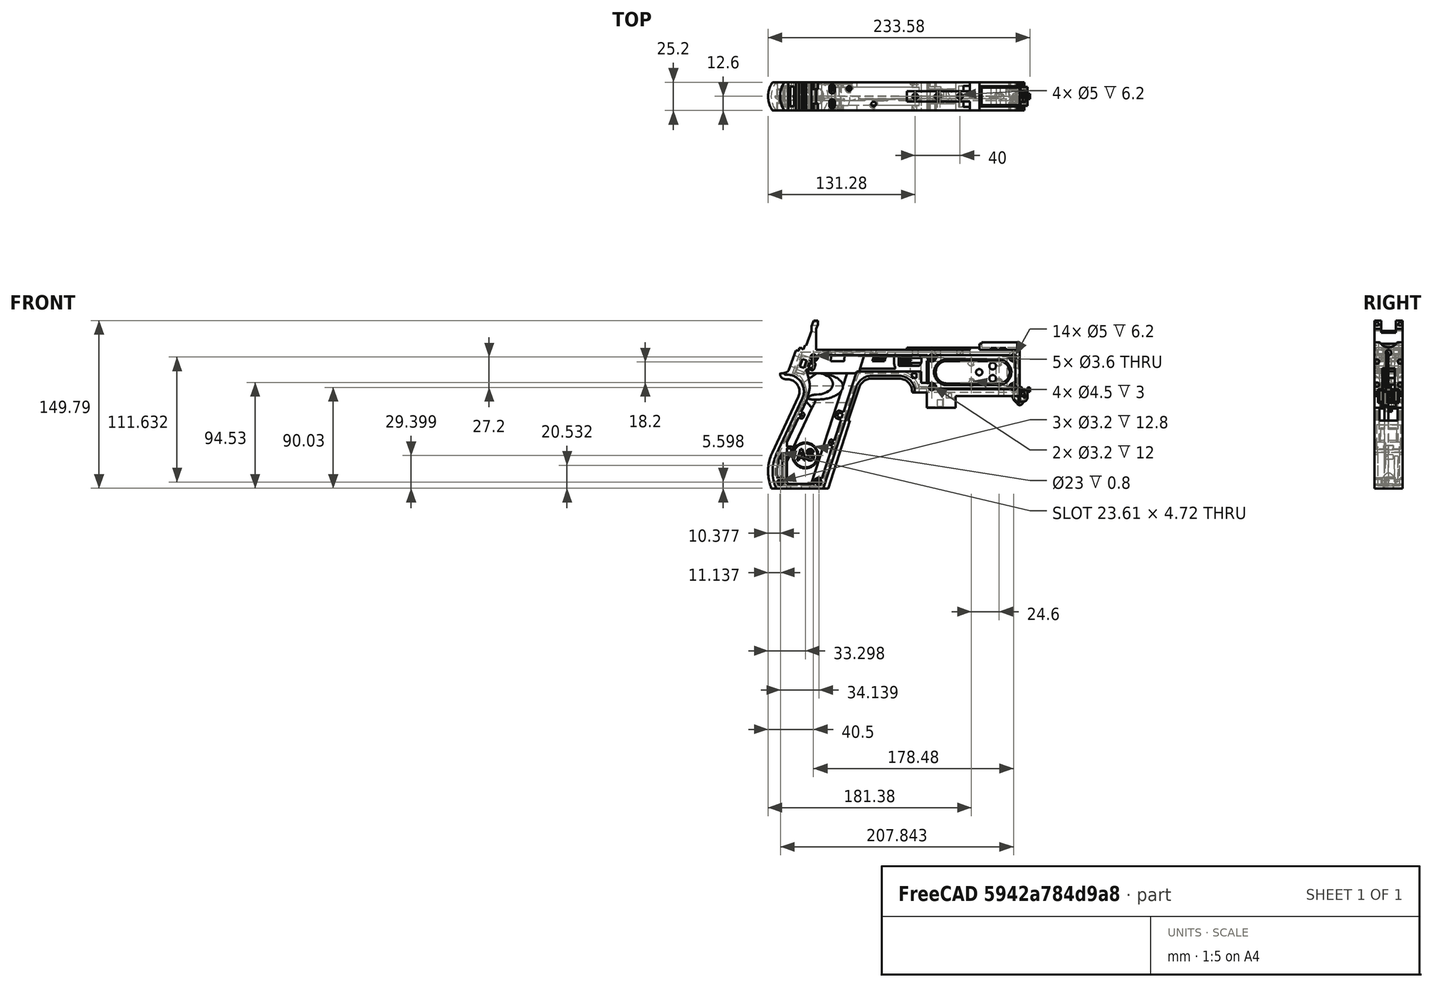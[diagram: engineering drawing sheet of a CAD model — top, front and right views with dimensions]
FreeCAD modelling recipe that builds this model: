
FCSTD DOCUMENT  (FreeCAD 1.0R39319 (Git))
Label: PICON-OF_ver_39_ultimo_della_prima_revisione
License: All rights reserved
LicenseURL: https://en.wikipedia.org/wiki/All_rights_reserved
objects: Sketcher::SketchObject×107, Part::Extrusion×50, Part::Cut×39, PartDesign::Pad×29, PartDesign::Pocket×18, PartDesign::Chamfer×15, PartDesign::Body×10, PartDesign::Fillet×6, PartDesign::SubtractivePipe×4, Part::Part2DObjectPython×4, PartDesign::SubtractiveLoft×4, PartDesign::Plane×2, PartDesign::SubShapeBinder×2, Part::Sweep×1, PartDesign::ShapeBinder×1, Part::MultiFuse×1, Mesh::Feature×1
note: 552 computed .brp shape members not serialized (recipe doc carries the construction recipe); baked Part::Feature solids carry a one-line shape summary decoded from their .brp

FEATURE [Sketcher::SketchObject] Sketch  label="corpo principale"
  ArcFitTolerance = 1e-06
  AttacherType = Attacher::AttachEngine3D
  AttachmentSupport = -> [XZ_Plane]
  FullyConstrained = true
  MakeInternals = false
  MapMode = 5
  Placement = pos=(0,0,0) rot=(1,0,0;1.5708rad)
  sketch-geometry (65):
    g0: LineSegment StartX=0 StartY=0 StartZ=0 EndX=-57.2 EndY=0 EndZ=0
    g1: LineSegment StartX=-57.2 StartY=0 StartZ=0 EndX=-57.2 EndY=-10.4 EndZ=0
    g2: LineSegment StartX=-57.2 StartY=-10.4 StartZ=0 EndX=-82.8 EndY=-10.4 EndZ=0
    g3: LineSegment StartX=-82.8 StartY=-10.4 StartZ=0 EndX=-82.8 EndY=3.2 EndZ=0
    g4: LineSegment StartX=-82.8 StartY=3.2 StartZ=0 EndX=-93.6 EndY=3.2 EndZ=0
    g5: LineSegment StartX=-93.6 StartY=3.2 StartZ=0 EndX=-93.6 EndY=4 EndZ=0
    g6: LineSegment StartX=-107.6 StartY=18 StartZ=0 EndX=-132.428 EndY=18 EndZ=0
    g7: LineSegment StartX=-145.743 StartY=8.32624 StartZ=0 EndX=-175.232 EndY=-82.4316 EndZ=0
    g8: LineSegment StartX=-175.232 StartY=-82.4316 StartZ=0 EndX=-217.232 EndY=-82.4316 EndZ=0
    g9: LineSegment StartX=-217.232 StartY=-52.1862 StartZ=0 EndX=-193.988 EndY=-2.33927 EndZ=0
    g10: LineSegment StartX=-206.196 StartY=23.0857 StartZ=0 EndX=-199.861 EndY=40.4914 EndZ=0
    g11: LineSegment StartX=-199.861 StartY=40.4914 StartZ=0 EndX=-197.061 EndY=40.4914 EndZ=0
    g12: LineSegment StartX=-197.061 StartY=40.4914 StartZ=0 EndX=-197.061 EndY=42.8914 EndZ=0
    g13: LineSegment StartX=-197.061 StartY=42.8914 StartZ=0 EndX=-194.261 EndY=42.8914 EndZ=0
    g14: LineSegment StartX=-194.261 StartY=42.8914 StartZ=0 EndX=-194.535 EndY=42.1397 EndZ=0
    g15: LineSegment StartX=-194.535 StartY=42.1397 StartZ=0 EndX=-193.031 EndY=41.5924 EndZ=0
    g16: LineSegment StartX=-193.031 StartY=41.5924 StartZ=0 EndX=-191.663 EndY=45.3512 EndZ=0
    g17: LineSegment StartX=-191.663 StartY=45.3512 StartZ=0 EndX=-190.536 EndY=44.9408 EndZ=0
    g18: LineSegment StartX=-190.536 StartY=44.9408 StartZ=0 EndX=-185.747 EndY=58.0965 EndZ=0
    g19: LineSegment StartX=-185.747 StartY=58.0965 StartZ=0 EndX=-185.747 EndY=62.0965 EndZ=0
    g20: LineSegment StartX=-185.747 StartY=62.0965 StartZ=0 EndX=-183.832 EndY=67.3588 EndZ=0
    g21: LineSegment StartX=-183.832 StartY=67.3588 StartZ=0 EndX=-180.232 EndY=67.3588 EndZ=0
    g22: LineSegment StartX=-180.232 StartY=67.3588 StartZ=0 EndX=-180.232 EndY=63.7588 EndZ=0
    g23: LineSegment StartX=-180.232 StartY=63.7588 StartZ=0 EndX=-181.6 EndY=60 EndZ=0
    g24: LineSegment StartX=-181.6 StartY=60 StartZ=0 EndX=-181.6 EndY=41.2 EndZ=0
    g25: LineSegment StartX=-181.6 StartY=41.2 StartZ=0 EndX=-100.8 EndY=41.2 EndZ=0
    g26: LineSegment StartX=-36 StartY=43.2 StartZ=0 EndX=-36 EndY=41.2 EndZ=0
    g27: LineSegment StartX=0 StartY=48 StartZ=0 EndX=0 EndY=0 EndZ=0
    g28: LineSegment StartX=-209.901 StartY=19.85 StartZ=0 EndX=-209.901 EndY=20.1 EndZ=0
    g29: LineSegment StartX=-208.001 StartY=22 StartZ=0 EndX=-207.747 EndY=22 EndZ=0
    g30: LineSegment StartX=-207.583 StartY=19 StartZ=0 EndX=-209.051 EndY=19 EndZ=0
    g31: ArcOfCircle CenterX=-208.001 CenterY=20.1 CenterZ=0 NormalX=0 NormalY=0 NormalZ=1 AngleXU=0 Radius=1.9 StartAngle=1.5708 EndAngle=3.14159
    g32: GeomPoint [constr] X=-209.901 Y=22 Z=0
    g33: ArcOfCircle CenterX=-209.051 CenterY=19.85 CenterZ=0 NormalX=0 NormalY=0 NormalZ=1 AngleXU=0 Radius=0.85 StartAngle=3.14159 EndAngle=4.71239
    g34: GeomPoint [constr] X=-209.901 Y=19 Z=0
    g35: ArcOfCircle CenterX=-207.747 CenterY=23.65 CenterZ=0 NormalX=0 NormalY=0 NormalZ=1 AngleXU=0 Radius=1.65 StartAngle=4.71239 EndAngle=5.93412
    g36: GeomPoint [constr] X=-206.591 Y=22 Z=0
    g37: LineSegment StartX=-4 StartY=6 StartZ=0 EndX=-4 EndY=36.4 EndZ=0
    g38: LineSegment StartX=-4 StartY=36.4 StartZ=0 EndX=-185.2 EndY=36.4 EndZ=0
    g39: LineSegment StartX=-185.2 StartY=36.4 StartZ=0 EndX=-190.441 EndY=22 EndZ=0
    g40: LineSegment StartX=-214.575 StartY=-78.4316 StartZ=0 EndX=-178.142 EndY=-78.4316 EndZ=0
    g41: LineSegment StartX=-178.142 StartY=-78.4316 StartZ=0 EndX=-145.51 EndY=22 EndZ=0
    g42: LineSegment StartX=-145.51 StartY=22 StartZ=0 EndX=-87.91 EndY=22 EndZ=0
    g43: LineSegment StartX=-87.91 StartY=22 StartZ=0 EndX=-87.91 EndY=11.6 EndZ=0
    g44: LineSegment StartX=-87.91 StartY=11.6 StartZ=0 EndX=-80.11 EndY=11.6 EndZ=0
    g45: LineSegment StartX=-80.11 StartY=11.6 StartZ=0 EndX=-80.11 EndY=6 EndZ=0
    g46: LineSegment StartX=-80.11 StartY=6 StartZ=0 EndX=-4 EndY=6 EndZ=0
    g47: LineSegment StartX=-190.363 StartY=-4.02975 StartZ=0 EndX=-213.607 EndY=-53.8767 EndZ=0
    g48: ArcOfCircle CenterX=-132.428 CenterY=4 CenterZ=0 NormalX=0 NormalY=0 NormalZ=1 AngleXU=0 Radius=14 StartAngle=1.5708 EndAngle=2.82743
    g49: GeomPoint [constr] X=-142.6 Y=18 Z=0
    g50: ArcOfCircle CenterX=-107.6 CenterY=4 CenterZ=0 NormalX=0 NormalY=0 NormalZ=1 AngleXU=0 Radius=14 StartAngle=0 EndAngle=1.5708
    g51: GeomPoint [constr] X=-93.6 Y=18 Z=0
    g52: ArcOfCircle CenterX=-184.801 CenterY=-67.3089 CenterZ=0 NormalX=0 NormalY=0 NormalZ=1 AngleXU=0 Radius=35.7833 StartAngle=2.70526 EndAngle=3.57792
    g53: ArcOfCircle CenterX=-207.583 CenterY=4 CenterZ=0 NormalX=0 NormalY=0 NormalZ=1 AngleXU=0 Radius=15 StartAngle=5.84685 EndAngle=7.85398
    g54: LineSegment [constr] StartX=-213.607 StartY=-53.8767 StartZ=0 EndX=-217.232 EndY=-52.1862 EndZ=0
    g55: ArcOfCircle CenterX=-184.801 CenterY=-67.3089 CenterZ=0 NormalX=0 NormalY=0 NormalZ=1 AngleXU=0 Radius=31.7833 StartAngle=2.70526 EndAngle=3.49911
    g56: ArcOfCircle CenterX=-218.095 CenterY=8.90192 CenterZ=0 NormalX=0 NormalY=0 NormalZ=1 AngleXU=0 Radius=30.5989 StartAngle=5.84685 EndAngle=6.72553
    g57: LineSegment StartX=-44.6 StartY=43.2 StartZ=0 EndX=-36 EndY=43.2 EndZ=0
    g58: LineSegment StartX=-100.8 StartY=41.2 StartZ=0 EndX=-44.6 EndY=41.2 EndZ=0
    g59: LineSegment StartX=-44.6 StartY=41.2 StartZ=0 EndX=-44.6 EndY=43.2 EndZ=0
    g60: LineSegment StartX=-2.4 StartY=48 StartZ=0 EndX=0 EndY=48 EndZ=0
    g61: LineSegment StartX=-36 StartY=41.2 StartZ=0 EndX=-2.4 EndY=41.2 EndZ=0
    g62: LineSegment StartX=-2.4 StartY=41.2 StartZ=0 EndX=-2.4 EndY=48 EndZ=0
    g63: LineSegment [constr] StartX=-181.6 StartY=36.4 StartZ=0 EndX=-152.209 EndY=36.4 EndZ=0
    g64: LineSegment [constr] StartX=-181.6 StartY=36.4 StartZ=0 EndX=-130.41 EndY=36.4 EndZ=0
  constraints (183):
    c: Coincident(g-1,g0)
    c: PointOnObject(g0,g-1)
    c: Coincident(g0,g1)
    c: Vertical(g1)
    c: Coincident(g1,g2)
    c: Horizontal(g2)
    c: Coincident(g2,g3)
    c: Vertical(g3)
    c: Coincident(g3,g4)
    c: Coincident(g4,g5)
    c: Vertical(g5)
    c: Horizontal(g6)
    c: Coincident(g7,g8)
    c: Horizontal(g8)
    c: Coincident(g10,g11)
    c: Horizontal(g11)
    c: Coincident(g11,g12)
    c: Vertical(g12)
    c: Coincident(g12,g13)
    c: Horizontal(g13)
    c: Coincident(g13,g14)
    c: Coincident(g14,g15)
    c: Coincident(g15,g16)
    c: Coincident(g16,g17)
    c: Coincident(g17,g18)
    c: Coincident(g18,g19)
    c: Vertical(g19)
    c: Coincident(g19,g20)
    c: Coincident(g20,g21)
    c: Horizontal(g21)
    c: Coincident(g21,g22)
    c: Vertical(g22)
    c: Coincident(g22,g23)
    c: Coincident(g23,g24)
    c: Vertical(g24)
    c: Coincident(g24,g25)
    c: Horizontal(g25)
    c: Coincident(g57,g26)
    c: Vertical(g26)
    c: Coincident(g26,g61)
    c: PointOnObject(g60,g-2)
    c: Coincident(g60,g27)
    c: Coincident(g27,g0)
    c: DistanceY(g27,g27) = 48
    c: DistanceY(g1,g1) = 10.4
    c: DistanceX(g0,g0) = 57.2
    c: DistanceX(g2,g2) = 25.6
    c: Horizontal(g4)
    c: DistanceY(g3,g3) = 13.6
    c: DistanceX(g4,g4) = 10.8
    c: DistanceY(g5,g51) = 14.8
    c: DistanceX(g49,g51) = 49
    c: Distance(g7,g49) = 105.6
    c: DistanceX(g61,g60) = 36
    c: DistanceX(g25,g25) = 80.8
    c: DistanceY(g24,g24) = 18.8
    c: DistanceY(g22,g22) = 3.6
    c: Distance(g23) = 4
    c: Angle(g-1,g23) = 1.22173
    c: DistanceX(g21,g21) = 3.6
    c: Distance(g20) = 5.6
    c: Angle(g-1,g20) = 1.22173
    c: DistanceY(g19,g19) = 4
    c: Distance(g18) = 14
    c: Angle(g-1,g18) = 1.22173
    c: Distance(g17) = 1.2
    c: Distance(g16) = 4
    c: Angle(g16) = 1.22173
    c: Perpendicular(g18,g17)
    c: Distance(g15) = 1.6
    c: Perpendicular(g16,g15)
    c: Distance(g14) = 0.8
    c: DistanceX(g13,g13) = 2.8
    c: Perpendicular(g15,g14)
    c: DistanceY(g12,g12) = 2.4
    c: DistanceX(g11,g11) = 2.8
    c: Distance(g9) = 55
    c: Angle(g9,g-1) = 2.00713
    c: Horizontal(g29)
    c: Vertical(g28)
    c: Horizontal(g30)
    c: PointOnObject(g32,g29)
    c: PointOnObject(g32,g28)
    c: Tangent(g29,g31) = 1.5708
    c: Tangent(g28,g31) = 1.5708
    c: PointOnObject(g34,g28)
    c: PointOnObject(g34,g30)
    c: Tangent(g28,g33) = 1.5708
    c: Tangent(g30,g33) = 1.5708
    c: PointOnObject(g36,g29)
    c: PointOnObject(g36,g10)
    c: Tangent(g29,g35) = -1.5708
    c: Tangent(g10,g35) = -1.5708
    c: Angle(g-1,g10) = 1.22173
    c: Radius(g35) = 1.65
    c: Vertical(g37)
    c: Coincident(g37,g38)
    c: Horizontal(g38)
    c: Coincident(g38,g39)
    c: Horizontal(g40)
    c: Coincident(g40,g41)
    c: Coincident(g41,g42)
    c: Horizontal(g42)
    c: Coincident(g42,g43)
    c: Vertical(g43)
    c: Coincident(g43,g44)
    c: Horizontal(g44)
    c: Coincident(g44,g45)
    c: Vertical(g45)
    c: Coincident(g45,g46)
    c: Coincident(g46,g37)
    c: Horizontal(g46)
    c: DistanceY(g0,g37) = 6
    c: DistanceX(g37,g0) = 4
    c: DistanceY(g37,g25) = 4.8
    c: DistanceX(g38,g38) = 181.2
    c: DistanceX(g42,g42) = 57.6
    c: DistanceY(g49,g41) = 4
    c: DistanceX(g41,g49) = 2.91
    c: DistanceY(g43,g43) = 10.4
    c: DistanceX(g44,g44) = 7.8
    c: DistanceY(g7,g40) = 4
    c: Distance(g47) = 55
    c: Angle(g-1,g39) = 1.22173
    c: PointOnObject(g49,g7)
    c: PointOnObject(g49,g6)
    c: Tangent(g7,g48) = -1.5708
    c: Tangent(g6,g48) = -1.5708
    c: PointOnObject(g51,g5)
    c: PointOnObject(g51,g6)
    c: Tangent(g5,g50) = -1.5708
    c: Tangent(g6,g50) = -1.5708
    c: Radius(g50) = 14
    c: Radius(g48) = 14
    c: DistanceX(g8,g8) = 42
    c: Angle(g7,g-1) = 1.88496
    c: Parallel(g41,g7)
    c: Parallel(g47,g9)
    c: Coincident(g52,g8)
    c: Tangent(g52,g9) = 1.5708
    c: DistanceX(g9,g8) = 0
    c: Tangent(g53,g9) = -1.5708
    c: Tangent(g53,g30) = -1.5708
    c: Diameter(g53) = 30
    c: DistanceY(g53,g0) = -4
    c: Coincident(g54,g47)
    c: Distance(g54) = 4
    c: Coincident(g54,g9)
    c: Coincident(g55,g40)
    c: Tangent(g55,g47) = -1.5708
    c: Coincident(g52,g55)
    c: Coincident(g56,g39)
    c: Tangent(g56,g47) = 1.5708
    c: Horizontal(g57)
    c: DistanceX(g57,g57) = 8.6
    c: Coincident(g58,g25)
    c: Horizontal(g58)
    c: Coincident(g59,g58)
    c: Vertical(g59)
    c: DistanceY(g58,g57) = 2
    c: DistanceX(g58,g58) = 56.2
    c: Coincident(g59,g57)
    c: DistanceY(g41,g36) = 0
    c: DistanceY(g36,g39) = 0
    c: DistanceY(g28,g28) = 0.25
    c: DistanceX(g30,g36) = 2.46
    c: DistanceX(g28,g29) = 1.9
    c: Coincident(g62,g60)
    c: Horizontal(g60)
    c: DistanceX(g62,g27) = 2.4
    c: Coincident(g61,g62)
    c: DistanceY(g26,g26) = 2
    c: Vertical(g62)
    c: DistanceY(g61,g60) = 6.8
    c: Horizontal(g61)
    c: Distance(g63) = 29.391
    c: PointOnObject(g63,g38)
    c: PointOnObject(g63,g38)
    c: Distance(g64) = 51.19
    c: PointOnObject(g64,g38)
    c: PointOnObject(g64,g38)
    c: DistanceX(g24,g63) = 0
    c: DistanceX(g24,g64) = 0
FEATURE [Part::Extrusion] Extrude  label="Extrude corpo principale"
  Base = -> Sketch
  Dir = (0,-1,2e-16)
  DirMode = 2
  FaceMakerClass = Part::FaceMakerBullseye
  FaceMakerMode = 3
  LengthFwd = 25.2
  LengthRev = 12.6
  Solid = true
  Symmetric = true
FEATURE [Sketcher::SketchObject] Sketch002  label="scavo grilletto"
  ArcFitTolerance = 1e-06
  AttachmentSupport = -> [XZ_Plane]
  ExternalGeometry = -> [Sketch]
  FullyConstrained = true
  MakeInternals = false
  MapMode = 5
  Placement = pos=(0,0,0) rot=(1,0,0;1.5708rad)
  sketch-geometry (4):
    g0: LineSegment StartX=-89.51 StartY=22 StartZ=0 EndX=-152.71 EndY=22 EndZ=0
    g1: LineSegment StartX=-152.71 StartY=22 StartZ=0 EndX=-167.006 EndY=-22 EndZ=0
    g2: LineSegment StartX=-167.006 StartY=-22 StartZ=0 EndX=-89.51 EndY=-22 EndZ=0
    g3: LineSegment StartX=-89.51 StartY=-22 StartZ=0 EndX=-89.51 EndY=22 EndZ=0
  constraints (12):
    c: Horizontal(g0)
    c: Coincident(g0,g1)
    c: Coincident(g1,g2)
    c: Horizontal(g2)
    c: Coincident(g2,g3)
    c: Coincident(g3,g0)
    c: Vertical(g3)
    c: Angle(g1,g0) = 1.88496
    c: DistanceY(g3,g3) = 44
    c: DistanceX(g0,g0) = 63.2
    c: DistanceX(g0,g-3) = 1.6
    c: DistanceY(g-3,g0) = 0
FEATURE [Sketcher::SketchObject] Sketch004  label="traiettoria arrotondamento impugnatura anteriore"
  ArcFitTolerance = 1e-06
  AttachmentSupport = -> [XZ_Plane]
  ExternalGeometry = -> [Sketch]
  FullyConstrained = true
  MakeInternals = false
  MapMode = 5
  Placement = pos=(0,0,0) rot=(1,0,0;1.5708rad)
  sketch-geometry (13):
    g0: LineSegment StartX=-175.232 StartY=-82.4316 StartZ=0 EndX=-145.743 EndY=8.32624 EndZ=0
    g1: LineSegment StartX=-93.6 StartY=3.2 StartZ=0 EndX=-93.6 EndY=4 EndZ=0
    g2: LineSegment StartX=-132.428 StartY=18 StartZ=0 EndX=-107.6 EndY=18 EndZ=0
    g3: ArcOfCircle CenterX=-132.428 CenterY=4 CenterZ=0 NormalX=0 NormalY=0 NormalZ=1 AngleXU=0 Radius=14 StartAngle=1.5708 EndAngle=2.82743
    g4: ArcOfCircle CenterX=-107.6 CenterY=4 CenterZ=0 NormalX=0 NormalY=0 NormalZ=1 AngleXU=0 Radius=14 StartAngle=0 EndAngle=1.5708
    g5: LineSegment StartX=-175.232 StartY=-82.4316 StartZ=0 EndX=-217.232 EndY=-82.4316 EndZ=0
    g6: LineSegment StartX=-217.232 StartY=-52.1862 StartZ=0 EndX=-193.988 EndY=-2.33927 EndZ=0
    g7: LineSegment StartX=-209.051 StartY=19 StartZ=0 EndX=-207.583 EndY=19 EndZ=0
    g8: LineSegment StartX=-209.901 StartY=20.1 StartZ=0 EndX=-209.901 EndY=19.85 EndZ=0
    g9: ArcOfCircle CenterX=-184.801 CenterY=-67.3089 CenterZ=0 NormalX=0 NormalY=0 NormalZ=1 AngleXU=0 Radius=35.7833 StartAngle=2.70526 EndAngle=3.57792
    g10: ArcOfCircle CenterX=-207.583 CenterY=4 CenterZ=0 NormalX=0 NormalY=0 NormalZ=1 AngleXU=0 Radius=15 StartAngle=5.84685 EndAngle=7.85398
    g11: ArcOfCircle CenterX=-209.051 CenterY=19.85 CenterZ=0 NormalX=0 NormalY=0 NormalZ=1 AngleXU=0 Radius=0.85 StartAngle=3.14159 EndAngle=4.71239
    g12: ArcOfCircle CenterX=-208.001 CenterY=20.1 CenterZ=0 NormalX=0 NormalY=0 NormalZ=1 AngleXU=0 Radius=1.9 StartAngle=1.5708 EndAngle=3.14159
  constraints (26):
    c: Coincident(g0,g-3)
    c: Coincident(g0,g-6)
    c: Coincident(g1,g-8)
    c: Coincident(g1,g-7)
    c: Coincident(g2,g-5)
    c: Coincident(g2,g-4)
    c: Coincident(g3,g2)
    c: Tangent(g3,g0) = 1.5708
    c: Coincident(g4,g1)
    c: Tangent(g4,g2) = 1.5708
    c: Coincident(g5,g0)
    c: Coincident(g5,g-9)
    c: Coincident(g6,g-12)
    c: Coincident(g6,g-11)
    c: Coincident(g7,g-15)
    c: Coincident(g7,g-14)
    c: Coincident(g8,g-16)
    c: Coincident(g8,g-17)
    c: Tangent(g9,g6) = 1.5708
    c: Coincident(g9,g5)
    c: Coincident(g10,g7)
    c: Tangent(g10,g6) = -1.5708
    c: Tangent(g11,g7) = -1.5708
    c: Coincident(g11,g8)
    c: Tangent(g12,g8) = -1.5708
    c: Coincident(g12,g-17)
FEATURE [PartDesign::Plane] DatumPlane  label="Piano per disegno arrotondamento impugnatura"
  AttachmentSupport = -> [Sketch]
  Length = 68.5841
  MapMode = 7
  Placement = pos=(-145.743,1.8e-15,8.32624) rot=(0.154555,0.154555,0.97582;1.59527rad)
  ResizeMode = 0
  Width = 191.269
FEATURE [Sketcher::SketchObject] Sketch005  label="forma arrotondamento impugnatura anteriore"
  ArcFitTolerance = 1e-06
  AttachmentSupport = -> [DatumPlane]
  FullyConstrained = true
  MakeInternals = false
  MapMode = 5
  Placement = pos=(-145.743,1.8e-15,8.32624) rot=(0.154555,0.154555,0.97582;1.59527rad)
  sketch-geometry (5):
    g0: GeomPoint [constr] X=0 Y=-4 Z=0
    g1: GeomPoint [constr] X=-12.6 Y=7.1e-15 Z=0
    g2: GeomPoint [constr] X=12.6 Y=4.97e-14 Z=0
    g3: LineSegment StartX=-12.6 StartY=7.1e-15 StartZ=0 EndX=12.6 EndY=4.97e-14 EndZ=0
    g4: ArcOfCircle CenterX=-3.88e-14 CenterY=17.845 CenterZ=0 NormalX=0 NormalY=0 NormalZ=1 AngleXU=0 Radius=21.845 StartAngle=4.09759 EndAngle=5.32718
  constraints (11):
    c: DistanceY(g0,g-1) = 4
    c: DistanceX(g-1,g0) = 0
    c: DistanceX(g1,g-1) = 12.6
    c: DistanceX(g-1,g2) = 12.6
    c: DistanceY(g-1,g2) = 0
    c: DistanceY(g-1,g1) = 0
    c: Coincident(g3,g1)
    c: Coincident(g3,g2)
    c: Coincident(g4,g1)
    c: Coincident(g4,g2)
    c: PointOnObject(g0,g4)
FEATURE [Part::Sweep] Sweep  label="Sweep impugnatura"
  Frenet = true
  Sections = -> [Sketch005]
  Solid = true
  Spine = -> Sketch [Edge32,Edge33,Edge34,Edge35,Edge36,Edge37,Edge38,Edge39,Edge40,Edge41,Edge42,Edge43,Edge44]
  Transition = 1
FEATURE [Sketcher::SketchObject] Sketch008  label="buchi e pulizie varie"
  ArcFitTolerance = 1e-06
  AttachmentSupport = -> [XZ_Plane]
  ExternalGeometry = -> [Sketch]
  FullyConstrained = true
  MakeInternals = false
  MapMode = 5
  Placement = pos=(0,0,0) rot=(1,0,0;1.5708rad)
  sketch-geometry (26):
    g0: LineSegment StartX=-96.278 StartY=20.155 StartZ=0 EndX=-92.278 EndY=20.155 EndZ=0
    g1: LineSegment StartX=-92.278 StartY=20.155 StartZ=0 EndX=-92.278 EndY=16.155 EndZ=0
    g2: LineSegment StartX=-92.278 StartY=16.155 StartZ=0 EndX=-96.278 EndY=16.155 EndZ=0
    g3: LineSegment StartX=-96.278 StartY=16.155 StartZ=0 EndX=-96.278 EndY=20.155 EndZ=0
    g4: LineSegment StartX=-222.232 StartY=-82.4316 StartZ=0 EndX=-170.232 EndY=-82.4316 EndZ=0
    g5: LineSegment StartX=-170.232 StartY=-82.4316 StartZ=0 EndX=-170.232 EndY=-86.4316 EndZ=0
    g6: LineSegment StartX=-170.232 StartY=-86.4316 StartZ=0 EndX=-222.232 EndY=-86.4316 EndZ=0
    g7: LineSegment StartX=-222.232 StartY=-86.4316 StartZ=0 EndX=-222.232 EndY=-82.4316 EndZ=0
    g8: LineSegment StartX=-213.901 StartY=20.1 StartZ=0 EndX=-213.901 EndY=26 EndZ=0
    g9: LineSegment StartX=-213.901 StartY=26 StartZ=0 EndX=-206.196 EndY=26 EndZ=0
    g10: LineSegment StartX=-17.4 StartY=42.8 StartZ=0 EndX=-12.4 EndY=42.8 EndZ=0
    g11: LineSegment StartX=-12.4 StartY=42.8 StartZ=0 EndX=-12.4 EndY=41.2 EndZ=0
    g12: LineSegment StartX=-12.4 StartY=41.2 StartZ=0 EndX=-17.4 EndY=41.2 EndZ=0
    g13: LineSegment StartX=-17.4 StartY=41.2 StartZ=0 EndX=-17.4 EndY=42.8 EndZ=0
    g14: LineSegment StartX=-25.9 StartY=42.8 StartZ=0 EndX=-20.9 EndY=42.8 EndZ=0
    g15: LineSegment StartX=-20.9 StartY=42.8 StartZ=0 EndX=-20.9 EndY=41.2 EndZ=0
    g16: LineSegment StartX=-20.9 StartY=41.2 StartZ=0 EndX=-25.9 EndY=41.2 EndZ=0
    g17: LineSegment StartX=-25.9 StartY=41.2 StartZ=0 EndX=-25.9 EndY=42.8 EndZ=0
    g18: GeomPoint [constr] X=-206.196 Y=23.0857 Z=0
    g19: GeomPoint [constr] X=-213.901 Y=20.1 Z=0
    g20: BSplineCurve PolesCount=4 KnotsCount=2 Degree=3 IsPeriodic=0
    g21-g24: Circle [constr] x4 (B-spline internal-alignment scaffolding for g20; pole/knot coordinates omitted)
    g25: LineSegment StartX=-206.196 StartY=26 StartZ=0 EndX=-206.196 EndY=23.0857 EndZ=0
  constraints (73):
    c: Horizontal(g0)
    c: Coincident(g1,g0)
    c: Vertical(g1)
    c: Coincident(g2,g1)
    c: Horizontal(g2)
    c: Coincident(g3,g2)
    c: Coincident(g3,g0)
    c: Vertical(g3)
    c: DistanceX(g0,g-4) = 4.368
    c: DistanceY(g0,g-4) = 1.845
    c: DistanceY(g1,g1) = 4
    c: DistanceX(g2,g2) = 4
    c: Horizontal(g4)
    c: Coincident(g5,g4)
    c: Vertical(g5)
    c: Coincident(g6,g5)
    c: Horizontal(g6)
    c: Coincident(g7,g6)
    c: Coincident(g7,g4)
    c: Vertical(g7)
    c: DistanceY(g7,g7) = 4
    c: DistanceX(g4,g-5) = 5
    c: DistanceX(g-5,g4) = 5
    c: DistanceY(g4,g-5) = 0
    c: Coincident(g9,g8)
    c: Parallel(g9,g-6)
    c: DistanceX(g8,g-8) = 4
    c: Horizontal(g10)
    c: Coincident(g11,g10)
    c: Vertical(g11)
    c: Coincident(g12,g11)
    c: Horizontal(g12)
    c: Coincident(g13,g12)
    c: Coincident(g13,g10)
    c: Vertical(g13)
    c: Horizontal(g14)
    c: Coincident(g15,g14)
    c: Vertical(g15)
    c: Coincident(g16,g15)
    c: Horizontal(g16)
    c: Coincident(g17,g16)
    c: Coincident(g17,g14)
    c: Vertical(g17)
    c: DistanceY(g11,g10) = 1.6
    c: DistanceX(g10,g10) = 5
    c: DistanceY(g15,g14) = 1.6
    c: DistanceX(g14,g14) = 5
    c: DistanceX(g15,g12) = 3.5
    c: DistanceX(g11,g-9) = 10
    c: DistanceY(g-9,g11) = 0
    c: DistanceY(g-9,g15) = 0
    c: Perpendicular(g8,g9)
    c: DistanceY(g-7,g9) = 4
    c: DistanceY(g8,g-8) = 0
    c: InternalAlignment(g18,g20)
    c: InternalAlignment(g19,g20)
    c: InternalAlignment(g21,g20)
    c: Weight(g21) = 1
    c: InternalAlignment(g22,g20)
    c: Equal(g22,g21)
    c: InternalAlignment(g23,g20)
    c: Equal(g23,g21)
    c: InternalAlignment(g24,g20)
    c: Equal(g24,g21)
    c: Coincident(g18,g-12)
    c: Coincident(g19,g8)
    c: Coincident(g25,g9)
    c: Coincident(g25,g20)
    c: Vertical(g25)
    c: DistanceY(g20,g23) = 0
    c: DistanceY(g22,g18) = 2.26
    c: DistanceX(g22,g18) = 0.93
    c: DistanceX(g20,g23) = 2.9
FEATURE [Part::Extrusion] Extrude004  label="Extrude Buchi e pulizie varie"
  Base = -> Sketch008
  Dir = (0,-1,2e-16)
  DirMode = 2
  FaceMakerClass = Part::FaceMakerBullseye
  FaceMakerMode = 3
  LengthFwd = 25.2
  LengthRev = 0
  Solid = true
  Symmetric = true
FEATURE [Sketcher::SketchObject] Sketch009  label="rinforzi"
  ArcFitTolerance = 1e-06
  AttachmentSupport = -> [XZ_Plane]
  ExternalGeometry = -> [Sketch]
  FullyConstrained = true
  MakeInternals = false
  MapMode = 5
  Placement = pos=(0,0,0) rot=(1,0,0;1.5708rad)
  sketch-geometry (9):
    g0: LineSegment StartX=-87.91 StartY=22 StartZ=0 EndX=-87.91 EndY=36.4 EndZ=0
    g1: LineSegment StartX=-87.91 StartY=36.4 StartZ=0 EndX=-97.91 EndY=36.4 EndZ=0
    g2: LineSegment StartX=-97.91 StartY=36.4 StartZ=0 EndX=-97.91 EndY=22 EndZ=0
    g3: LineSegment StartX=-97.91 StartY=22 StartZ=0 EndX=-87.91 EndY=22 EndZ=0
    g4: LineSegment StartX=-149.713 StartY=9.06563 StartZ=0 EndX=-154.586 EndY=-5.93437 EndZ=0
    g5: LineSegment StartX=-154.586 StartY=-5.93437 StartZ=0 EndX=-191.863 EndY=-5.93437 EndZ=0
    g6: LineSegment StartX=-191.863 StartY=-5.93437 StartZ=0 EndX=-191.863 EndY=9.06563 EndZ=0
    g7: LineSegment StartX=-191.863 StartY=9.06563 StartZ=0 EndX=-149.713 EndY=9.06563 EndZ=0
    g8: LineSegment [constr] StartX=-145.51 StartY=22 StartZ=0 EndX=-149.713 EndY=9.06563 EndZ=0
  constraints (25):
    c: Vertical(g0)
    c: Coincident(g1,g0)
    c: Horizontal(g1)
    c: Coincident(g2,g1)
    c: Vertical(g2)
    c: Coincident(g3,g2)
    c: Coincident(g3,g0)
    c: Horizontal(g3)
    c: Coincident(g0,g-4)
    c: DistanceX(g3,g3) = 10
    c: DistanceY(g0,g-3) = 0
    c: Coincident(g5,g4)
    c: Horizontal(g5)
    c: Coincident(g6,g5)
    c: Vertical(g6)
    c: Coincident(g7,g6)
    c: Coincident(g7,g4)
    c: Horizontal(g7)
    c: Distance(g8) = 13.6
    c: Parallel(g-6,g8)
    c: Coincident(g-6,g8)
    c: Parallel(g4,g-6)
    c: DistanceY(g4,g4) = 15
    c: Coincident(g4,g8)
    c: DistanceX(g-5,g5) = -1.5
FEATURE [Part::Extrusion] Extrude001  label="Extrude scavo grilletto"
  Base = -> Sketch002
  Dir = (0,-1,2e-16)
  DirMode = 2
  FaceMakerClass = Part::FaceMakerBullseye
  FaceMakerMode = 3
  LengthFwd = 16
  LengthRev = 0
  Solid = true
  Symmetric = true
FEATURE [Part::Extrusion] Extrude005  label="Extrude Rinforzi"
  Base = -> Sketch009
  Dir = (0,-1,2e-16)
  DirMode = 2
  FaceMakerClass = Part::FaceMakerBullseye
  FaceMakerMode = 3
  LengthFwd = 2
  LengthRev = 0
  Placement = pos=(0,12.6,0) rot=(0,0,1;0rad)
  Solid = true
  Symmetric = false
FEATURE [PartDesign::ShapeBinder] CopyCut
  TraceSupport = false
FEATURE [PartDesign::Plane] DatumPlane001
  AttachmentSupport = -> [CopyCut]
  Length = 60
  MapMode = 5
  Placement = pos=(0,12.6,0) rot=(0,0.707107,0.707107;3.14159rad)
  ResizeMode = 0
  Width = 60
FEATURE [Sketcher::SketchObject] Sketch010  label="buco neopixel"
  ArcFitTolerance = 1e-06
  AttachmentSupport = -> [XZ_Plane]
  ExternalGeometry = -> [Sketch]
  FullyConstrained = true
  MakeInternals = false
  MapMode = 5
  Placement = pos=(0,0,0) rot=(1,0,0;1.5708rad)
  sketch-geometry (5):
    g0: LineSegment [constr] StartX=-199.861 StartY=40.4914 StartZ=0 EndX=-201.368 EndY=36.3521 EndZ=0
    g1: LineSegment StartX=-201.368 StartY=36.3521 StartZ=0 EndX=-204.932 EndY=26.5605 EndZ=0
    g2: LineSegment StartX=-201.368 StartY=36.3521 StartZ=0 EndX=-180.2 EndY=28.6477 EndZ=0
    g3: LineSegment StartX=-180.2 StartY=28.6477 StartZ=0 EndX=-183.764 EndY=18.8561 EndZ=0
    g4: LineSegment StartX=-183.764 StartY=18.8561 StartZ=0 EndX=-204.932 EndY=26.5605 EndZ=0
  constraints (14):
    c: Parallel(g0,g-3)
    c: Distance(g0) = 4.405
    c: Coincident(g0,g-3)
    c: Coincident(g2,g1)
    c: Coincident(g3,g2)
    c: Coincident(g4,g3)
    c: Coincident(g4,g1)
    c: Parallel(g1,g-3)
    c: Distance(g1) = 10.42
    c: Coincident(g1,g0)
    c: Parallel(g2,g4)
    c: Perpendicular(g1,g2)
    c: DistanceX(g-4,g2) = 5
    c: Parallel(g3,g1)
FEATURE [Part::Extrusion] Extrude006  label="Extrude buco neopixel"
  Base = -> Sketch010
  Dir = (0,-1,2e-16)
  DirMode = 2
  FaceMakerClass = Part::FaceMakerBullseye
  FaceMakerMode = 3
  LengthFwd = 17.2
  LengthRev = 0
  Solid = true
  Symmetric = true
FEATURE [Sketcher::SketchObject] Sketch011  label="fermo grilletto"
  ArcFitTolerance = 1e-06
  AttachmentSupport = -> [XZ_Plane]
  ExternalGeometry = -> [Sketch]
  FullyConstrained = true
  MakeInternals = false
  MapMode = 5
  Placement = pos=(0,0,0) rot=(1,0,0;1.5708rad)
  sketch-geometry (18):
    g0: LineSegment [constr] StartX=-145.51 StartY=22 StartZ=0 EndX=-157.347 EndY=-14.4293 EndZ=0
    g1: LineSegment [constr] StartX=-157.347 StartY=-14.4293 StartZ=0 EndX=-157.841 EndY=-15.951 EndZ=0
    g2: LineSegment StartX=-161.151 StartY=-13.1932 StartZ=0 EndX=-155.825 EndY=-14.9237 EndZ=0
    g3: LineSegment StartX=-163.167 StartY=-14.2205 StartZ=0 EndX=-164.403 EndY=-18.0247 EndZ=0
    g4: LineSegment StartX=-163.376 StartY=-20.0408 StartZ=0 EndX=-158.05 EndY=-21.7713 EndZ=0
    g5: LineSegment StartX=-158.05 StartY=-21.7713 StartZ=0 EndX=-155.825 EndY=-14.9237 EndZ=0
    g6: LineSegment StartX=-161.645 StartY=-14.7149 StartZ=0 EndX=-157.841 EndY=-15.951 EndZ=0
    g7: LineSegment StartX=-157.841 StartY=-15.951 StartZ=0 EndX=-159.077 EndY=-19.7552 EndZ=0
    g8: LineSegment StartX=-159.077 StartY=-19.7552 StartZ=0 EndX=-162.881 EndY=-18.5191 EndZ=0
    g9: LineSegment StartX=-162.881 StartY=-18.5191 StartZ=0 EndX=-161.645 EndY=-14.7149 EndZ=0
    g10: LineSegment [constr] StartX=-161.645 StartY=-14.7149 StartZ=0 EndX=-161.151 EndY=-13.1932 EndZ=0
    g11: LineSegment [constr] StartX=-159.077 StartY=-19.7552 StartZ=0 EndX=-157.555 EndY=-20.2496 EndZ=0
    g12: LineSegment [constr] StartX=-159.077 StartY=-19.7552 StartZ=0 EndX=-159.572 EndY=-21.2769 EndZ=0
    g13: LineSegment [constr] StartX=-161.645 StartY=-14.7149 StartZ=0 EndX=-163.167 EndY=-14.2205 EndZ=0
    g14: ArcOfCircle CenterX=-161.645 CenterY=-14.7149 CenterZ=0 NormalX=0 NormalY=0 NormalZ=1 AngleXU=0 Radius=1.6 StartAngle=1.25664 EndAngle=2.82743
    g15: GeomPoint [constr] X=-162.673 Y=-12.6988 Z=0
    g16: ArcOfCircle CenterX=-162.881 CenterY=-18.5191 CenterZ=0 NormalX=0 NormalY=0 NormalZ=1 AngleXU=0 Radius=1.6 StartAngle=2.82743 EndAngle=4.39823
    g17: GeomPoint [constr] X=-164.897 Y=-19.5464 Z=0
  constraints (48):
    c: Parallel(g0,g-3)
    c: Distance(g0) = 38.304
    c: Coincident(g0,g-3)
    c: Parallel(g1,g-3)
    c: Distance(g1) = 1.6
    c: Coincident(g1,g0)
    c: Coincident(g5,g4)
    c: Coincident(g5,g2)
    c: Coincident(g7,g6)
    c: Coincident(g8,g7)
    c: Coincident(g9,g8)
    c: Coincident(g9,g6)
    c: Parallel(g7,g-3)
    c: Parallel(g9,g7)
    c: Perpendicular(g6,g7)
    c: Parallel(g6,g8)
    c: Distance(g6) = 4
    c: Distance(g9) = 4
    c: Parallel(g5,g7)
    c: Parallel(g9,g3)
    c: Parallel(g2,g6)
    c: Parallel(g4,g8)
    c: Parallel(g13,g6)
    c: Parallel(g10,g9)
    c: Parallel(g11,g8)
    c: Parallel(g12,g7)
    c: Distance(g10) = 1.6
    c: Distance(g13) = 1.6
    c: Distance(g12) = 1.6
    c: Distance(g11) = 1.6
    c: Coincident(g10,g6)
    c: Coincident(g13,g6)
    c: Coincident(g12,g7)
    c: Coincident(g11,g7)
    c: Distance(g10,g15) = 1.6
    c: Distance(g15,g13) = 1.6
    c: Distance(g4,g12) = 1.6
    c: Distance(g4,g11) = 1.6
    c: PointOnObject(g15,g2)
    c: Tangent(g3,g14) = -1.5708
    c: Tangent(g2,g14) = 1.5708
    c: PointOnObject(g17,g4)
    c: PointOnObject(g17,g3)
    c: Tangent(g4,g16) = -1.5708
    c: Tangent(g3,g16) = -1.5708
    c: Equal(g16,g14)
    c: Coincident(g16,g8)
    c: Coincident(g6,g1)
FEATURE [Part::Extrusion] Extrude007  label="Extrude fermo grilletto"
  Base = -> Sketch011
  Dir = (0,-1,2e-16)
  DirMode = 2
  FaceMakerClass = Part::FaceMakerBullseye
  FaceMakerMode = 3
  LengthFwd = 25.2
  LengthRev = 0
  Solid = true
  Symmetric = true
FEATURE [Sketcher::SketchObject] Sketch012  label="buco oled"
  ArcFitTolerance = 1e-06
  AttachmentSupport = -> [XZ_Plane]
  ExternalGeometry = -> [Sketch]
  FullyConstrained = true
  MakeInternals = false
  MapMode = 5
  Placement = pos=(0,0,0) rot=(1,0,0;1.5708rad)
  sketch-geometry (4):
    g0: LineSegment StartX=-185.747 StartY=58.0965 StartZ=0 EndX=-180.232 EndY=56.0891 EndZ=0
    g1: LineSegment StartX=-185.747 StartY=58.0965 StartZ=0 EndX=-185.747 EndY=67.3588 EndZ=0
    g2: LineSegment StartX=-185.747 StartY=67.3588 StartZ=0 EndX=-180.232 EndY=67.3588 EndZ=0
    g3: LineSegment StartX=-180.232 StartY=67.3588 StartZ=0 EndX=-180.232 EndY=56.0891 EndZ=0
  constraints (10):
    c: Coincident(g1,g0)
    c: Coincident(g2,g1)
    c: Coincident(g3,g2)
    c: Coincident(g3,g0)
    c: Parallel(g1,g-5)
    c: Perpendicular(g-3,g0)
    c: Parallel(g2,g-6)
    c: Parallel(g3,g-4)
    c: Coincident(g0,g-5)
    c: Coincident(g2,g-6)
FEATURE [Part::Extrusion] Extrude008  label="Extrude buco oled"
  Base = -> Sketch012
  Dir = (0,-1,2e-16)
  DirMode = 2
  FaceMakerClass = Part::FaceMakerBullseye
  FaceMakerMode = 3
  LengthFwd = 12.8
  LengthRev = 0
  Solid = true
  Symmetric = true
FEATURE [Sketcher::SketchObject] Sketch013  label="buco pompa"
  ArcFitTolerance = 1e-06
  AttachmentSupport = -> [XZ_Plane]
  ExternalGeometry = -> [Sketch]
  FullyConstrained = true
  MakeInternals = false
  MapMode = 5
  Placement = pos=(0,0,0) rot=(1,0,0;1.5708rad)
  sketch-geometry (8):
    g0: LineSegment StartX=-82.8 StartY=-10.4 StartZ=0 EndX=-82.8 EndY=-9.6 EndZ=0
    g1: LineSegment StartX=-82.8 StartY=-9.6 StartZ=0 EndX=-67.9 EndY=-9.6 EndZ=0
    g2: LineSegment StartX=-67.9 StartY=-9.6 StartZ=0 EndX=-67.9 EndY=6 EndZ=0
    g3: LineSegment StartX=-67.9 StartY=6 StartZ=0 EndX=-65.9 EndY=6 EndZ=0
    g4: LineSegment StartX=-65.9 StartY=6 StartZ=0 EndX=-65.9 EndY=-1.7 EndZ=0
    g5: LineSegment StartX=-65.9 StartY=-1.7 StartZ=0 EndX=-57.2 EndY=-1.7 EndZ=0
    g6: LineSegment StartX=-57.2 StartY=-1.7 StartZ=0 EndX=-57.2 EndY=-10.4 EndZ=0
    g7: LineSegment StartX=-57.2 StartY=-10.4 StartZ=0 EndX=-82.8 EndY=-10.4 EndZ=0
  constraints (22):
    c: Vertical(g0)
    c: Coincident(g1,g0)
    c: Horizontal(g1)
    c: Coincident(g2,g1)
    c: Vertical(g2)
    c: Coincident(g3,g2)
    c: Horizontal(g3)
    c: Coincident(g4,g3)
    c: Vertical(g4)
    c: Coincident(g5,g4)
    c: Horizontal(g5)
    c: Coincident(g6,g5)
    c: Vertical(g6)
    c: Coincident(g7,g6)
    c: Coincident(g7,g0)
    c: DistanceY(g0,g0) = 0.8
    c: DistanceY(g6,g6) = 8.7
    c: DistanceX(g1,g1) = 14.9
    c: DistanceX(g3,g3) = 2
    c: Coincident(g0,g-4)
    c: DistanceY(g2,g-6) = 0
    c: Coincident(g6,g-5)
FEATURE [Part::Extrusion] Extrude009  label="Extrude buco pompa"
  Base = -> Sketch013
  Dir = (0,-1,2e-16)
  DirMode = 2
  FaceMakerClass = Part::FaceMakerBullseye
  FaceMakerMode = 3
  LengthFwd = 13.2
  LengthRev = 0
  Solid = true
  Symmetric = true
FEATURE [Sketcher::SketchObject] Sketch014  label="buco frontale"
  ArcFitTolerance = 1e-06
  AttachmentSupport = -> [XZ_Plane]
  ExternalGeometry = -> [Sketch]
  FullyConstrained = true
  MakeInternals = false
  MapMode = 5
  Placement = pos=(0,0,0) rot=(1,0,0;1.5708rad)
  sketch-geometry (10):
    g0: LineSegment StartX=0 StartY=0 StartZ=0 EndX=0 EndY=24.671 EndZ=0
    g1: LineSegment StartX=0 StartY=24.671 StartZ=0 EndX=-4 EndY=24.671 EndZ=0
    g2: LineSegment StartX=-4 StartY=24.671 StartZ=0 EndX=-4 EndY=16 EndZ=0
    g3: LineSegment StartX=-4 StartY=16 StartZ=0 EndX=-2.4 EndY=16 EndZ=0
    g4: LineSegment StartX=-2.4 StartY=16 StartZ=0 EndX=-2.4 EndY=10 EndZ=0
    g5: LineSegment StartX=-2.4 StartY=10 StartZ=0 EndX=-12 EndY=10 EndZ=0
    g6: LineSegment StartX=-12 StartY=10 StartZ=0 EndX=-12 EndY=6 EndZ=0
    g7: LineSegment StartX=-12 StartY=6 StartZ=0 EndX=-2.4 EndY=6 EndZ=0
    g8: LineSegment StartX=-2.4 StartY=6 StartZ=0 EndX=-2.4 EndY=0 EndZ=0
    g9: LineSegment StartX=-2.4 StartY=0 StartZ=0 EndX=0 EndY=0 EndZ=0
  constraints (29):
    c: Vertical(g0)
    c: Coincident(g1,g0)
    c: Horizontal(g1)
    c: Coincident(g2,g1)
    c: Vertical(g2)
    c: Coincident(g3,g2)
    c: Horizontal(g3)
    c: Coincident(g4,g3)
    c: Vertical(g4)
    c: Coincident(g5,g4)
    c: Horizontal(g5)
    c: Coincident(g6,g5)
    c: Vertical(g6)
    c: Coincident(g7,g6)
    c: Coincident(g8,g7)
    c: Vertical(g8)
    c: Coincident(g9,g8)
    c: Coincident(g9,g0)
    c: Horizontal(g9)
    c: DistanceY(g0,g0) = 24.671
    c: Horizontal(g7)
    c: DistanceY(g6,g6) = 4
    c: DistanceY(g4,g4) = 6
    c: DistanceX(g9,g9) = 2.4
    c: Coincident(g0,g-1)
    c: DistanceY(g-3,g7) = 0
    c: DistanceX(g8,g4) = 0
    c: DistanceX(g-3,g1) = 0
    c: DistanceX(g6,g-3) = 8
FEATURE [Part::Extrusion] Extrude010  label="Extrude buco frontale"
  Base = -> Sketch014
  Dir = (0,-1,2e-16)
  DirMode = 2
  FaceMakerClass = Part::FaceMakerBullseye
  FaceMakerMode = 3
  LengthFwd = 11.2
  LengthRev = 0
  Solid = true
  Symmetric = true
FEATURE [Sketcher::SketchObject] Sketch015  label="guida rail"
  ArcFitTolerance = 1e-06
  AttachmentSupport = -> [XZ_Plane]
  ExternalGeometry = -> [Sketch]
  FullyConstrained = true
  MakeInternals = false
  MapMode = 5
  Placement = pos=(0,0,0) rot=(1,0,0;1.5708rad)
  sketch-geometry (4):
    g0: LineSegment StartX=-100.8 StartY=43.2 StartZ=0 EndX=-44.6 EndY=43.2 EndZ=0
    g1: LineSegment StartX=-44.6 StartY=43.2 StartZ=0 EndX=-44.6 EndY=41.2 EndZ=0
    g2: LineSegment StartX=-44.6 StartY=41.2 StartZ=0 EndX=-100.8 EndY=41.2 EndZ=0
    g3: LineSegment StartX=-100.8 StartY=41.2 StartZ=0 EndX=-100.8 EndY=43.2 EndZ=0
  constraints (9):
    c: Horizontal(g0)
    c: Coincident(g1,g0)
    c: Coincident(g2,g1)
    c: Coincident(g3,g2)
    c: Coincident(g3,g0)
    c: Vertical(g3)
    c: Coincident(g2,g-3)
    c: Coincident(g1,g-3)
    c: Coincident(g0,g-4)
FEATURE [Part::Extrusion] Extrude011  label="Extrude guida rail"
  Base = -> Sketch015
  Dir = (0,-1,2e-16)
  DirMode = 2
  FaceMakerClass = Part::FaceMakerBullseye
  FaceMakerMode = 3
  LengthFwd = 9
  LengthRev = 0
  Solid = true
  Symmetric = true
FEATURE [Sketcher::SketchObject] Sketch016  label="guide per coperture laterali"
  ArcFitTolerance = 1e-06
  AttachmentSupport = -> [XZ_Plane]
  ExternalGeometry = -> [Sketch]
  FullyConstrained = true
  MakeInternals = false
  MapMode = 5
  Placement = pos=(0,0,0) rot=(1,0,0;1.5708rad)
  sketch-geometry (14):
    g0: Circle CenterX=-5.6 CenterY=7.6 CenterZ=0 NormalX=0 NormalY=0 NormalZ=1 AngleXU=0 Radius=1.6
    g1: Circle CenterX=-5.6 CenterY=7.6 CenterZ=0 NormalX=0 NormalY=0 NormalZ=1 AngleXU=0 Radius=4
    g2: Circle CenterX=-5.6 CenterY=34.8 CenterZ=0 NormalX=0 NormalY=0 NormalZ=1 AngleXU=0 Radius=1.6
    g3: Circle CenterX=-5.6 CenterY=34.8 CenterZ=0 NormalX=0 NormalY=0 NormalZ=1 AngleXU=0 Radius=4
    g4: Circle CenterX=-184.08 CenterY=34.8 CenterZ=0 NormalX=0 NormalY=0 NormalZ=1 AngleXU=0 Radius=1.6
    g5: Circle CenterX=-184.08 CenterY=34.8 CenterZ=0 NormalX=0 NormalY=0 NormalZ=1 AngleXU=0 Radius=4
    g6: Circle CenterX=-179.305 CenterY=-76.8316 CenterZ=0 NormalX=0 NormalY=0 NormalZ=1 AngleXU=0 Radius=1.6
    g7: Circle CenterX=-179.305 CenterY=-76.8316 CenterZ=0 NormalX=0 NormalY=0 NormalZ=1 AngleXU=0 Radius=4
    g8: Circle CenterX=-213.443 CenterY=-76.8316 CenterZ=0 NormalX=0 NormalY=0 NormalZ=1 AngleXU=0 Radius=1.6
    g9: Circle CenterX=-213.443 CenterY=-76.8316 CenterZ=0 NormalX=0 NormalY=0 NormalZ=1 AngleXU=0 Radius=4
    g10: Circle CenterX=-78.51 CenterY=7.6 CenterZ=0 NormalX=0 NormalY=0 NormalZ=1 AngleXU=0 Radius=1.6
    g11: Circle CenterX=-78.51 CenterY=7.6 CenterZ=0 NormalX=0 NormalY=0 NormalZ=1 AngleXU=0 Radius=4
    g12: Circle CenterX=-78.51 CenterY=34.8 CenterZ=0 NormalX=0 NormalY=0 NormalZ=1 AngleXU=0 Radius=1.6
    g13: Circle CenterX=-78.51 CenterY=34.8 CenterZ=0 NormalX=0 NormalY=0 NormalZ=1 AngleXU=0 Radius=4
  constraints (35):
    c: Diameter(g0) = 3.2
    c: Diameter(g1) = 8
    c: Coincident(g0,g1)
    c: Diameter(g2) = 3.2
    c: Diameter(g3) = 8
    c: Coincident(g3,g2)
    c: Tangent(g2,g-7)
    c: Diameter(g4) = 3.2
    c: Diameter(g5) = 8
    c: Coincident(g5,g4)
    c: Tangent(g4,g-7)
    c: Tangent(g4,g-8)
    c: Diameter(g6) = 3.2
    c: Diameter(g7) = 8
    c: Coincident(g7,g6)
    c: Tangent(g6,g-9)
    c: Tangent(g6,g-10)
    c: Diameter(g8) = 3.2
    c: Diameter(g9) = 8
    c: Coincident(g9,g8)
    c: Tangent(g8,g-10)
    c: Tangent(g8,g-11)
    c: Diameter(g10) = 3.2
    c: Diameter(g11) = 8
    c: Diameter(g12) = 3.2
    c: Diameter(g13) = 8
    c: Coincident(g12,g13)
    c: Coincident(g10,g11)
    c: Tangent(g12,g-7)
    c: DistanceX(g12,g10) = 0
    c: Tangent(g2,g-6)
    c: Tangent(g0,g-6)
    c: Tangent(g0,g-3)
    c: Tangent(g10,g-3)
    c: Tangent(g10,g-4)
FEATURE [Part::Extrusion] Extrude012  label="extrude guide per coperture laterali"
  Base = -> Sketch016
  Dir = (0,-1,2e-16)
  DirMode = 2
  FaceMakerClass = Part::FaceMakerBullseye
  FaceMakerMode = 3
  LengthFwd = 25.2
  LengthRev = 0
  Solid = true
  Symmetric = true
FEATURE [Sketcher::SketchObject] Sketch017  label="supporto CAM"
  ArcFitTolerance = 1e-06
  AttachmentSupport = -> [XZ_Plane]
  ExternalGeometry = -> [Sketch]
  FullyConstrained = true
  MakeInternals = false
  MapMode = 5
  Placement = pos=(0,0,0) rot=(1,0,0;1.5708rad)
  sketch-geometry (6):
    g0: LineSegment StartX=-2.4 StartY=48 StartZ=0 EndX=-2.4 EndY=41.2 EndZ=0
    g1: LineSegment StartX=-2.4 StartY=48 StartZ=0 EndX=-34 EndY=48 EndZ=0
    g2: LineSegment StartX=-34 StartY=48 StartZ=0 EndX=-34 EndY=46.72 EndZ=0
    g3: LineSegment StartX=-34 StartY=46.72 StartZ=0 EndX=-36 EndY=46.72 EndZ=0
    g4: LineSegment StartX=-36 StartY=46.72 StartZ=0 EndX=-36 EndY=41.2 EndZ=0
    g5: LineSegment StartX=-36 StartY=41.2 StartZ=0 EndX=-2.4 EndY=41.2 EndZ=0
  constraints (15):
    c: Coincident(g1,g0)
    c: Horizontal(g1)
    c: Coincident(g2,g1)
    c: Vertical(g2)
    c: Coincident(g3,g2)
    c: Horizontal(g3)
    c: Coincident(g4,g3)
    c: Coincident(g5,g4)
    c: DistanceX(g1,g0) = 31.6
    c: Coincident(g5,g0)
    c: Vertical(g4)
    c: DistanceY(g2,g1) = 1.28
    c: Coincident(g0,g-3)
    c: Coincident(g0,g-3)
    c: Coincident(g4,g-4)
FEATURE [Part::Extrusion] Extrude013  label="Extrude supporto CAM"
  Base = -> Sketch017
  Dir = (0,-1,2e-16)
  DirMode = 2
  FaceMakerClass = Part::FaceMakerBullseye
  FaceMakerMode = 3
  LengthFwd = 17.8
  LengthRev = 0
  Solid = true
  Symmetric = true
FEATURE [Sketcher::SketchObject] Sketch018  label="Scavo CAM"
  ArcFitTolerance = 1e-06
  AttachmentSupport = -> [YZ_Plane]
  ExternalGeometry = -> [Sketch]
  FullyConstrained = true
  MakeInternals = false
  MapMode = 5
  Placement = pos=(0,0,0) rot=(0.57735,0.57735,0.57735;2.0944rad)
  sketch-geometry (4):
    g0: LineSegment StartX=-7.73 StartY=48 StartZ=0 EndX=7.73 EndY=48 EndZ=0
    g1: LineSegment [constr] StartX=1.07e-14 StartY=48 StartZ=0 EndX=0 EndY=43.5155 EndZ=0
    g2: ArcOfCircle CenterX=9e-15 CenterY=52.42 CenterZ=0 NormalX=0 NormalY=0 NormalZ=1 AngleXU=0 Radius=8.90445 StartAngle=3.66102 EndAngle=5.76376
    g3: Circle [constr] CenterX=9e-15 CenterY=52.42 CenterZ=0 NormalX=0 NormalY=0 NormalZ=1 AngleXU=0 Radius=8.9
  constraints (13):
    c: Horizontal(g0)
    c: DistanceY(g-3,g0) = 0
    c: DistanceX(g0,g0) = 15.46
    c: DistanceX(g0,g-3) = 7.73
    c: DistanceX(g-3) = 0
    c: Coincident(g1,g-3)
    c: PointOnObject(g1,g-2)
    c: Coincident(g2,g0)
    c: Coincident(g2,g0)
    c: PointOnObject(g1,g2)
    c: Diameter(g3) = 17.8
    c: DistanceY(g1,g3) = 4.42
    c: Coincident(g2,g3)
FEATURE [Part::Extrusion] Extrude014  label="Extrude Scavo CAM"
  Base = -> Sketch018
  Dir = (1,0,0)
  DirMode = 2
  FaceMakerClass = Part::FaceMakerBullseye
  FaceMakerMode = 3
  LengthFwd = -34
  LengthRev = 0
  Solid = true
  Symmetric = false
FEATURE [Sketcher::SketchObject] Sketch019  label="scavo rumble"
  ArcFitTolerance = 1e-06
  AttachmentSupport = -> [XZ_Plane]
  ExternalGeometry = -> [Sketch]
  FullyConstrained = true
  MakeInternals = false
  MapMode = 5
  Placement = pos=(0,0,0) rot=(1,0,0;1.5708rad)
  sketch-geometry (6):
    g0: LineSegment StartX=-164.575 StartY=-24.3786 StartZ=0 EndX=-159.439 EndY=-26.0473 EndZ=0
    g1: LineSegment StartX=-159.439 StartY=-26.0473 StartZ=0 EndX=-166.547 EndY=-47.9216 EndZ=0
    g2: LineSegment StartX=-166.547 StartY=-47.9216 StartZ=0 EndX=-171.682 EndY=-46.2529 EndZ=0
    g3: LineSegment StartX=-171.682 StartY=-46.2529 StartZ=0 EndX=-164.575 EndY=-24.3786 EndZ=0
    g4: LineSegment [constr] StartX=-145.51 StartY=22 StartZ=0 EndX=-160.961 EndY=-25.5528 EndZ=0
    g5: LineSegment [constr] StartX=-159.439 StartY=-26.0473 StartZ=0 EndX=-160.961 EndY=-25.5528 EndZ=0
  constraints (17):
    c: Coincident(g1,g0)
    c: Coincident(g2,g1)
    c: Coincident(g3,g2)
    c: Coincident(g3,g0)
    c: Parallel(g3,g-3)
    c: Parallel(g3,g1)
    c: Perpendicular(g3,g0)
    c: Perpendicular(g2,g3)
    c: Distance(g2,g0) = 23
    c: Parallel(g4,g-3)
    c: Distance(g4) = 50
    c: Coincident(g4,g-3)
    c: Parallel(g5,g0)
    c: Distance(g5) = 1.6
    c: Coincident(g5,g0)
    c: Distance(g5,g0) = 3.8
    c: Coincident(g5,g4)
FEATURE [Part::Extrusion] Extrude015  label="scavo rumble001"
  Base = -> Sketch019
  Dir = (0,-1,2e-16)
  DirMode = 2
  FaceMakerClass = Part::FaceMakerBullseye
  FaceMakerMode = 3
  LengthFwd = 21
  LengthRev = 0
  Solid = true
  Symmetric = true
FEATURE [Sketcher::SketchObject] Sketch020  label="fermo rumble"
  ArcFitTolerance = 1e-06
  AttachmentSupport = -> [XZ_Plane]
  ExternalGeometry = -> [Sketch019,Sketch]
  FullyConstrained = true
  MakeInternals = false
  MapMode = 5
  Placement = pos=(0,0,0) rot=(1,0,0;1.5708rad)
  sketch-geometry (16):
    g0: LineSegment [constr] StartX=-166.709 StartY=-43.2425 StartZ=0 EndX=-168.068 EndY=-47.4271 EndZ=0
    g1: LineSegment [constr] StartX=-168.068 StartY=-47.4271 StartZ=0 EndX=-166.547 EndY=-47.9216 EndZ=0
    g2: LineSegment StartX=-168.121 StartY=-40.4703 StartZ=0 EndX=-166.029 EndY=-41.1502 EndZ=0
    g3: LineSegment StartX=-166.029 StartY=-41.1502 StartZ=0 EndX=-166.709 EndY=-43.2425 EndZ=0
    g4: LineSegment StartX=-166.709 StartY=-43.2425 StartZ=0 EndX=-168.801 EndY=-42.5626 EndZ=0
    g5: LineSegment StartX=-168.801 StartY=-42.5626 StartZ=0 EndX=-168.121 EndY=-40.4703 EndZ=0
    g6: LineSegment StartX=-167.627 StartY=-38.9486 StartZ=0 EndX=-164.203 EndY=-40.0611 EndZ=0
    g7: LineSegment StartX=-164.203 StartY=-40.0611 StartZ=0 EndX=-165.81 EndY=-45.0066 EndZ=0
    g8: LineSegment StartX=-165.81 StartY=-45.0066 StartZ=0 EndX=-169.234 EndY=-43.8941 EndZ=0
    g9: LineSegment StartX=-170.261 StartY=-41.878 StartZ=0 EndX=-169.643 EndY=-39.9759 EndZ=0
    g10: LineSegment [constr] StartX=-169.643 StartY=-39.9759 StartZ=0 EndX=-169.148 EndY=-38.4542 EndZ=0
    g11: LineSegment [constr] StartX=-169.148 StartY=-38.4542 StartZ=0 EndX=-167.627 EndY=-38.9486 EndZ=0
    g12: ArcOfCircle CenterX=-168.739 CenterY=-42.3724 CenterZ=0 NormalX=0 NormalY=0 NormalZ=1 AngleXU=0 Radius=1.6 StartAngle=2.82743 EndAngle=4.39823
    g13: GeomPoint [constr] X=-170.755 Y=-43.3997 Z=0
    g14: ArcOfCircle CenterX=-168.121 CenterY=-40.4703 CenterZ=0 NormalX=0 NormalY=0 NormalZ=1 AngleXU=0 Radius=1.6 StartAngle=1.25664 EndAngle=2.82743
    g15: GeomPoint [constr] X=-169.148 Y=-38.4542 Z=0
  constraints (42):
    c: Parallel(g0,g-4)
    c: Distance(g0) = 4.4
    c: Coincident(g1,g0)
    c: Perpendicular(g0,g1)
    c: Distance(g1) = 1.6
    c: Coincident(g1,g-5)
    c: Coincident(g3,g2)
    c: Coincident(g4,g3)
    c: Coincident(g5,g4)
    c: Coincident(g5,g2)
    c: Parallel(g3,g-4)
    c: Parallel(g3,g5)
    c: Perpendicular(g2,g3)
    c: Parallel(g4,g2)
    c: Distance(g2) = 2.2
    c: Distance(g3) = 2.2
    c: Coincident(g7,g6)
    c: Coincident(g8,g7)
    c: Parallel(g7,g-4)
    c: Parallel(g7,g9)
    c: Perpendicular(g6,g7)
    c: Parallel(g6,g8)
    c: Distance(g6,g15) = 5.2
    c: Distance(g7) = 5.2
    c: Coincident(g11,g10)
    c: Parallel(g10,g9)
    c: Parallel(g11,g6)
    c: Distance(g10) = 1.6
    c: Distance(g11) = 1.6
    c: Coincident(g10,g15)
    c: Distance(g11,g2) = 1.6
    c: Distance(g2,g10) = 1.6
    c: PointOnObject(g13,g8)
    c: PointOnObject(g13,g9)
    c: Tangent(g8,g12) = 1.5708
    c: Tangent(g9,g12) = 1.5708
    c: PointOnObject(g15,g9)
    c: Tangent(g6,g14) = 1.5708
    c: Tangent(g9,g14) = 1.5708
    c: Equal(g12,g14)
    c: Coincident(g6,g11)
    c: Coincident(g3,g0)
FEATURE [Part::Extrusion] Extrude016  label="Extrude fermo rumble"
  Base = -> Sketch020
  Dir = (0,-1,2e-16)
  DirMode = 2
  FaceMakerClass = Part::FaceMakerBullseye
  FaceMakerMode = 3
  LengthFwd = 25.2
  LengthRev = 0
  Solid = true
  Symmetric = true
FEATURE [Sketcher::SketchObject] Sketch021  label="perno fermo rumble001"
  ArcFitTolerance = 1e-06
  AttachmentSupport = -> [XZ_Plane001]
  FullyConstrained = true
  MakeInternals = false
  MapMode = 5
  Placement = pos=(0,0,0) rot=(1,0,0;1.5708rad)
  sketch-geometry (16):
    g0: LineSegment StartX=0 StartY=0.45 StartZ=0 EndX=0 EndY=1.55 EndZ=0
    g1: LineSegment StartX=0.45 StartY=2 StartZ=0 EndX=1.55 EndY=2 EndZ=0
    g2: LineSegment StartX=2 StartY=1.55 StartZ=0 EndX=2 EndY=0.45 EndZ=0
    g3: LineSegment StartX=1.55 StartY=0 StartZ=0 EndX=0.45 EndY=0 EndZ=0
    g4: ArcOfCircle [constr] CenterX=0.45 CenterY=1.55 CenterZ=0 NormalX=0 NormalY=0 NormalZ=1 AngleXU=0 Radius=0.45 StartAngle=1.5708 EndAngle=3.14159
    g5: GeomPoint [constr] X=0 Y=2 Z=0
    g6: LineSegment StartX=0.45 StartY=2 StartZ=0 EndX=0 EndY=1.55 EndZ=0
    g7: ArcOfCircle [constr] CenterX=1.55 CenterY=1.55 CenterZ=0 NormalX=0 NormalY=0 NormalZ=1 AngleXU=0 Radius=0.45 StartAngle=0 EndAngle=1.5708
    g8: GeomPoint [constr] X=2 Y=2 Z=0
    g9: LineSegment StartX=2 StartY=1.55 StartZ=0 EndX=1.55 EndY=2 EndZ=0
    g10: ArcOfCircle [constr] CenterX=1.55 CenterY=0.45 CenterZ=0 NormalX=0 NormalY=0 NormalZ=1 AngleXU=0 Radius=0.45 StartAngle=4.71239 EndAngle=6.28319
    g11: GeomPoint [constr] X=2 Y=0 Z=0
    g12: LineSegment StartX=1.55 StartY=0 StartZ=0 EndX=2 EndY=0.45 EndZ=0
    g13: ArcOfCircle [constr] CenterX=0.45 CenterY=0.45 CenterZ=0 NormalX=0 NormalY=0 NormalZ=1 AngleXU=0 Radius=0.45 StartAngle=3.14159 EndAngle=4.71239
    g14: GeomPoint [constr] X=0 Y=0 Z=0
    g15: LineSegment StartX=0 StartY=0.45 StartZ=0 EndX=0.45 EndY=0 EndZ=0
  constraints (35):
    c: Coincident(g14,g-1)
    c: PointOnObject(g5,g-2)
    c: Horizontal(g1)
    c: Vertical(g2)
    c: Horizontal(g3)
    c: DistanceX(g5,g8) = 2
    c: DistanceY(g11,g8) = 2
    c: PointOnObject(g5,g0)
    c: PointOnObject(g5,g1)
    c: Tangent(g0,g4) = 1.5708
    c: Tangent(g1,g4) = 1.5708
    c: Coincident(g6,g0)
    c: Coincident(g6,g1)
    c: PointOnObject(g8,g2)
    c: PointOnObject(g8,g1)
    c: Tangent(g2,g7) = 1.5708
    c: Tangent(g1,g7) = 1.5708
    c: Coincident(g9,g2)
    c: Coincident(g9,g1)
    c: PointOnObject(g11,g2)
    c: PointOnObject(g11,g3)
    c: Tangent(g2,g10) = 1.5708
    c: Tangent(g3,g10) = 1.5708
    c: Coincident(g12,g2)
    c: Coincident(g12,g3)
    c: PointOnObject(g14,g0)
    c: PointOnObject(g14,g3)
    c: Tangent(g0,g13) = 1.5708
    c: Tangent(g3,g13) = 1.5708
    c: Coincident(g15,g0)
    c: Coincident(g15,g3)
    c: Equal(g6,g9)
    c: Equal(g9,g12)
    c: Equal(g12,g15)
    c: DistanceX(g14,g3) = 0.45
FEATURE [Sketcher::SketchObject] Sketch022  label="fori per M3x5(OD)x6(L)"
  ArcFitTolerance = 1e-06
  AttachmentSupport = -> [XZ_Plane]
  ExternalGeometry = -> [Sketch016]
  FullyConstrained = true
  MakeInternals = false
  MapMode = 5
  Placement = pos=(0,0,0) rot=(1,0,0;1.5708rad)
  sketch-geometry (7):
    g0: Circle CenterX=-5.6 CenterY=34.8 CenterZ=0 NormalX=0 NormalY=0 NormalZ=1 AngleXU=0 Radius=2.5
    g1: Circle CenterX=-5.6 CenterY=7.6 CenterZ=0 NormalX=0 NormalY=0 NormalZ=1 AngleXU=0 Radius=2.5
    g2: Circle CenterX=-78.51 CenterY=34.8 CenterZ=0 NormalX=0 NormalY=0 NormalZ=1 AngleXU=0 Radius=2.5
    g3: Circle CenterX=-78.51 CenterY=7.6 CenterZ=0 NormalX=0 NormalY=0 NormalZ=1 AngleXU=0 Radius=2.5
    g4: Circle CenterX=-184.08 CenterY=34.8 CenterZ=0 NormalX=0 NormalY=0 NormalZ=1 AngleXU=0 Radius=2.5
    g5: Circle CenterX=-179.305 CenterY=-76.8316 CenterZ=0 NormalX=0 NormalY=0 NormalZ=1 AngleXU=0 Radius=2.5
    g6: Circle CenterX=-213.443 CenterY=-76.8316 CenterZ=0 NormalX=0 NormalY=0 NormalZ=1 AngleXU=0 Radius=2.5
  constraints (14):
    c: Diameter(g0) = 5
    c: Diameter(g1) = 5
    c: Diameter(g2) = 5
    c: Diameter(g3) = 5
    c: Diameter(g4) = 5
    c: Diameter(g5) = 5
    c: Diameter(g6) = 5
    c: Coincident(g0,g-8)
    c: Coincident(g1,g-9)
    c: Coincident(g2,g-6)
    c: Coincident(g3,g-7)
    c: Coincident(g4,g-5)
    c: Coincident(g5,g-4)
    c: Coincident(g6,g-3)
FEATURE [Part::Extrusion] Extrude018  label="Extrude fori M3x5x6 - dx"
  Base = -> Sketch022
  Dir = (0,-1,2e-16)
  DirMode = 2
  FaceMakerClass = Part::FaceMakerBullseye
  FaceMakerMode = 3
  LengthFwd = 6.2
  LengthRev = 0
  Placement = pos=(0,-9.5,0) rot=(0,0,1;0rad)
  Solid = true
  Symmetric = true
FEATURE [Part::Extrusion] Extrude019  label="Extrude fori M3x5x6 - sx"
  Base = -> Sketch022
  Dir = (0,-1,2e-16)
  DirMode = 2
  FaceMakerClass = Part::FaceMakerBullseye
  FaceMakerMode = 3
  LengthFwd = 6.2
  LengthRev = 0
  Placement = pos=(0,9.5,0) rot=(0,0,1;0rad)
  Solid = true
  Symmetric = true
FEATURE [Sketcher::SketchObject] Sketch023  label="foro anteriore M3x5x6"
  ArcFitTolerance = 1e-06
  AttachmentSupport = -> [YZ_Plane]
  FullyConstrained = true
  MakeInternals = false
  MapMode = 5
  Placement = pos=(0,0,0) rot=(0.57735,0.57735,0.57735;2.0944rad)
  sketch-geometry (2):
    g0: LineSegment [constr] StartX=0 StartY=0 StartZ=0 EndX=0 EndY=38.6 EndZ=0
    g1: Circle CenterX=0 CenterY=38.6 CenterZ=0 NormalX=0 NormalY=0 NormalZ=1 AngleXU=0 Radius=2.5
  constraints (5):
    c: Coincident(g0,g-1)
    c: PointOnObject(g0,g-2)
    c: DistanceY(g0,g0) = 38.6
    c: Diameter(g1) = 5
    c: Coincident(g1,g0)
FEATURE [Part::Extrusion] Extrude020  label="Extrude foro anteriore M3x5x6"
  Base = -> Sketch023
  Dir = (1,0,0)
  DirMode = 2
  FaceMakerClass = Part::FaceMakerBullseye
  FaceMakerMode = 3
  LengthFwd = -6.2
  LengthRev = 0
  Solid = true
  Symmetric = false
FEATURE [Sketcher::SketchObject] Sketch024  label="fori per viti frontale"
  ArcFitTolerance = 1e-06
  AttachmentSupport = -> [YZ_Plane]
  FullyConstrained = true
  MakeInternals = false
  MapMode = 5
  Placement = pos=(0,0,0) rot=(0.57735,0.57735,0.57735;2.0944rad)
  sketch-geometry (9):
    g0: LineSegment [constr] StartX=-10.3 StartY=30.721 StartZ=0 EndX=10.3 EndY=30.721 EndZ=0
    g1: LineSegment [constr] StartX=10.3 StartY=30.721 StartZ=0 EndX=10.3 EndY=10.121 EndZ=0
    g2: LineSegment [constr] StartX=10.3 StartY=10.121 StartZ=0 EndX=-10.3 EndY=10.121 EndZ=0
    g3: LineSegment [constr] StartX=-10.3 StartY=10.121 StartZ=0 EndX=-10.3 EndY=30.721 EndZ=0
    g4: LineSegment [constr] StartX=0 StartY=0 StartZ=0 EndX=0 EndY=10.121 EndZ=0
    g5: Circle CenterX=-10.3 CenterY=30.721 CenterZ=0 NormalX=0 NormalY=0 NormalZ=1 AngleXU=0 Radius=2
    g6: Circle CenterX=10.3 CenterY=30.721 CenterZ=0 NormalX=0 NormalY=0 NormalZ=1 AngleXU=0 Radius=2
    g7: Circle CenterX=-10.3 CenterY=10.121 CenterZ=0 NormalX=0 NormalY=0 NormalZ=1 AngleXU=0 Radius=2
    g8: Circle CenterX=10.3 CenterY=10.121 CenterZ=0 NormalX=0 NormalY=0 NormalZ=1 AngleXU=0 Radius=2
  constraints (22):
    c: Horizontal(g0)
    c: Coincident(g1,g0)
    c: Vertical(g1)
    c: Coincident(g2,g1)
    c: Horizontal(g2)
    c: Coincident(g3,g2)
    c: Coincident(g3,g0)
    c: Vertical(g3)
    c: DistanceX(g0,g0) = 20.6
    c: DistanceY(g3,g3) = 20.6
    c: Coincident(g4,g-1)
    c: PointOnObject(g4,g-2)
    c: DistanceY(g4,g4) = 10.121
    c: Symmetric(g2,g2,g4)
    c: Diameter(g5) = 4
    c: Diameter(g6) = 4
    c: Diameter(g7) = 4
    c: Diameter(g8) = 4
    c: Coincident(g5,g0)
    c: Coincident(g6,g0)
    c: Coincident(g7,g2)
    c: Coincident(g8,g1)
FEATURE [Part::Extrusion] Extrude021  label="Extrude fori per viti frontale"
  Base = -> Sketch024
  Dir = (1,0,0)
  DirMode = 2
  FaceMakerClass = Part::FaceMakerBullseye
  FaceMakerMode = 3
  LengthFwd = -2.4
  LengthRev = 0
  Solid = true
  Symmetric = false
FEATURE [Sketcher::SketchObject] Sketch025  label="foro per filo CAM"
  ArcFitTolerance = 1e-06
  AttachmentSupport = -> [XZ_Plane]
  ExternalGeometry = -> [Sketch]
  FullyConstrained = true
  MakeInternals = false
  MapMode = 5
  Placement = pos=(0,0,0) rot=(1,0,0;1.5708rad)
  sketch-geometry (4):
    g0: LineSegment StartX=-44.6 StartY=41.2 StartZ=0 EndX=-44.6 EndY=36.4 EndZ=0
    g1: LineSegment StartX=-44.6 StartY=36.4 StartZ=0 EndX=-54.6 EndY=36.4 EndZ=0
    g2: LineSegment StartX=-54.6 StartY=36.4 StartZ=0 EndX=-50.4 EndY=41.2 EndZ=0
    g3: LineSegment StartX=-50.4 StartY=41.2 StartZ=0 EndX=-44.6 EndY=41.2 EndZ=0
  constraints (11):
    c: Vertical(g0)
    c: Coincident(g1,g0)
    c: Horizontal(g1)
    c: Coincident(g2,g1)
    c: Coincident(g3,g2)
    c: Coincident(g3,g0)
    c: Horizontal(g3)
    c: Coincident(g0,g-3)
    c: DistanceY(g0,g-4) = 0
    c: DistanceX(g3,g3) = 5.8
    c: DistanceX(g1,g1) = 10
FEATURE [Part::Extrusion] Extrude022  label="Extrude foro per filo CAM dx"
  Base = -> Sketch025
  Dir = (0,-1,2e-16)
  DirMode = 2
  FaceMakerClass = Part::FaceMakerBullseye
  FaceMakerMode = 3
  LengthFwd = 4.9
  LengthRev = 0
  Placement = pos=(0,6.95,0) rot=(0,0,1;0rad)
  Solid = true
  Symmetric = true
FEATURE [Part::Extrusion] Extrude023  label="Extrude foro per filo CAM sx"
  Base = -> Sketch025
  Dir = (0,-1,2e-16)
  DirMode = 2
  FaceMakerClass = Part::FaceMakerBullseye
  FaceMakerMode = 3
  LengthFwd = 4.9
  LengthRev = 0
  Placement = pos=(0,-6.95,0) rot=(0,0,1;0rad)
  Solid = true
  Symmetric = true
FEATURE [Sketcher::SketchObject] Sketch026  label="foro sotto anteriore M3x5x6"
  ArcFitTolerance = 1e-06
  AttachmentSupport = -> [XY_Plane]
  FullyConstrained = true
  MakeInternals = false
  MapMode = 5
  sketch-geometry (2):
    g0: LineSegment [constr] StartX=0 StartY=0 StartZ=0 EndX=-16.5 EndY=0 EndZ=0
    g1: Circle CenterX=-16.5 CenterY=0 CenterZ=0 NormalX=0 NormalY=0 NormalZ=1 AngleXU=0 Radius=2.5
  constraints (5):
    c: Distance(g0) = 16.5
    c: Coincident(g0,g-1)
    c: PointOnObject(g0,g-1)
    c: Diameter(g1) = 5
    c: Coincident(g0,g1)
FEATURE [Sketcher::SketchObject] Sketch027  label="foro sotto posteriore M3x5x6"
  ArcFitTolerance = 1e-06
  AttachmentSupport = -> [XY_Plane]
  ExternalGeometry = -> [Sketch]
  FullyConstrained = true
  MakeInternals = false
  MapMode = 5
  sketch-geometry (2):
    g0: LineSegment [constr] StartX=-82.8 StartY=2e-16 StartZ=0 EndX=-71.3 EndY=2e-16 EndZ=0
    g1: Circle CenterX=-71.3 CenterY=2e-16 CenterZ=0 NormalX=0 NormalY=0 NormalZ=1 AngleXU=0 Radius=2.5
  constraints (5):
    c: Distance(g0) = 11.5
    c: Coincident(g0,g-3)
    c: PointOnObject(g0,g-3)
    c: Diameter(g1) = 5
    c: Coincident(g1,g0)
FEATURE [Sketcher::SketchObject] Sketch029  label="fori sotto impugnatura"
  ArcFitTolerance = 1e-06
  AttachmentSupport = -> [XY_Plane]
  ExternalGeometry = -> [Sketch]
  FullyConstrained = true
  MakeInternals = false
  MapMode = 5
  sketch-geometry (15):
    g0: LineSegment [constr] StartX=-175.232 StartY=-1.83e-14 StartZ=0 EndX=-191.232 EndY=0 EndZ=0
    g1: Circle CenterX=-191.232 CenterY=0 CenterZ=0 NormalX=0 NormalY=0 NormalZ=1 AngleXU=0 Radius=3.95
    g2: LineSegment [constr] StartX=-175.232 StartY=-1.83e-14 StartZ=0 EndX=-204.275 EndY=0 EndZ=0
    g3: LineSegment StartX=-204.275 StartY=3.525 StartZ=0 EndX=-204.275 EndY=-3.525 EndZ=0
    g4: LineSegment StartX=-205.4 StartY=-4.65 StartZ=0 EndX=-206.65 EndY=-4.65 EndZ=0
    g5: LineSegment StartX=-207.775 StartY=-3.525 StartZ=0 EndX=-207.775 EndY=3.525 EndZ=0
    g6: LineSegment StartX=-206.65 StartY=4.65 StartZ=0 EndX=-205.4 EndY=4.65 EndZ=0
    g7: ArcOfCircle CenterX=-206.65 CenterY=3.525 CenterZ=0 NormalX=0 NormalY=0 NormalZ=1 AngleXU=0 Radius=1.125 StartAngle=1.5708 EndAngle=3.14159
    g8: GeomPoint [constr] X=-207.775 Y=4.65 Z=0
    g9: ArcOfCircle CenterX=-205.4 CenterY=3.525 CenterZ=0 NormalX=0 NormalY=0 NormalZ=1 AngleXU=0 Radius=1.125 StartAngle=0 EndAngle=1.5708
    g10: GeomPoint [constr] X=-204.275 Y=4.65 Z=0
    g11: ArcOfCircle CenterX=-205.4 CenterY=-3.525 CenterZ=0 NormalX=0 NormalY=0 NormalZ=1 AngleXU=0 Radius=1.125 StartAngle=4.71239 EndAngle=6.28319
    g12: GeomPoint [constr] X=-204.275 Y=-4.65 Z=0
    g13: ArcOfCircle CenterX=-206.65 CenterY=-3.525 CenterZ=0 NormalX=0 NormalY=0 NormalZ=1 AngleXU=0 Radius=1.125 StartAngle=3.14159 EndAngle=4.71239
    g14: GeomPoint [constr] X=-207.775 Y=-4.65 Z=0
  constraints (35):
    c: Distance(g0) = 16
    c: Coincident(g0,g-3)
    c: PointOnObject(g0,g-1)
    c: Diameter(g1) = 7.9
    c: Coincident(g1,g0)
    c: Coincident(g2,g0)
    c: PointOnObject(g2,g-1)
    c: Vertical(g3)
    c: Horizontal(g4)
    c: Vertical(g5)
    c: Horizontal(g6)
    c: DistanceY(g12,g10) = 9.3
    c: DistanceX(g8,g10) = 3.5
    c: Symmetric(g10,g12,g2)
    c: PointOnObject(g8,g5)
    c: PointOnObject(g8,g6)
    c: Tangent(g5,g7) = 1.5708
    c: Tangent(g6,g7) = 1.5708
    c: PointOnObject(g10,g3)
    c: PointOnObject(g10,g6)
    c: Tangent(g3,g9) = 1.5708
    c: Tangent(g6,g9) = 1.5708
    c: PointOnObject(g12,g3)
    c: PointOnObject(g12,g4)
    c: Tangent(g3,g11) = 1.5708
    c: Tangent(g4,g11) = 1.5708
    c: PointOnObject(g14,g4)
    c: PointOnObject(g14,g5)
    c: Tangent(g4,g13) = 1.5708
    c: Tangent(g5,g13) = 1.5708
    c: Equal(g7,g9)
    c: Equal(g9,g11)
    c: Equal(g11,g13)
    c: DistanceX(g6,g6) = 1.25
    c: DistanceX(g-5,g5) = 6.8
FEATURE [Sketcher::SketchObject] Sketch030  label="fori superiori per solenoide e oled"
  ArcFitTolerance = 1e-06
  AttachmentSupport = -> [XY_Plane]
  ExternalGeometry = -> [Sketch]
  FullyConstrained = true
  MakeInternals = false
  MapMode = 5
  sketch-geometry (33):
    g0: LineSegment [constr] StartX=-181.6 StartY=1.12e-14 StartZ=0 EndX=-169.91 EndY=0 EndZ=0
    g1: LineSegment [constr] StartX=-169.91 StartY=0 StartZ=0 EndX=-169.91 EndY=-2.6 EndZ=0
    g2: LineSegment [constr] StartX=-169.91 StartY=0 StartZ=0 EndX=-169.91 EndY=2.6 EndZ=0
    g3: LineSegment StartX=-169.91 StartY=4.975 StartZ=0 EndX=-169.91 EndY=8.225 EndZ=0
    g4: LineSegment StartX=-167.535 StartY=10.6 StartZ=0 EndX=-167.285 EndY=10.6 EndZ=0
    g5: LineSegment StartX=-164.91 StartY=8.225 StartZ=0 EndX=-164.91 EndY=4.975 EndZ=0
    g6: LineSegment StartX=-167.285 StartY=2.6 StartZ=0 EndX=-167.535 EndY=2.6 EndZ=0
    g7: LineSegment StartX=-169.91 StartY=-4.975 StartZ=0 EndX=-169.91 EndY=-8.225 EndZ=0
    g8: LineSegment StartX=-167.535 StartY=-10.6 StartZ=0 EndX=-167.285 EndY=-10.6 EndZ=0
    g9: LineSegment StartX=-164.91 StartY=-8.225 StartZ=0 EndX=-164.91 EndY=-4.975 EndZ=0
    g10: LineSegment StartX=-167.285 StartY=-2.6 StartZ=0 EndX=-167.535 EndY=-2.6 EndZ=0
    g11: ArcOfCircle CenterX=-167.535 CenterY=8.225 CenterZ=0 NormalX=0 NormalY=0 NormalZ=1 AngleXU=0 Radius=2.375 StartAngle=1.5708 EndAngle=3.14159
    g12: GeomPoint [constr] X=-169.91 Y=10.6 Z=0
    g13: ArcOfCircle CenterX=-167.285 CenterY=8.225 CenterZ=0 NormalX=0 NormalY=0 NormalZ=1 AngleXU=0 Radius=2.375 StartAngle=0 EndAngle=1.5708
    g14: GeomPoint [constr] X=-164.91 Y=10.6 Z=0
    g15: ArcOfCircle CenterX=-167.285 CenterY=4.975 CenterZ=0 NormalX=0 NormalY=0 NormalZ=1 AngleXU=0 Radius=2.375 StartAngle=4.71239 EndAngle=6.28319
    g16: GeomPoint [constr] X=-164.91 Y=2.6 Z=0
    g17: ArcOfCircle CenterX=-167.535 CenterY=4.975 CenterZ=0 NormalX=0 NormalY=0 NormalZ=1 AngleXU=0 Radius=2.375 StartAngle=3.14159 EndAngle=4.71239
    g18: GeomPoint [constr] X=-169.91 Y=2.6 Z=0
    g19: ArcOfCircle CenterX=-167.535 CenterY=-4.975 CenterZ=0 NormalX=0 NormalY=0 NormalZ=1 AngleXU=0 Radius=2.375 StartAngle=1.5708 EndAngle=3.14159
    g20: GeomPoint [constr] X=-169.91 Y=-2.6 Z=0
    g21: ArcOfCircle CenterX=-167.285 CenterY=-4.975 CenterZ=0 NormalX=0 NormalY=0 NormalZ=1 AngleXU=0 Radius=2.375 StartAngle=0 EndAngle=1.5708
    g22: GeomPoint [constr] X=-164.91 Y=-2.6 Z=0
    g23: ArcOfCircle CenterX=-167.285 CenterY=-8.225 CenterZ=0 NormalX=0 NormalY=0 NormalZ=1 AngleXU=0 Radius=2.375 StartAngle=4.71239 EndAngle=6.28319
    g24: GeomPoint [constr] X=-164.91 Y=-10.6 Z=0
    g25: ArcOfCircle CenterX=-167.535 CenterY=-8.225 CenterZ=0 NormalX=0 NormalY=0 NormalZ=1 AngleXU=0 Radius=2.375 StartAngle=3.14159 EndAngle=4.71239
    g26: GeomPoint [constr] X=-169.91 Y=-10.6 Z=0
    g27: LineSegment [constr] StartX=-181.6 StartY=1.12e-14 StartZ=0 EndX=-152.209 EndY=0 EndZ=0
    g28: LineSegment [constr] StartX=-181.6 StartY=1.12e-14 StartZ=0 EndX=-130.41 EndY=0 EndZ=0
    g29: LineSegment [constr] StartX=-152.209 StartY=0 StartZ=0 EndX=-152.209 EndY=6.95 EndZ=0
    g30: LineSegment [constr] StartX=-130.41 StartY=0 StartZ=0 EndX=-130.41 EndY=-6.95 EndZ=0
    g31: Circle CenterX=-152.209 CenterY=6.95 CenterZ=0 NormalX=0 NormalY=0 NormalZ=1 AngleXU=0 Radius=2.1
    g32: Circle CenterX=-130.41 CenterY=-6.95 CenterZ=0 NormalX=0 NormalY=0 NormalZ=1 AngleXU=0 Radius=2.1
  constraints (79):
    c: Distance(g0) = 11.69
    c: PointOnObject(g0,g-1)
    c: Coincident(g-4,g0)
    c: Distance(g1) = 2.6
    c: Coincident(g1,g0)
    c: Vertical(g1)
    c: Distance(g2) = 2.6
    c: Coincident(g2,g0)
    c: Vertical(g2)
    c: Distance(g18,g12) = 8
    c: Coincident(g18,g2)
    c: Vertical(g3)
    c: Distance(g14,g12) = 5
    c: Horizontal(g4)
    c: Distance(g16,g14) = 8
    c: Vertical(g5)
    c: Distance(g26,g20) = 8
    c: Coincident(g20,g1)
    c: Vertical(g7)
    c: Distance(g26,g24) = 5
    c: Horizontal(g8)
    c: Distance(g24,g22) = 8
    c: Vertical(g9)
    c: PointOnObject(g12,g3)
    c: PointOnObject(g12,g4)
    c: Tangent(g3,g11) = 1.5708
    c: Tangent(g4,g11) = 1.5708
    c: PointOnObject(g14,g5)
    c: PointOnObject(g14,g4)
    c: Tangent(g5,g13) = 1.5708
    c: Tangent(g4,g13) = 1.5708
    c: PointOnObject(g16,g5)
    c: PointOnObject(g16,g6)
    c: Tangent(g5,g15) = 1.5708
    c: Tangent(g6,g15) = 1.5708
    c: PointOnObject(g18,g3)
    c: PointOnObject(g18,g6)
    c: Tangent(g3,g17) = 1.5708
    c: Tangent(g6,g17) = 1.5708
    c: Equal(g11,g13)
    c: Equal(g13,g15)
    c: Equal(g15,g17)
    c: DistanceX(g4,g4) = 0.25
    c: PointOnObject(g20,g7)
    c: PointOnObject(g20,g10)
    c: Tangent(g7,g19) = -1.5708
    c: Tangent(g10,g19) = -1.5708
    c: PointOnObject(g22,g9)
    c: PointOnObject(g22,g10)
    c: Tangent(g9,g21) = -1.5708
    c: Tangent(g10,g21) = -1.5708
    c: PointOnObject(g24,g9)
    c: PointOnObject(g24,g8)
    c: Tangent(g9,g23) = -1.5708
    c: Tangent(g8,g23) = -1.5708
    c: PointOnObject(g26,g8)
    c: PointOnObject(g26,g7)
    c: Tangent(g8,g25) = -1.5708
    c: Tangent(g7,g25) = -1.5708
    c: Equal(g19,g21)
    c: Equal(g21,g23)
    c: Equal(g23,g25)
    c: DistanceX(g10,g10) = 0.25
    c: Distance(g27) = 29.391
    c: Coincident(g27,g0)
    c: PointOnObject(g27,g-1)
    c: Distance(g28) = 51.19
    c: Coincident(g28,g0)
    c: PointOnObject(g28,g-1)
    c: Distance(g29) = 6.95
    c: Coincident(g29,g27)
    c: Vertical(g29)
    c: Distance(g30) = 6.95
    c: Coincident(g30,g28)
    c: Vertical(g30)
    c: Diameter(g31) = 4.2
    c: Diameter(g32) = 4.2
    c: Coincident(g32,g30)
    c: Coincident(g31,g29)
FEATURE [Sketcher::SketchObject] Sketch031  label="fori inferiori switch pompa"
  ArcFitTolerance = 1e-06
  AttachmentSupport = -> [XY_Plane]
  ExternalGeometry = -> [Sketch]
  FullyConstrained = true
  MakeInternals = false
  MapMode = 5
  sketch-geometry (4):
    g0: LineSegment [constr] StartX=-57.2 StartY=1.9e-15 StartZ=0 EndX=-62.45 EndY=1.9e-15 EndZ=0
    g1: LineSegment [constr] StartX=-62.45 StartY=3.25 StartZ=0 EndX=-62.45 EndY=-3.25 EndZ=0
    g2: Circle CenterX=-62.45 CenterY=3.25 CenterZ=0 NormalX=0 NormalY=0 NormalZ=1 AngleXU=0 Radius=1.6
    g3: Circle CenterX=-62.45 CenterY=-3.25 CenterZ=0 NormalX=0 NormalY=0 NormalZ=1 AngleXU=0 Radius=1.6
  constraints (10):
    c: Distance(g0) = 5.25
    c: Coincident(g0,g-3)
    c: PointOnObject(g0,g-3)
    c: Vertical(g1)
    c: DistanceY(g1,g1) = 6.5
    c: Symmetric(g1,g1,g0)
    c: Diameter(g2) = 3.2
    c: Diameter(g3) = 3.2
    c: Coincident(g2,g1)
    c: Coincident(g3,g1)
FEATURE [Sketcher::SketchObject] Sketch032  label="spazio per PILA 18650"
  ArcFitTolerance = 1e-06
  AttachmentSupport = -> [XY_Plane]
  ExternalGeometry = -> [Sketch]
  FullyConstrained = true
  MakeInternals = false
  MapMode = 5
  sketch-geometry (2):
    g0: LineSegment [constr] StartX=-178.142 StartY=-1.74e-14 StartZ=0 EndX=-190.142 EndY=-1.83e-14 EndZ=0
    g1: Circle CenterX=-190.142 CenterY=-1.83e-14 CenterZ=0 NormalX=0 NormalY=0 NormalZ=1 AngleXU=0 Radius=9.25
  constraints (5):
    c: Distance(g0) = 12
    c: Coincident(g0,g-3)
    c: PointOnObject(g0,g-4)
    c: Diameter(g1) = 18.5
    c: Coincident(g1,g0)
FEATURE [Part::Extrusion] Extrude030  label="Extrude spazio per PILA 18650"
  Base = -> Sketch032
  Dir = (0,0,1)
  DirLink = -> Sketch [Edge45]
  DirMode = 2
  FaceMakerClass = Part::FaceMakerBullseye
  FaceMakerMode = 3
  LengthFwd = 68
  LengthRev = 0
  Placement = pos=(6,0,-72.7) rot=(0,0,1;0rad)
  Solid = true
  Symmetric = false
FEATURE [Sketcher::SketchObject] Sketch033  label="fermo per scheda micro"
  ArcFitTolerance = 1e-06
  AttachmentSupport = -> [XZ_Plane]
  ExternalGeometry = -> [Sketch]
  FullyConstrained = true
  MakeInternals = false
  MapMode = 5
  Placement = pos=(0,0,0) rot=(1,0,0;1.5708rad)
  sketch-geometry (12):
    g0: LineSegment StartX=-11.6 StartY=6 StartZ=0 EndX=-4 EndY=6 EndZ=0
    g1: LineSegment StartX=-4 StartY=6 StartZ=0 EndX=-4 EndY=36.4 EndZ=0
    g2: LineSegment StartX=-4 StartY=36.4 StartZ=0 EndX=-11.6 EndY=36.4 EndZ=0
    g3: LineSegment StartX=-11.6 StartY=36.4 StartZ=0 EndX=-11.6 EndY=6 EndZ=0
    g4: LineSegment StartX=-80.11 StartY=11.6 StartZ=0 EndX=-70.51 EndY=11.6 EndZ=0
    g5: LineSegment StartX=-70.51 StartY=11.6 StartZ=0 EndX=-70.51 EndY=6 EndZ=0
    g6: LineSegment StartX=-70.51 StartY=6 StartZ=0 EndX=-80.11 EndY=6 EndZ=0
    g7: LineSegment StartX=-80.11 StartY=6 StartZ=0 EndX=-80.11 EndY=11.6 EndZ=0
    g8: LineSegment StartX=-78.51 StartY=36.4 StartZ=0 EndX=-70.51 EndY=36.4 EndZ=0
    g9: LineSegment StartX=-70.51 StartY=36.4 StartZ=0 EndX=-70.51 EndY=30.8 EndZ=0
    g10: LineSegment StartX=-70.51 StartY=30.8 StartZ=0 EndX=-78.51 EndY=30.8 EndZ=0
    g11: LineSegment StartX=-78.51 StartY=30.8 StartZ=0 EndX=-78.51 EndY=36.4 EndZ=0
  constraints (33):
    c: Horizontal(g0)
    c: Coincident(g1,g0)
    c: Coincident(g2,g1)
    c: Horizontal(g2)
    c: Coincident(g3,g2)
    c: Coincident(g3,g0)
    c: Vertical(g3)
    c: DistanceX(g2,g2) = 7.6
    c: Coincident(g1,g-3)
    c: Coincident(g0,g-3)
    c: Horizontal(g4)
    c: Coincident(g5,g4)
    c: Vertical(g5)
    c: Coincident(g6,g5)
    c: Horizontal(g6)
    c: Coincident(g7,g6)
    c: Coincident(g7,g4)
    c: Vertical(g7)
    c: DistanceY(g5,g5) = 5.6
    c: DistanceX(g4,g4) = 9.6
    c: Coincident(g9,g8)
    c: Vertical(g9)
    c: Coincident(g10,g9)
    c: Horizontal(g10)
    c: Coincident(g11,g10)
    c: Coincident(g11,g8)
    c: Vertical(g11)
    c: DistanceY(g9,g9) = 5.6
    c: DistanceX(g10,g10) = 8
    c: Coincident(g4,g-4)
    c: DistanceX(g4,g10) = 1.6
    c: Horizontal(g8)
    c: DistanceY(g8,g1) = 0
FEATURE [Sketcher::SketchObject] Sketch034  label="buchi guida rail"
  ArcFitTolerance = 1e-06
  AttachmentSupport = -> [XY_Plane]
  ExternalGeometry = -> [Sketch]
  FullyConstrained = true
  MakeInternals = false
  MapMode = 5
  sketch-geometry (6):
    g0: LineSegment [constr] StartX=-100.8 StartY=9.1e-15 StartZ=0 EndX=-93.3 EndY=0 EndZ=0
    g1: LineSegment [constr] StartX=-93.3 StartY=0 StartZ=0 EndX=-73.3 EndY=0 EndZ=0
    g2: LineSegment [constr] StartX=-73.3 StartY=0 StartZ=0 EndX=-53.3 EndY=0 EndZ=0
    g3: Circle CenterX=-93.3 CenterY=0 CenterZ=0 NormalX=0 NormalY=0 NormalZ=1 AngleXU=0 Radius=2.5
    g4: Circle CenterX=-73.3 CenterY=0 CenterZ=0 NormalX=0 NormalY=0 NormalZ=1 AngleXU=0 Radius=2.5
    g5: Circle CenterX=-53.3 CenterY=0 CenterZ=0 NormalX=0 NormalY=0 NormalZ=1 AngleXU=0 Radius=2.5
  constraints (15):
    c: Distance(g0) = 7.5
    c: Coincident(g0,g-3)
    c: PointOnObject(g0,g-1)
    c: Distance(g1) = 20
    c: Coincident(g1,g0)
    c: PointOnObject(g1,g-1)
    c: Distance(g2) = 20
    c: Coincident(g2,g1)
    c: PointOnObject(g2,g-1)
    c: Diameter(g3) = 5
    c: Diameter(g4) = 5
    c: Diameter(g5) = 5
    c: Coincident(g3,g0)
    c: Coincident(g4,g1)
    c: Coincident(g5,g2)
FEATURE [Part::Extrusion] Extrude032  label="Extrude buchi guida rail"
  Base = -> Sketch034
  Dir = (0,0,1)
  DirMode = 2
  FaceMakerClass = Part::FaceMakerBullseye
  FaceMakerMode = 3
  LengthFwd = -6.2
  LengthRev = 0
  Placement = pos=(0,0,43.2) rot=(0,0,1;0rad)
  Solid = true
  Symmetric = false
FEATURE [Part::Extrusion] Extrude033  label="Extrude fori superiori per solenoide e oled001"
  Base = -> Sketch030
  Dir = (0,0,1)
  DirMode = 2
  FaceMakerClass = Part::FaceMakerBullseye
  FaceMakerMode = 3
  LengthFwd = -4.8
  LengthRev = 0
  Placement = pos=(0,0,41.2) rot=(0,0,1;0rad)
  Solid = true
  Symmetric = false
FEATURE [Part::Extrusion] Extrude034  label="Extrude fori sotto impugnatura001"
  Base = -> Sketch029
  Dir = (0,0,1)
  DirMode = 2
  FaceMakerClass = Part::FaceMakerBullseye
  FaceMakerMode = 3
  LengthFwd = 5
  LengthRev = 0
  Placement = pos=(0,0,-83) rot=(0,0,1;0rad)
  Solid = true
  Symmetric = false
FEATURE [Part::Extrusion] Extrude035  label="Extrude fori inferiori switch pompa001"
  Base = -> Sketch031
  Dir = (0,0,1)
  DirMode = 2
  FaceMakerClass = Part::FaceMakerBullseye
  FaceMakerMode = 3
  LengthFwd = 4
  LengthRev = 0
  Placement = pos=(0,0,-1.7) rot=(0,0,1;0rad)
  Solid = true
  Symmetric = false
FEATURE [Part::Extrusion] Extrude036  label="Extrude foro sotto posteriore M3x5x007"
  Base = -> Sketch027
  Dir = (0,0,1)
  DirMode = 2
  FaceMakerClass = Part::FaceMakerBullseye
  FaceMakerMode = 3
  LengthFwd = 6.2
  LengthRev = 0
  Placement = pos=(0,0,-9.6) rot=(0,0,1;0rad)
  Solid = true
  Symmetric = false
FEATURE [Part::Extrusion] Extrude037  label="Extrude foro sotto anteriore M3x5x007"
  Base = -> Sketch026
  Dir = (0,0,1)
  DirMode = 2
  FaceMakerClass = Part::FaceMakerBullseye
  FaceMakerMode = 3
  LengthFwd = 6.2
  LengthRev = 0
  Solid = true
  Symmetric = false
FEATURE [Sketcher::SketchObject] Sketch035  label="foro per fissaggio micro"
  ArcFitTolerance = 1e-06
  AttachmentSupport = -> [XZ_Plane]
  ExternalGeometry = -> [Sketch,Sketch033]
  FullyConstrained = true
  MakeInternals = false
  MapMode = 5
  Placement = pos=(0,0,0) rot=(1,0,0;1.5708rad)
  sketch-geometry (3):
    g0: Circle CenterX=-7.8 CenterY=21.2 CenterZ=0 NormalX=0 NormalY=0 NormalZ=1 AngleXU=0 Radius=1.6
    g1: GeomPoint [constr] X=-4 Y=21.2 Z=0
    g2: LineSegment [constr] StartX=-4 StartY=21.2 StartZ=0 EndX=-11.6 EndY=21.2 EndZ=0
  constraints (6):
    c: Diameter(g0) = 3.2
    c: Symmetric(g-3,g-3,g1)
    c: Coincident(g2,g1)
    c: Horizontal(g2)
    c: DistanceX(g-4,g2) = 0
    c: Symmetric(g2,g1,g0)
FEATURE [Part::Extrusion] Extrude038  label="Extrude foro per fissaggio micro"
  Base = -> Sketch035
  Dir = (0,-1,2e-16)
  DirMode = 2
  FaceMakerClass = Part::FaceMakerBullseye
  FaceMakerMode = 3
  LengthFwd = 3
  LengthRev = 0
  Placement = pos=(0,8.6,0) rot=(0,0,1;0rad)
  Solid = true
  Symmetric = false
FEATURE [Sketcher::SketchObject] Sketch036  label="supporto per alimentatore"
  ArcFitTolerance = 1e-06
  AttachmentSupport = -> [XZ_Plane]
  ExternalGeometry = -> [Sketch,Sketch016,Sketch022]
  FullyConstrained = true
  MakeInternals = false
  MapMode = 5
  Placement = pos=(0,0,0) rot=(1,0,0;1.5708rad)
  sketch-geometry (5):
    g0: LineSegment StartX=-211.843 StartY=-50.0944 StartZ=0 EndX=-211.843 EndY=-80.4316 EndZ=0
    g1: LineSegment StartX=-211.843 StartY=-50.0944 StartZ=0 EndX=-207.775 EndY=-41.3701 EndZ=0
    g2: LineSegment [constr] StartX=-209.443 StartY=-50.0944 StartZ=0 EndX=-209.443 EndY=-80.4316 EndZ=0
    g3: LineSegment StartX=-207.775 StartY=-41.3701 StartZ=0 EndX=-207.775 EndY=-80.4316 EndZ=0
    g4: LineSegment StartX=-211.843 StartY=-80.4316 StartZ=0 EndX=-207.775 EndY=-80.4316 EndZ=0
  constraints (15):
    c: Vertical(g0)
    c: Coincident(g1,g0)
    c: Vertical(g2)
    c: Tangent(g2,g-5)
    c: Coincident(g3,g1)
    c: Vertical(g3)
    c: DistanceY(g-3,g3) = -2
    c: Tangent(g1,g-8)
    c: DistanceY(g-3,g0) = -2
    c: Coincident(g4,g0)
    c: Coincident(g4,g3)
    c: Tangent(g0,g-6)
    c: DistanceY(g-3,g2) = -2
    c: DistanceY(g2,g0) = 0
    c: DistanceX(g-3,g3) = 6.8
FEATURE [Part::Extrusion] Extrude039  label="Extrude039 supporto alimentatore"
  Base = -> Sketch036
  Dir = (0,-1,2e-16)
  DirMode = 2
  FaceMakerClass = Part::FaceMakerBullseye
  FaceMakerMode = 3
  LengthFwd = 25.2
  LengthRev = 0
  Solid = true
  Symmetric = true
FEATURE [Sketcher::SketchObject] Sketch037  label="scavo per alimentatore"
  ArcFitTolerance = 1e-06
  AttachmentSupport = -> [XZ_Plane]
  ExternalGeometry = -> [Sketch036]
  FullyConstrained = true
  MakeInternals = false
  MapMode = 5
  Placement = pos=(0,0,0) rot=(1,0,0;1.5708rad)
  sketch-geometry (4):
    g0: LineSegment StartX=-209.575 StartY=-50.4316 StartZ=0 EndX=-209.575 EndY=-80.4316 EndZ=0
    g1: LineSegment StartX=-209.575 StartY=-50.4316 StartZ=0 EndX=-207.775 EndY=-50.4316 EndZ=0
    g2: LineSegment StartX=-207.775 StartY=-50.4316 StartZ=0 EndX=-207.775 EndY=-80.4316 EndZ=0
    g3: LineSegment StartX=-207.775 StartY=-80.4316 StartZ=0 EndX=-209.575 EndY=-80.4316 EndZ=0
  constraints (11):
    c: Vertical(g0)
    c: Coincident(g1,g0)
    c: Horizontal(g1)
    c: Coincident(g2,g1)
    c: Vertical(g2)
    c: Coincident(g3,g2)
    c: Coincident(g3,g0)
    c: Horizontal(g3)
    c: DistanceX(g1,g1) = 1.8
    c: Coincident(g2,g-3)
    c: DistanceY(g2,g2) = 30
FEATURE [Part::Extrusion] Extrude040  label="Extrude040 scavo alimentatore"
  Base = -> Sketch037
  Dir = (0,-1,2e-16)
  DirMode = 2
  FaceMakerClass = Part::FaceMakerBullseye
  FaceMakerMode = 3
  LengthFwd = 19.5
  LengthRev = 0
  Solid = true
  Symmetric = true
FEATURE [Part::Extrusion] Extrude031  label="Extrude fermo per scheda micro"
  Base = -> Sketch033
  Dir = (0,-1,2e-16)
  DirMode = 2
  FaceMakerClass = Part::FaceMakerBullseye
  FaceMakerMode = 3
  LengthFwd = 3
  LengthRev = 0
  Placement = pos=(0,8.6,0) rot=(0,0,1;0rad)
  Solid = true
  Symmetric = false
FEATURE [Sketcher::SketchObject] Sketch038  label="scavo driver solenoide"
  ArcFitTolerance = 1e-06
  AttachmentSupport = -> [XZ_Plane]
  ExternalGeometry = -> [Sketch,Sketch036]
  FullyConstrained = true
  MakeInternals = false
  MapMode = 5
  Placement = pos=(0,0,0) rot=(1,0,0;1.5708rad)
  sketch-geometry (7):
    g0: LineSegment StartX=-193.66 StartY=-11.0994 StartZ=0 EndX=-195.11 EndY=-10.4232 EndZ=0
    g1: LineSegment StartX=-195.11 StartY=-10.4232 StartZ=0 EndX=-209.225 EndY=-40.6939 EndZ=0
    g2: LineSegment StartX=-193.66 StartY=-11.0994 StartZ=0 EndX=-190.216 EndY=-12.7054 EndZ=0
    g3: LineSegment StartX=-190.216 StartY=-12.7054 StartZ=0 EndX=-204.331 EndY=-42.9761 EndZ=0
    g4: LineSegment StartX=-204.331 StartY=-42.9761 StartZ=0 EndX=-207.775 EndY=-41.3701 EndZ=0
    g5: LineSegment [constr] StartX=-209.225 StartY=-40.6939 StartZ=0 EndX=-207.775 EndY=-41.3701 EndZ=0
    g6: LineSegment StartX=-209.225 StartY=-40.6939 StartZ=0 EndX=-207.775 EndY=-41.3701 EndZ=0
  constraints (19):
    c: Coincident(g1,g0)
    c: Coincident(g3,g2)
    c: Coincident(g4,g3)
    c: Distance(g2) = 3.8
    c: Distance(g1) = 33.4
    c: Coincident(g5,g1)
    c: Distance(g5) = 1.6
    c: Coincident(g-4,g5)
    c: Perpendicular(g5,g-3)
    c: Parallel(g1,g-3)
    c: Perpendicular(g1,g0)
    c: Distance(g0) = 1.6
    c: Coincident(g6,g1)
    c: Coincident(g6,g5)
    c: Parallel(g3,g-3)
    c: Perpendicular(g3,g4)
    c: Perpendicular(g2,g3)
    c: Coincident(g2,g0)
    c: Coincident(g4,g5)
FEATURE [Part::Extrusion] Extrude041  label="Extrude scavo driver solenoide"
  Base = -> Sketch038
  Dir = (0,-1,2e-16)
  DirMode = 2
  FaceMakerClass = Part::FaceMakerBullseye
  FaceMakerMode = 3
  LengthFwd = 17
  LengthRev = 0
  Solid = true
  Symmetric = true
FEATURE [Sketcher::SketchObject] Sketch039  label="scavo per cavo usb per micro"
  ArcFitTolerance = 1e-06
  AttachmentSupport = -> [XZ_Plane]
  ExternalGeometry = -> [Sketch,Sketch016]
  FullyConstrained = true
  MakeInternals = false
  MapMode = 5
  Placement = pos=(0,0,0) rot=(1,0,0;1.5708rad)
  sketch-geometry (4):
    g0: LineSegment StartX=-82.51 StartY=36.4 StartZ=0 EndX=-74.51 EndY=36.4 EndZ=0
    g1: LineSegment StartX=-74.51 StartY=36.4 StartZ=0 EndX=-74.51 EndY=30.8 EndZ=0
    g2: LineSegment StartX=-74.51 StartY=30.8 StartZ=0 EndX=-82.51 EndY=30.8 EndZ=0
    g3: LineSegment StartX=-82.51 StartY=30.8 StartZ=0 EndX=-82.51 EndY=36.4 EndZ=0
  constraints (11):
    c: Coincident(g1,g0)
    c: Vertical(g1)
    c: Coincident(g2,g1)
    c: Horizontal(g2)
    c: Coincident(g3,g2)
    c: Coincident(g3,g0)
    c: Vertical(g3)
    c: Tangent(g0,g-3)
    c: Tangent(g2,g-4)
    c: Tangent(g3,g-4)
    c: Tangent(g1,g-4)
FEATURE [Part::Extrusion] Extrude042  label="Extrude scavo per cavo usb per micro"
  Base = -> Sketch039
  Dir = (0,-1,2e-16)
  DirMode = 2
  FaceMakerClass = Part::FaceMakerBullseye
  FaceMakerMode = 3
  LengthFwd = 11.2
  LengthRev = 0
  Solid = true
  Symmetric = true
FEATURE [Sketcher::SketchObject] Sketch040  label="scavo saldature alimentatore connettore 5v"
  ArcFitTolerance = 1e-06
  AttachmentSupport = -> [XZ_Plane]
  ExternalGeometry = -> [Sketch037]
  FullyConstrained = true
  MakeInternals = false
  MapMode = 5
  Placement = pos=(0,0,0) rot=(1,0,0;1.5708rad)
  sketch-geometry (4):
    g0: LineSegment StartX=-211.175 StartY=-52.4316 StartZ=0 EndX=-211.175 EndY=-56.4316 EndZ=0
    g1: LineSegment StartX=-211.175 StartY=-52.4316 StartZ=0 EndX=-209.575 EndY=-52.4316 EndZ=0
    g2: LineSegment StartX=-209.575 StartY=-52.4316 StartZ=0 EndX=-209.575 EndY=-56.4316 EndZ=0
    g3: LineSegment StartX=-209.575 StartY=-56.4316 StartZ=0 EndX=-211.175 EndY=-56.4316 EndZ=0
  constraints (11):
    c: Vertical(g0)
    c: Coincident(g1,g0)
    c: Horizontal(g1)
    c: Coincident(g2,g1)
    c: Coincident(g3,g2)
    c: Coincident(g3,g0)
    c: Horizontal(g3)
    c: DistanceX(g1,g1) = 1.6
    c: DistanceY(g2,g2) = 4
    c: Tangent(g2,g-3)
    c: DistanceY(g1,g-3) = 2
FEATURE [Part::Extrusion] Extrude043  label="Extrude scavo saldature alimentatore connettore 5v"
  Base = -> Sketch040
  Dir = (0,-1,2e-16)
  DirMode = 2
  FaceMakerClass = Part::FaceMakerBullseye
  FaceMakerMode = 3
  LengthFwd = 8
  LengthRev = 0
  Solid = true
  Symmetric = true
FEATURE [Sketcher::SketchObject] Sketch041  label="scavo saldature alimentatore connettore 5v verticali"
  ArcFitTolerance = 1e-06
  AttachmentSupport = -> [XZ_Plane]
  ExternalGeometry = -> [Sketch037]
  FullyConstrained = true
  MakeInternals = false
  MapMode = 5
  Placement = pos=(0,0,0) rot=(1,0,0;1.5708rad)
  sketch-geometry (4):
    g0: LineSegment StartX=-211.175 StartY=-53.6316 StartZ=0 EndX=-209.575 EndY=-53.6316 EndZ=0
    g1: LineSegment StartX=-209.575 StartY=-53.6316 StartZ=0 EndX=-209.575 EndY=-76.6316 EndZ=0
    g2: LineSegment StartX=-209.575 StartY=-76.6316 StartZ=0 EndX=-211.175 EndY=-76.6316 EndZ=0
    g3: LineSegment StartX=-211.175 StartY=-76.6316 StartZ=0 EndX=-211.175 EndY=-53.6316 EndZ=0
  constraints (11):
    c: Horizontal(g0)
    c: Coincident(g1,g0)
    c: Coincident(g2,g1)
    c: Horizontal(g2)
    c: Coincident(g3,g2)
    c: Coincident(g3,g0)
    c: Vertical(g3)
    c: DistanceY(g3,g3) = 23
    c: DistanceX(g0,g0) = 1.6
    c: Tangent(g1,g-3)
    c: DistanceY(g0,g-3) = 3.2
FEATURE [Part::Extrusion] Extrude044  label="Extrude scavo saldature alimentatore connettore 5v verticali"
  Base = -> Sketch041
  Dir = (0,-1,2e-16)
  DirMode = 2
  FaceMakerClass = Part::FaceMakerBullseye
  FaceMakerMode = 3
  LengthFwd = 3.2
  LengthRev = 0
  Placement = pos=(0,8.3,0) rot=(0,0,1;0rad)
  Solid = true
  Symmetric = false
FEATURE [Sketcher::SketchObject] Sketch042  label="fermi per driver solenoide e alimentatore"
  ArcFitTolerance = 1e-06
  AttachmentSupport = -> [XZ_Plane]
  ExternalGeometry = -> [Sketch036,Sketch037,Sketch,Sketch038]
  FullyConstrained = true
  MakeInternals = false
  MapMode = 5
  Placement = pos=(0,0,0) rot=(1,0,0;1.5708rad)
  sketch-geometry (27):
    g0: LineSegment StartX=-195.773 StartY=-15.631 StartZ=0 EndX=-196.702 EndY=-17.6249 EndZ=0
    g1: LineSegment StartX=-196.702 StartY=-17.6249 StartZ=0 EndX=-194.709 EndY=-18.5546 EndZ=0
    g2: LineSegment StartX=-194.709 StartY=-18.5546 StartZ=0 EndX=-193.779 EndY=-16.5607 EndZ=0
    g3: LineSegment StartX=-193.779 StartY=-16.5607 StartZ=0 EndX=-195.773 EndY=-15.631 EndZ=0
    g4: LineSegment StartX=-196.547 StartY=-13.5047 StartZ=0 EndX=-198.829 EndY=-18.3988 EndZ=0
    g5: LineSegment StartX=-198.829 StartY=-18.3988 StartZ=0 EndX=-195.385 EndY=-20.0047 EndZ=0
    g6: LineSegment StartX=-193.258 StartY=-19.2308 StartZ=0 EndX=-192.329 EndY=-17.2369 EndZ=0
    g7: LineSegment StartX=-193.103 StartY=-15.1106 StartZ=0 EndX=-196.547 EndY=-13.5047 EndZ=0
    g8: LineSegment [constr] StartX=-193.935 StartY=-20.6809 StartZ=0 EndX=-193.258 EndY=-19.2308 EndZ=0
    g9: LineSegment [constr] StartX=-193.935 StartY=-20.6809 StartZ=0 EndX=-195.385 EndY=-20.0047 EndZ=0
    g10: ArcOfCircle CenterX=-193.779 CenterY=-16.5607 CenterZ=0 NormalX=0 NormalY=0 NormalZ=1 AngleXU=0 Radius=1.6 StartAngle=5.84685 EndAngle=7.41765
    g11: GeomPoint [constr] X=-191.653 Y=-15.7868 Z=0
    g12: ArcOfCircle CenterX=-194.709 CenterY=-18.5546 CenterZ=0 NormalX=0 NormalY=0 NormalZ=1 AngleXU=0 Radius=1.6 StartAngle=4.27606 EndAngle=5.84685
    g13: GeomPoint [constr] X=-193.935 Y=-20.6809 Z=0
    g14: LineSegment StartX=-207.775 StartY=-46.8316 StartZ=0 EndX=-207.775 EndY=-50.8316 EndZ=0
    g15: LineSegment StartX=-207.775 StartY=-46.8316 StartZ=0 EndX=-203.775 EndY=-46.8316 EndZ=0
    g16: LineSegment StartX=-203.775 StartY=-46.8316 StartZ=0 EndX=-203.775 EndY=-50.8316 EndZ=0
    g17: LineSegment StartX=-207.775 StartY=-50.8316 StartZ=0 EndX=-203.775 EndY=-50.8316 EndZ=0
    g18: LineSegment StartX=-209.375 StartY=-52.4316 StartZ=0 EndX=-203.775 EndY=-52.4316 EndZ=0
    g19: LineSegment StartX=-202.175 StartY=-50.8316 StartZ=0 EndX=-202.175 EndY=-46.8316 EndZ=0
    g20: LineSegment StartX=-203.775 StartY=-45.2316 StartZ=0 EndX=-209.375 EndY=-45.2316 EndZ=0
    g21: LineSegment StartX=-209.375 StartY=-45.2316 StartZ=0 EndX=-209.375 EndY=-52.4316 EndZ=0
    g22: ArcOfCircle CenterX=-203.775 CenterY=-46.8316 CenterZ=0 NormalX=0 NormalY=0 NormalZ=1 AngleXU=0 Radius=1.6 StartAngle=1.8e-15 EndAngle=1.5708
    g23: GeomPoint [constr] X=-202.175 Y=-45.2316 Z=0
    g24: ArcOfCircle CenterX=-203.775 CenterY=-50.8316 CenterZ=0 NormalX=0 NormalY=0 NormalZ=1 AngleXU=0 Radius=1.6 StartAngle=4.71239 EndAngle=6.28319
    g25: GeomPoint [constr] X=-202.175 Y=-52.4316 Z=0
    g26: LineSegment [constr] StartX=-207.775 StartY=-50.4316 StartZ=0 EndX=-207.775 EndY=-50.8316 EndZ=0
  constraints (69):
    c: Coincident(g1,g0)
    c: Coincident(g2,g1)
    c: Coincident(g3,g2)
    c: Coincident(g3,g0)
    c: Parallel(g0,g2)
    c: Perpendicular(g3,g0)
    c: Perpendicular(g1,g0)
    c: Coincident(g5,g4)
    c: Coincident(g7,g4)
    c: Distance(g3) = 2.2
    c: Distance(g2) = 2.2
    c: Parallel(g6,g2)
    c: Parallel(g6,g4)
    c: Perpendicular(g5,g6)
    c: Perpendicular(g7,g6)
    c: Distance(g13,g11) = 5.4
    c: Distance(g5,g13) = 5.4
    c: Coincident(g9,g8)
    c: Distance(g8) = 1.6
    c: Distance(g9) = 1.6
    c: Perpendicular(g9,g8)
    c: Parallel(g8,g6)
    c: Coincident(g8,g13)
    c: Distance(g8,g1) = 1.6
    c: Distance(g9,g1) = 1.6
    c: Tangent(g0,g-5)
    c: Distance(g0,g-6) = 26.2
    c: PointOnObject(g11,g7)
    c: PointOnObject(g11,g6)
    c: Tangent(g7,g10) = -1.5708
    c: Tangent(g6,g10) = -1.5708
    c: PointOnObject(g13,g5)
    c: Tangent(g5,g12) = -1.5708
    c: Tangent(g6,g12) = -1.5708
    c: Equal(g10,g12)
    c: Coincident(g10,g2)
    c: Vertical(g14)
    c: Coincident(g15,g14)
    c: Horizontal(g15)
    c: Coincident(g16,g15)
    c: Vertical(g16)
    c: Coincident(g17,g14)
    c: Coincident(g17,g16)
    c: Horizontal(g17)
    c: Distance(g16) = 4
    c: Distance(g15) = 4
    c: Horizontal(g18)
    c: Vertical(g19)
    c: Horizontal(g20)
    c: Coincident(g21,g20)
    c: Coincident(g21,g18)
    c: Vertical(g21)
    c: Distance(g20,g23) = 7.2
    c: Distance(g25,g23) = 7.2
    c: DistanceY(g18,g14) = 1.6
    c: DistanceX(g18,g14) = 1.6
    c: PointOnObject(g23,g20)
    c: PointOnObject(g23,g19)
    c: Tangent(g20,g22) = -1.5708
    c: Tangent(g19,g22) = -1.5708
    c: PointOnObject(g25,g19)
    c: Tangent(g18,g24) = -1.5708
    c: Tangent(g19,g24) = -1.5708
    c: Equal(g22,g24)
    c: Coincident(g22,g15)
    c: Vertical(g26)
    c: Distance(g26) = 0.4
    c: Coincident(g26,g-4)
    c: Coincident(g14,g26)
FEATURE [Part::Extrusion] Extrude045  label="Extrude fermi per driver solenoide e alimentatore"
  Base = -> Sketch042
  Dir = (0,-1,2e-16)
  DirMode = 2
  FaceMakerClass = Part::FaceMakerBullseye
  FaceMakerMode = 3
  LengthFwd = 25.2
  LengthRev = 0
  Solid = true
  Symmetric = true
FEATURE [Sketcher::SketchObject] Sketch043  label="scavo pulizia fermo alimentatore"
  ArcFitTolerance = 1e-06
  AttachmentSupport = -> [XZ_Plane]
  ExternalGeometry = -> [Sketch042,Sketch036,Sketch037]
  FullyConstrained = true
  MakeInternals = false
  MapMode = 5
  Placement = pos=(0,0,0) rot=(1,0,0;1.5708rad)
  sketch-geometry (6):
    g0: LineSegment StartX=-209.375 StartY=-52.4316 StartZ=0 EndX=-209.375 EndY=-50.4316 EndZ=0
    g1: LineSegment StartX=-209.375 StartY=-50.4316 StartZ=0 EndX=-207.775 EndY=-50.4316 EndZ=0
    g2: LineSegment StartX=-207.775 StartY=-50.4316 StartZ=0 EndX=-207.775 EndY=-45.2316 EndZ=0
    g3: LineSegment StartX=-207.775 StartY=-45.2316 StartZ=0 EndX=-202.175 EndY=-45.2316 EndZ=0
    g4: LineSegment StartX=-202.175 StartY=-45.2316 StartZ=0 EndX=-202.175 EndY=-52.4316 EndZ=0
    g5: LineSegment StartX=-202.175 StartY=-52.4316 StartZ=0 EndX=-209.375 EndY=-52.4316 EndZ=0
  constraints (13):
    c: Vertical(g0)
    c: Coincident(g1,g0)
    c: Coincident(g2,g1)
    c: Coincident(g3,g2)
    c: Coincident(g4,g3)
    c: Coincident(g5,g4)
    c: Coincident(g5,g0)
    c: Horizontal(g5)
    c: Coincident(g0,g-6)
    c: Tangent(g1,g-8)
    c: Tangent(g2,g-4)
    c: Tangent(g3,g-7)
    c: Tangent(g4,g-3)
FEATURE [Part::Extrusion] Extrude046  label="Extrude scavo pulizia fermo alimentatore"
  Base = -> Sketch043
  Dir = (0,-1,2e-16)
  DirMode = 2
  FaceMakerClass = Part::FaceMakerBullseye
  FaceMakerMode = 3
  LengthFwd = 19.5
  LengthRev = 0
  Solid = true
  Symmetric = true
FEATURE [Sketcher::SketchObject] Sketch044  label="buchini per fissaggio oled"
  ArcFitTolerance = 1e-06
  AttachmentSupport = -> [YZ_Plane]
  ExternalGeometry = -> [Sketch]
  FullyConstrained = true
  MakeInternals = false
  MapMode = 5
  Placement = pos=(0,0,0) rot=(0.57735,0.57735,0.57735;2.0944rad)
  sketch-geometry (5):
    g0: LineSegment [constr] StartX=1.5e-14 StartY=67.3588 StartZ=0 EndX=0 EndY=64.3588 EndZ=0
    g1: LineSegment [constr] StartX=0 StartY=64.3588 StartZ=0 EndX=10.4 EndY=64.3588 EndZ=0
    g2: LineSegment [constr] StartX=0 StartY=64.3588 StartZ=0 EndX=-10.4 EndY=64.3588 EndZ=0
    g3: Circle CenterX=10.4 CenterY=64.3588 CenterZ=0 NormalX=0 NormalY=0 NormalZ=1 AngleXU=0 Radius=1.5
    g4: Circle CenterX=-10.4 CenterY=64.3588 CenterZ=0 NormalX=0 NormalY=0 NormalZ=1 AngleXU=0 Radius=1.5
  constraints (13):
    c: Distance(g0) = 3
    c: PointOnObject(g0,g-2)
    c: Coincident(g1,g0)
    c: Horizontal(g1)
    c: Coincident(g2,g0)
    c: Horizontal(g2)
    c: DistanceX(g1,g1) = 10.4
    c: Coincident(g3,g1)
    c: Diameter(g4) = 3
    c: Coincident(g4,g2)
    c: Coincident(g0,g-7)
    c: Equal(g1,g2)
    c: Equal(g4,g3)
FEATURE [Part::Extrusion] Extrude047  label="Extrude buchini per fissaggio oled"
  Base = -> Sketch044
  Dir = (1,0,0)
  DirMode = 2
  FaceMakerClass = Part::FaceMakerBullseye
  FaceMakerMode = 3
  LengthFwd = 10
  LengthRev = 0
  Placement = pos=(-186,0,0) rot=(0,0,1;0rad)
  Solid = true
  Symmetric = false
FEATURE [Sketcher::SketchObject] Sketch046  label="scavo 5x5 neopixel"
  ArcFitTolerance = 1e-06
  AttachmentSupport = -> [YZ_Plane002]
  FullyConstrained = true
  MakeInternals = false
  MapMode = 5
  Placement = pos=(0,0,0) rot=(0.57735,0.57735,0.57735;2.0944rad)
  sketch-geometry (4):
    g0: LineSegment StartX=-2.7 StartY=2.7 StartZ=0 EndX=2.7 EndY=2.7 EndZ=0
    g1: LineSegment StartX=2.7 StartY=2.7 StartZ=0 EndX=2.7 EndY=-2.7 EndZ=0
    g2: LineSegment StartX=2.7 StartY=-2.7 StartZ=0 EndX=-2.7 EndY=-2.7 EndZ=0
    g3: LineSegment StartX=-2.7 StartY=-2.7 StartZ=0 EndX=-2.7 EndY=2.7 EndZ=0
  constraints (11):
    c: Horizontal(g0)
    c: Coincident(g1,g0)
    c: Vertical(g1)
    c: Coincident(g2,g1)
    c: Horizontal(g2)
    c: Coincident(g3,g2)
    c: Coincident(g3,g0)
    c: Vertical(g3)
    c: DistanceX(g0,g0) = 5.4
    c: DistanceY(g1,g1) = 5.4
    c: Symmetric(g0,g1,g-1)
FEATURE [Sketcher::SketchObject] Sketch047  label="scavo 10x10 neopixel corpo"
  ArcFitTolerance = 1e-06
  AttachmentOffset = pos=(0,0,1) rot=(0,0,1;0rad)
  AttachmentSupport = -> [YZ_Plane002]
  FullyConstrained = true
  MakeInternals = false
  MapMode = 5
  Placement = pos=(1,0,0) rot=(0.57735,0.57735,0.57735;2.0944rad)
  sketch-geometry (4):
    g0: LineSegment StartX=-5 StartY=5.1 StartZ=0 EndX=5 EndY=5.1 EndZ=0
    g1: LineSegment StartX=5 StartY=5.1 StartZ=0 EndX=5 EndY=-5.1 EndZ=0
    g2: LineSegment StartX=5 StartY=-5.1 StartZ=0 EndX=-5 EndY=-5.1 EndZ=0
    g3: LineSegment StartX=-5 StartY=-5.1 StartZ=0 EndX=-5 EndY=5.1 EndZ=0
  constraints (11):
    c: Horizontal(g0)
    c: Coincident(g1,g0)
    c: Vertical(g1)
    c: Coincident(g2,g1)
    c: Horizontal(g2)
    c: Coincident(g3,g2)
    c: Coincident(g3,g0)
    c: Vertical(g3)
    c: DistanceX(g0,g0) = 10
    c: DistanceY(g1,g1) = 10.2
    c: Symmetric(g0,g2,g-1)
FEATURE [Sketcher::SketchObject] Sketch048  label="buco per perno blocco neopixel"
  ArcFitTolerance = 1e-06
  AttachmentSupport = -> [XZ_Plane002]
  FullyConstrained = true
  MakeInternals = false
  MapMode = 5
  Placement = pos=(0,0,0) rot=(1,0,0;1.5708rad)
  sketch-geometry (4):
    g0: LineSegment StartX=3 StartY=1.2 StartZ=0 EndX=3 EndY=-1.2 EndZ=0
    g1: LineSegment StartX=3 StartY=-1.2 StartZ=0 EndX=5.4 EndY=-1.2 EndZ=0
    g2: LineSegment StartX=5.4 StartY=-1.2 StartZ=0 EndX=5.4 EndY=1.2 EndZ=0
    g3: LineSegment StartX=5.4 StartY=1.2 StartZ=0 EndX=3 EndY=1.2 EndZ=0
  constraints (11):
    c: Coincident(g1,g0)
    c: Horizontal(g1)
    c: Coincident(g2,g1)
    c: Vertical(g2)
    c: Coincident(g3,g2)
    c: Coincident(g3,g0)
    c: Horizontal(g3)
    c: DistanceX(g1,g1) = 2.4
    c: DistanceY(g2,g2) = 2.4
    c: Symmetric(g0,g0,g-1)
    c: DistanceX(g-1,g0) = 3
FEATURE [Sketcher::SketchObject] Sketch045  label="blocco principale per neopixel"
  ArcFitTolerance = 1e-06
  AttachmentSupport = -> [XZ_Plane002]
  ExternalGeometry = -> [Sketch048]
  FullyConstrained = true
  MakeInternals = false
  MapMode = 5
  Placement = pos=(0,0,0) rot=(1,0,0;1.5708rad)
  sketch-geometry (6):
    g0: LineSegment StartX=0 StartY=5.1 StartZ=0 EndX=0 EndY=-5.1 EndZ=0
    g1: LineSegment StartX=0 StartY=-5.1 StartZ=0 EndX=3 EndY=-5.1 EndZ=0
    g2: LineSegment StartX=7 StartY=-1.1 StartZ=0 EndX=7 EndY=5.1 EndZ=0
    g3: LineSegment StartX=7 StartY=5.1 StartZ=0 EndX=0 EndY=5.1 EndZ=0
    g4: ArcOfCircle CenterX=3 CenterY=-1.1 CenterZ=0 NormalX=0 NormalY=0 NormalZ=1 AngleXU=0 Radius=4 StartAngle=4.71239 EndAngle=6.28319
    g5: GeomPoint [constr] X=7 Y=-5.1 Z=0
  constraints (15):
    c: Vertical(g0)
    c: Coincident(g1,g0)
    c: Horizontal(g1)
    c: Vertical(g2)
    c: Coincident(g3,g2)
    c: Coincident(g3,g0)
    c: Horizontal(g3)
    c: DistanceY(g0,g0) = 10.2
    c: Symmetric(g0,g0,g-1)
    c: DistanceX(g3,g3) = 7
    c: PointOnObject(g5,g2)
    c: PointOnObject(g5,g1)
    c: Tangent(g2,g4) = -1.5708
    c: Tangent(g1,g4) = -1.5708
    c: DistanceX(g-3,g1) = 0
FEATURE [Sketcher::SketchObject] Sketch049  label="rinforzi esterni per corpo neopoixel"
  ArcFitTolerance = 1e-06
  AttachmentSupport = -> [XZ_Plane002]
  ExternalGeometry = -> [Sketch045]
  FullyConstrained = true
  MakeInternals = false
  MapMode = 5
  Placement = pos=(0,0,0) rot=(1,0,0;1.5708rad)
  sketch-geometry (8):
    g0: LineSegment StartX=1 StartY=-4.1 StartZ=0 EndX=2 EndY=-4.1 EndZ=0
    g1: LineSegment StartX=2 StartY=-4.1 StartZ=0 EndX=2 EndY=-5.1 EndZ=0
    g2: LineSegment StartX=2 StartY=-5.1 StartZ=0 EndX=1 EndY=-5.1 EndZ=0
    g3: LineSegment StartX=1 StartY=-5.1 StartZ=0 EndX=1 EndY=-4.1 EndZ=0
    g4: LineSegment StartX=1 StartY=5.1 StartZ=0 EndX=2 EndY=5.1 EndZ=0
    g5: LineSegment StartX=2 StartY=5.1 StartZ=0 EndX=2 EndY=4.1 EndZ=0
    g6: LineSegment StartX=2 StartY=4.1 StartZ=0 EndX=1 EndY=4.1 EndZ=0
    g7: LineSegment StartX=1 StartY=4.1 StartZ=0 EndX=1 EndY=5.1 EndZ=0
  constraints (24):
    c: Horizontal(g0)
    c: Coincident(g1,g0)
    c: Vertical(g1)
    c: Coincident(g2,g1)
    c: Horizontal(g2)
    c: Coincident(g3,g2)
    c: Coincident(g3,g0)
    c: Vertical(g3)
    c: Horizontal(g4)
    c: Coincident(g5,g4)
    c: Vertical(g5)
    c: Coincident(g6,g5)
    c: Horizontal(g6)
    c: Coincident(g7,g6)
    c: Coincident(g7,g4)
    c: Vertical(g7)
    c: DistanceX(g4,g4) = 1
    c: DistanceY(g5,g5) = 1
    c: DistanceX(g0,g0) = 1
    c: DistanceY(g1,g1) = 1
    c: DistanceX(g-3,g4) = 1
    c: DistanceY(g-3,g4) = 0
    c: DistanceX(g-4,g2) = 1
    c: DistanceY(g2,g-4) = 0
FEATURE [Sketcher::SketchObject] Sketch052  label="scavo saldature driver solenoide"
  ArcFitTolerance = 1e-06
  AttachmentSupport = -> [XZ_Plane]
  ExternalGeometry = -> [Sketch038]
  FullyConstrained = true
  MakeInternals = false
  MapMode = 5
  Placement = pos=(0,0,0) rot=(1,0,0;1.5708rad)
  sketch-geometry (4):
    g0: LineSegment StartX=-196.56 StartY=-9.74706 StartZ=0 EndX=-198.25 EndY=-13.3723 EndZ=0
    g1: LineSegment StartX=-198.25 StartY=-13.3723 StartZ=0 EndX=-196.8 EndY=-14.0485 EndZ=0
    g2: LineSegment StartX=-196.8 StartY=-14.0485 StartZ=0 EndX=-195.11 EndY=-10.4232 EndZ=0
    g3: LineSegment StartX=-195.11 StartY=-10.4232 StartZ=0 EndX=-196.56 EndY=-9.74706 EndZ=0
  constraints (11):
    c: Coincident(g1,g0)
    c: Coincident(g2,g1)
    c: Coincident(g3,g2)
    c: Coincident(g3,g0)
    c: Parallel(g2,g0)
    c: Perpendicular(g2,g3)
    c: Perpendicular(g1,g2,g1) = 1.5708
    c: Parallel(g2,g-3)
    c: Distance(g2) = 4
    c: Distance(g3) = 1.6
    c: Coincident(g2,g-3)
FEATURE [Part::Extrusion] Extrude055  label="Extrude scavo saldature driver solenoide"
  Base = -> Sketch052
  Dir = (0,-1,2e-16)
  DirMode = 2
  FaceMakerClass = Part::FaceMakerBullseye
  FaceMakerMode = 3
  LengthFwd = 6
  LengthRev = 0
  Solid = true
  Symmetric = true
FEATURE [Sketcher::SketchObject] Sketch053  label="scavo saldature rumble"
  ArcFitTolerance = 1e-06
  AttachmentSupport = -> [XZ_Plane]
  ExternalGeometry = -> [Sketch019]
  FullyConstrained = true
  MakeInternals = false
  MapMode = 5
  Placement = pos=(0,0,0) rot=(1,0,0;1.5708rad)
  sketch-geometry (4):
    g0: LineSegment StartX=-165.31 StartY=-44.1173 StartZ=0 EndX=-166.547 EndY=-47.9216 EndZ=0
    g1: LineSegment StartX=-166.547 StartY=-47.9216 StartZ=0 EndX=-165.405 EndY=-48.2924 EndZ=0
    g2: LineSegment StartX=-165.405 StartY=-48.2924 StartZ=0 EndX=-164.169 EndY=-44.4881 EndZ=0
    g3: LineSegment StartX=-164.169 StartY=-44.4881 StartZ=0 EndX=-165.31 EndY=-44.1173 EndZ=0
  constraints (11):
    c: Coincident(g1,g0)
    c: Coincident(g2,g1)
    c: Coincident(g3,g2)
    c: Coincident(g3,g0)
    c: Parallel(g0,g2)
    c: Perpendicular(g3,g0)
    c: Perpendicular(g1,g0)
    c: Parallel(g0,g-3)
    c: Distance(g0) = 4
    c: Distance(g1) = 1.2
    c: Coincident(g0,g-3)
FEATURE [Part::Extrusion] Extrude056  label="Extrude scavo saldature rumble"
  Base = -> Sketch053
  Dir = (0,-1,2e-16)
  DirMode = 2
  FaceMakerClass = Part::FaceMakerBullseye
  FaceMakerMode = 3
  LengthFwd = 8.4
  LengthRev = 0
  Solid = true
  Symmetric = true
FEATURE [Sketcher::SketchObject] Sketch054  label="scavo saldature alimentatore connettore USB"
  ArcFitTolerance = 1e-06
  AttachmentSupport = -> [XZ_Plane]
  ExternalGeometry = -> [Sketch037]
  FullyConstrained = true
  MakeInternals = false
  MapMode = 5
  Placement = pos=(0,0,0) rot=(1,0,0;1.5708rad)
  sketch-geometry (4):
    g0: LineSegment StartX=-209.575 StartY=-80.4316 StartZ=0 EndX=-210.375 EndY=-80.4316 EndZ=0
    g1: LineSegment StartX=-210.375 StartY=-80.4316 StartZ=0 EndX=-210.375 EndY=-72.4316 EndZ=0
    g2: LineSegment StartX=-210.375 StartY=-72.4316 StartZ=0 EndX=-209.575 EndY=-72.4316 EndZ=0
    g3: LineSegment StartX=-209.575 StartY=-72.4316 StartZ=0 EndX=-209.575 EndY=-80.4316 EndZ=0
  constraints (11):
    c: Horizontal(g0)
    c: Coincident(g1,g0)
    c: Vertical(g1)
    c: Coincident(g2,g1)
    c: Horizontal(g2)
    c: Coincident(g3,g2)
    c: Coincident(g3,g0)
    c: Vertical(g3)
    c: DistanceX(g0,g0) = 0.8
    c: DistanceY(g3,g3) = 8
    c: Coincident(g0,g-4)
FEATURE [Part::Extrusion] Extrude057  label="Extrude scavo saldature alimentatore connettore USB"
  Base = -> Sketch054
  Dir = (0,-1,2e-16)
  DirMode = 2
  FaceMakerClass = Part::FaceMakerBullseye
  FaceMakerMode = 3
  LengthFwd = 11
  LengthRev = 0
  Solid = true
  Symmetric = true
FEATURE [Sketcher::SketchObject] Sketch055  label="buco interno per micro switch"
  ArcFitTolerance = 1e-06
  AttachmentSupport = -> [XZ_Plane]
  ExternalGeometry = -> [Sketch]
  FullyConstrained = true
  MakeInternals = false
  MapMode = 5
  Placement = pos=(0,0,0) rot=(1,0,0;1.5708rad)
  sketch-geometry (11):
    g0: LineSegment [constr] StartX=-194.483 StartY=34.2854 StartZ=0 EndX=-196.022 EndY=30.0568 EndZ=0
    g1: LineSegment [constr] StartX=-196.022 StartY=30.0568 StartZ=0 EndX=-197.561 EndY=25.8282 EndZ=0
    g2: LineSegment [constr] StartX=-196.022 StartY=30.0568 StartZ=0 EndX=-194.143 EndY=29.3727 EndZ=0
    g3: LineSegment [constr] StartX=-196.022 StartY=30.0568 StartZ=0 EndX=-197.902 EndY=30.7408 EndZ=0
    g4: LineSegment StartX=-196.362 StartY=34.9694 StartZ=0 EndX=-192.604 EndY=33.6014 EndZ=0
    g5: LineSegment StartX=-199.441 StartY=26.5122 StartZ=0 EndX=-195.682 EndY=25.1441 EndZ=0
    g6: LineSegment StartX=-192.604 StartY=33.6014 StartZ=0 EndX=-195.682 EndY=25.1441 EndZ=0
    g7: LineSegment StartX=-196.362 StartY=34.9694 StartZ=0 EndX=-199.441 EndY=26.5122 EndZ=0
    g8: GeomPoint [constr] X=-187.821 Y=29.2 Z=0
    g9: LineSegment [constr] StartX=-188.505 StartY=27.3206 StartZ=0 EndX=-196.022 EndY=30.0568 EndZ=0
    g10: LineSegment [constr] StartX=-187.821 StartY=29.2 StartZ=0 EndX=-188.505 EndY=27.3206 EndZ=0
  constraints (27):
    c: Coincident(g2,g0)
    c: Parallel(g0,g-3)
    c: Tangent(g1,g0) = -1.5708
    c: Perpendicular(g0,g2)
    c: Tangent(g2,g3)
    c: Distance(g0,g1) = 9
    c: Equal(g0,g1)
    c: Distance(g3,g2) = 4
    c: Equal(g2,g3)
    c: Parallel(g3,g4)
    c: Symmetric(g4,g4,g0)
    c: Parallel(g6,g1)
    c: Parallel(g7,g1)
    c: Symmetric(g6,g6,g2)
    c: Symmetric(g5,g5,g1)
    c: Symmetric(g7,g7,g3)
    c: Coincident(g7,g4)
    c: Coincident(g6,g4)
    c: Coincident(g5,g6)
    c: Symmetric(g-3,g-3,g8)
    c: Perpendicular(g-3,g9)
    c: Distance(g9) = 8
    c: Coincident(g3,g9)
    c: Coincident(g10,g8)
    c: Parallel(g10,g-3)
    c: Distance(g10) = 2
    c: Coincident(g10,g9)
FEATURE [Sketcher::SketchObject] Sketch056  label="buco esterno per micro switch"
  ArcFitTolerance = 1e-06
  AttachmentSupport = -> [XZ_Plane]
  ExternalGeometry = -> [Sketch055]
  FullyConstrained = true
  MakeInternals = false
  MapMode = 5
  Placement = pos=(0,0,0) rot=(1,0,0;1.5708rad)
  sketch-geometry (17):
    g0: GeomPoint [constr] X=-194.143 Y=29.3727 Z=0
    g1: GeomPoint [constr] X=-194.483 Y=34.2854 Z=0
    g2: GeomPoint [constr] X=-197.902 Y=30.7408 Z=0
    g3: GeomPoint [constr] X=-197.561 Y=25.8282 Z=0
    g4: GeomPoint [constr] X=-196.022 Y=30.0568 Z=0
    g5: LineSegment [constr] StartX=-194.483 StartY=34.2854 StartZ=0 EndX=-196.022 EndY=30.0568 EndZ=0
    g6: LineSegment [constr] StartX=-196.022 StartY=30.0568 StartZ=0 EndX=-197.561 EndY=25.8282 EndZ=0
    g7: LineSegment [constr] StartX=-197.902 StartY=30.7408 StartZ=0 EndX=-196.022 EndY=30.0568 EndZ=0
    g8: LineSegment [constr] StartX=-196.022 StartY=30.0568 StartZ=0 EndX=-194.143 EndY=29.3727 EndZ=0
    g9: LineSegment [constr] StartX=-195.338 StartY=31.9362 StartZ=0 EndX=-196.022 EndY=30.0568 EndZ=0
    g10: LineSegment [constr] StartX=-196.022 StartY=30.0568 StartZ=0 EndX=-196.706 EndY=28.1774 EndZ=0
    g11: LineSegment [constr] StartX=-196.022 StartY=30.0568 StartZ=0 EndX=-196.821 EndY=30.3475 EndZ=0
    g12: LineSegment [constr] StartX=-196.022 StartY=30.0568 StartZ=0 EndX=-195.223 EndY=29.7661 EndZ=0
    g13: LineSegment StartX=-194.539 StartY=31.6454 StartZ=0 EndX=-195.907 EndY=27.8867 EndZ=0
    g14: LineSegment StartX=-196.137 StartY=32.2269 StartZ=0 EndX=-197.505 EndY=28.4681 EndZ=0
    g15: LineSegment StartX=-196.137 StartY=32.2269 StartZ=0 EndX=-194.539 EndY=31.6454 EndZ=0
    g16: LineSegment StartX=-197.505 StartY=28.4681 StartZ=0 EndX=-195.907 EndY=27.8867 EndZ=0
  constraints (34):
    c: Symmetric(g-5,g-5,g1)
    c: Symmetric(g-5,g-6,g0)
    c: Symmetric(g-6,g-6,g3)
    c: Symmetric(g-5,g-6,g2)
    c: Coincident(g5,g1)
    c: Coincident(g5,g4)
    c: Coincident(g6,g4)
    c: Coincident(g6,g3)
    c: Equal(g5,g6)
    c: Coincident(g7,g2)
    c: Coincident(g7,g4)
    c: Coincident(g8,g4)
    c: Coincident(g8,g0)
    c: Equal(g7,g8)
    c: Coincident(g11,g9)
    c: Coincident(g12,g9)
    c: Tangent(g10,g9) = -1.5708
    c: Perpendicular(g11,g9)
    c: Parallel(g9,g-4)
    c: Equal(g9,g10)
    c: Parallel(g12,g11)
    c: Equal(g11,g12)
    c: Distance(g11,g12) = 1.7
    c: Distance(g9,g10) = 4
    c: Symmetric(g13,g13,g12)
    c: Parallel(g13,g9)
    c: Symmetric(g14,g14,g11)
    c: Symmetric(g15,g15,g9)
    c: Parallel(g15,g11)
    c: Symmetric(g16,g16,g10)
    c: Coincident(g16,g14)
    c: Coincident(g15,g14)
    c: Coincident(g13,g15)
    c: Coincident(g9,g4)
FEATURE [Sketcher::SketchObject] Sketch057  label="buco interno per SWITCH"
  ArcFitTolerance = 1e-06
  AttachmentSupport = -> [XZ_Plane]
  ExternalGeometry = -> [Sketch]
  FullyConstrained = true
  MakeInternals = false
  MapMode = 5
  Placement = pos=(0,0,0) rot=(1,0,0;1.5708rad)
  sketch-geometry (10):
    g0: GeomPoint [constr] X=-187.821 Y=29.2 Z=0
    g1: LineSegment [constr] StartX=-188.505 StartY=27.3206 StartZ=0 EndX=-193.203 EndY=29.0307 EndZ=0
    g2: LineSegment [constr] StartX=-190.809 StartY=35.6086 StartZ=0 EndX=-195.597 EndY=22.4529 EndZ=0
    g3: GeomPoint [constr] X=-193.203 Y=29.0307 Z=0
    g4: LineSegment [constr] StartX=-196.492 StartY=30.2278 StartZ=0 EndX=-189.914 EndY=27.8336 EndZ=0
    g5: LineSegment StartX=-194.098 StartY=36.8056 StartZ=0 EndX=-187.52 EndY=34.4115 EndZ=0
    g6: LineSegment StartX=-194.098 StartY=36.8056 StartZ=0 EndX=-198.886 EndY=23.6499 EndZ=0
    g7: LineSegment StartX=-187.52 StartY=34.4115 StartZ=0 EndX=-192.308 EndY=21.2558 EndZ=0
    g8: LineSegment StartX=-198.886 StartY=23.6499 StartZ=0 EndX=-192.308 EndY=21.2558 EndZ=0
    g9: LineSegment [constr] StartX=-187.821 StartY=29.2 StartZ=0 EndX=-188.505 EndY=27.3206 EndZ=0
  constraints (23):
    c: Symmetric(g-3,g-3,g0)
    c: Perpendicular(g1,g-3)
    c: Parallel(g2,g-3)
    c: Symmetric(g2,g2,g3)
    c: Perpendicular(g2,g4)
    c: Symmetric(g4,g4,g3)
    c: Distance(g2) = 14
    c: Distance(g4) = 7
    c: Distance(g1) = 5
    c: Parallel(g5,g4)
    c: Parallel(g7,g2)
    c: Symmetric(g5,g5,g2)
    c: Symmetric(g6,g6,g4)
    c: Symmetric(g7,g7,g4)
    c: Symmetric(g8,g8,g2)
    c: Coincident(g6,g5)
    c: Coincident(g7,g5)
    c: Coincident(g8,g7)
    c: Coincident(g3,g1)
    c: Coincident(g9,g0)
    c: Parallel(g9,g-3)
    c: Distance(g9) = 2
    c: Coincident(g1,g9)
FEATURE [Sketcher::SketchObject] Sketch058  label="buco esterno per SWITCH"
  ArcFitTolerance = 1e-06
  AttachmentSupport = -> [XZ_Plane]
  ExternalGeometry = -> [Sketch057]
  FullyConstrained = true
  MakeInternals = false
  MapMode = 5
  Placement = pos=(0,0,0) rot=(1,0,0;1.5708rad)
  sketch-geometry (12):
    g0: GeomPoint [constr] X=-190.809 Y=35.6086 Z=0
    g1: GeomPoint [constr] X=-196.492 Y=30.2278 Z=0
    g2: GeomPoint [constr] X=-189.914 Y=27.8336 Z=0
    g3: GeomPoint [constr] X=-195.597 Y=22.4529 Z=0
    g4: GeomPoint [constr] X=-193.203 Y=29.0307 Z=0
    g5: LineSegment [constr] StartX=-192.006 StartY=32.3196 StartZ=0 EndX=-194.4 EndY=25.7418 EndZ=0
    g6: GeomPoint [constr] X=-193.203 Y=29.0307 Z=0
    g7: LineSegment [constr] StartX=-195.082 StartY=29.7148 StartZ=0 EndX=-191.324 EndY=28.3467 EndZ=0
    g8: LineSegment StartX=-193.885 StartY=33.0037 StartZ=0 EndX=-190.127 EndY=31.6356 EndZ=0
    g9: LineSegment StartX=-190.127 StartY=31.6356 StartZ=0 EndX=-192.521 EndY=25.0578 EndZ=0
    g10: LineSegment StartX=-196.28 StartY=26.4258 StartZ=0 EndX=-192.521 EndY=25.0578 EndZ=0
    g11: LineSegment StartX=-193.885 StartY=33.0037 StartZ=0 EndX=-196.28 EndY=26.4258 EndZ=0
  constraints (21):
    c: Symmetric(g-6,g-6,g3)
    c: Symmetric(g-4,g-6,g2)
    c: Symmetric(g-5,g-4,g0)
    c: Symmetric(g-5,g-6,g1)
    c: Symmetric(g1,g2,g4)
    c: Parallel(g5,g-4)
    c: Symmetric(g5,g5,g6)
    c: Perpendicular(g7,g5)
    c: Symmetric(g7,g7,g6)
    c: Distance(g5) = 7
    c: Distance(g7) = 4
    c: Parallel(g8,g7)
    c: Parallel(g11,g5)
    c: Symmetric(g8,g8,g5)
    c: Symmetric(g9,g9,g7)
    c: Symmetric(g10,g10,g5)
    c: Symmetric(g11,g11,g7)
    c: Coincident(g11,g8)
    c: Coincident(g9,g8)
    c: Coincident(g9,g10)
    c: Coincident(g6,g4)
FEATURE [Part::Extrusion] Extrude060  label="Extrude buco interno per SWITCH destro"
  Base = -> Sketch057
  Dir = (0,-1,2e-16)
  DirMode = 2
  FaceMakerClass = Part::FaceMakerBullseye
  FaceMakerMode = 3
  LengthFwd = 13.2
  LengthRev = 0
  Placement = pos=(0,2.6,0) rot=(0,0,1;0rad)
  Solid = true
  Symmetric = false
FEATURE [Part::Extrusion] Extrude061  label="Extrude buco esterno per SWITCH destro"
  Base = -> Sketch058
  Dir = (0,-1,2e-16)
  DirMode = 2
  FaceMakerClass = Part::FaceMakerBullseye
  FaceMakerMode = 3
  LengthFwd = 2
  LengthRev = 0
  Placement = pos=(0,-10.6,0) rot=(0,0,1;0rad)
  Solid = true
  Symmetric = false
FEATURE [Sketcher::SketchObject] Sketch059  label="buco per spazio introduzione SWITCH"
  ArcFitTolerance = 1e-06
  AttachmentSupport = -> [XZ_Plane]
  ExternalGeometry = -> [Sketch057,Sketch010]
  FullyConstrained = true
  MakeInternals = false
  MapMode = 5
  Placement = pos=(0,0,0) rot=(1,0,0;1.5708rad)
  sketch-geometry (8):
    g0: LineSegment [constr] StartX=-201.368 StartY=36.3521 StartZ=0 EndX=-195.094 EndY=34.0687 EndZ=0
    g1: LineSegment [constr] StartX=-194.098 StartY=36.8056 StartZ=0 EndX=-195.094 EndY=34.0687 EndZ=0
    g2: LineSegment StartX=-198.658 StartY=24.2771 StartZ=0 EndX=-199.654 EndY=21.5401 EndZ=0
    g3: LineSegment StartX=-199.654 StartY=21.5401 StartZ=0 EndX=-181.196 EndY=14.822 EndZ=0
    g4: LineSegment StartX=-181.196 StartY=14.822 StartZ=0 EndX=-180.2 EndY=17.559 EndZ=0
    g5: LineSegment StartX=-180.2 StartY=17.559 StartZ=0 EndX=-198.658 EndY=24.2771 EndZ=0
    g6: LineSegment [constr] StartX=-204.932 StartY=26.5605 StartZ=0 EndX=-198.658 EndY=24.2771 EndZ=0
    g7: LineSegment [constr] StartX=-198.658 StartY=24.2771 StartZ=0 EndX=-199.654 EndY=21.5401 EndZ=0
  constraints (20):
    c: Parallel(g1,g-3)
    c: Parallel(g0,g-4)
    c: Coincident(g0,g-4)
    c: Coincident(g1,g-3)
    c: Coincident(g0,g1)
    c: Coincident(g3,g2)
    c: Coincident(g4,g3)
    c: Coincident(g5,g4)
    c: Coincident(g5,g2)
    c: Parallel(g5,g-5)
    c: Parallel(g3,g-5)
    c: Parallel(g4,g-6)
    c: DistanceX(g-6,g4) = 0
    c: Coincident(g6,g-5)
    c: Equal(g6,g0)
    c: Coincident(g7,g6)
    c: Equal(g7,g1)
    c: Tangent(g7,g-3)
    c: Coincident(g2,g6)
    c: Coincident(g2,g7)
FEATURE [Part::Extrusion] Extrude062  label="Extrude buco per spazio introduzione SWITCH"
  Base = -> Sketch059
  Dir = (0,-1,2e-16)
  DirMode = 2
  FaceMakerClass = Part::FaceMakerBullseye
  FaceMakerMode = 3
  LengthFwd = 13.2
  LengthRev = 0
  Solid = true
  Symmetric = true
FEATURE [Part::Extrusion] Extrude063  label="Extrude buco interno per SWITCH sinistro"
  Base = -> Sketch057
  Dir = (0,-1,2e-16)
  DirMode = 2
  FaceMakerClass = Part::FaceMakerBullseye
  FaceMakerMode = 3
  LengthFwd = 13.2
  LengthRev = 0
  Placement = pos=(0,10.6,0) rot=(0,0,1;0rad)
  Solid = true
  Symmetric = false
FEATURE [Part::Extrusion] Extrude064  label="Extrude buco esterno per SWITCH sinistro"
  Base = -> Sketch058
  Dir = (0,-1,2e-16)
  DirMode = 2
  FaceMakerClass = Part::FaceMakerBullseye
  FaceMakerMode = 3
  LengthFwd = 2
  LengthRev = 0
  Placement = pos=(0,12.6,0) rot=(0,0,1;0rad)
  Solid = true
  Symmetric = false
FEATURE [Sketcher::SketchObject] Sketch061  label="struttura esterna blocco switch"
  ArcFitTolerance = 1e-06
  AttachmentSupport = -> [XZ_Plane003]
  FullyConstrained = true
  MakeInternals = false
  MapMode = 5
  Placement = pos=(0,0,0) rot=(1,0,0;1.5708rad)
  sketch-geometry (5):
    g0: LineSegment StartX=-1 StartY=-5.1 StartZ=0 EndX=1 EndY=-5.1 EndZ=0
    g1: LineSegment StartX=1 StartY=-5.1 StartZ=0 EndX=1 EndY=5.1 EndZ=0
    g2: LineSegment StartX=1 StartY=5.1 StartZ=0 EndX=-1 EndY=5.1 EndZ=0
    g3: LineSegment StartX=-1 StartY=5.1 StartZ=0 EndX=-1 EndY=-5.1 EndZ=0
    g4: GeomPoint [constr] X=0 Y=0 Z=0
  constraints (12):
    c: Coincident(g0,g1)
    c: Coincident(g1,g2)
    c: Coincident(g2,g3)
    c: Coincident(g3,g0)
    c: Horizontal(g0)
    c: Horizontal(g2)
    c: Vertical(g1)
    c: Vertical(g3)
    c: Symmetric(g2,g0,g4)
    c: Distance(g1,g3) = 2
    c: Distance(g0,g2) = 10.2
    c: Coincident(g4,g-1)
FEATURE [Sketcher::SketchObject] Sketch062  label="struttura interna blocco switch"
  ArcFitTolerance = 1e-06
  AttachmentSupport = -> [XZ_Plane003]
  ExternalGeometry = -> [Sketch061]
  FullyConstrained = true
  MakeInternals = false
  MapMode = 5
  Placement = pos=(0,0,0) rot=(1,0,0;1.5708rad)
  sketch-geometry (5):
    g0: LineSegment StartX=-1 StartY=3.1 StartZ=0 EndX=-1 EndY=-3.1 EndZ=0
    g1: LineSegment StartX=-1 StartY=-3.1 StartZ=0 EndX=1 EndY=-3.1 EndZ=0
    g2: LineSegment StartX=1 StartY=-3.1 StartZ=0 EndX=1 EndY=3.1 EndZ=0
    g3: LineSegment StartX=1 StartY=3.1 StartZ=0 EndX=-1 EndY=3.1 EndZ=0
    g4: GeomPoint [constr] X=0 Y=0 Z=0
  constraints (12):
    c: Coincident(g0,g1)
    c: Coincident(g1,g2)
    c: Coincident(g2,g3)
    c: Coincident(g3,g0)
    c: Vertical(g0)
    c: Vertical(g2)
    c: Horizontal(g1)
    c: Horizontal(g3)
    c: Symmetric(g2,g0,g4)
    c: Coincident(g4,g-1)
    c: Distance(g0) = 6.2
    c: Equal(g3,g-3)
FEATURE [Sketcher::SketchObject] Sketch063  label="blocchi tra switch"
  ArcFitTolerance = 1e-06
  AttachmentSupport = -> [XZ_Plane003]
  ExternalGeometry = -> [Sketch061,Sketch062]
  FullyConstrained = true
  MakeInternals = false
  MapMode = 5
  Placement = pos=(0,0,0) rot=(1,0,0;1.5708rad)
  sketch-geometry (8):
    g0: LineSegment StartX=-3 StartY=5.1 StartZ=0 EndX=-1 EndY=5.1 EndZ=0
    g1: LineSegment StartX=-1 StartY=5.1 StartZ=0 EndX=-1 EndY=3.1 EndZ=0
    g2: LineSegment StartX=-1 StartY=3.1 StartZ=0 EndX=-3 EndY=3.1 EndZ=0
    g3: LineSegment StartX=-3 StartY=3.1 StartZ=0 EndX=-3 EndY=5.1 EndZ=0
    g4: LineSegment StartX=-3 StartY=-3.1 StartZ=0 EndX=-1 EndY=-3.1 EndZ=0
    g5: LineSegment StartX=-1 StartY=-3.1 StartZ=0 EndX=-1 EndY=-5.1 EndZ=0
    g6: LineSegment StartX=-1 StartY=-5.1 StartZ=0 EndX=-3 EndY=-5.1 EndZ=0
    g7: LineSegment StartX=-3 StartY=-5.1 StartZ=0 EndX=-3 EndY=-3.1 EndZ=0
  constraints (20):
    c: Horizontal(g0)
    c: Coincident(g1,g0)
    c: Coincident(g2,g1)
    c: Horizontal(g2)
    c: Coincident(g3,g2)
    c: Coincident(g3,g0)
    c: Vertical(g3)
    c: Horizontal(g4)
    c: Coincident(g5,g4)
    c: Coincident(g6,g5)
    c: Horizontal(g6)
    c: Coincident(g7,g6)
    c: Coincident(g7,g4)
    c: Vertical(g7)
    c: Coincident(g0,g-4)
    c: Coincident(g1,g-5)
    c: Coincident(g4,g-6)
    c: Coincident(g5,g-7)
    c: Distance(g0) = 2
    c: Distance(g4) = 2
FEATURE [Sketcher::SketchObject] Sketch066  label="piano per rampino"
  ArcFitTolerance = 1e-06
  AttachmentSupport = -> [XZ_Plane002]
  ExternalGeometry = -> [Sketch045]
  FullyConstrained = true
  MakeInternals = false
  MapMode = 5
  Placement = pos=(0,0,0) rot=(1,0,0;1.5708rad)
  sketch-geometry (4):
    g0: LineSegment StartX=5.4 StartY=5.1 StartZ=0 EndX=5.4 EndY=3.9 EndZ=0
    g1: LineSegment StartX=5.4 StartY=3.9 StartZ=0 EndX=7 EndY=3.9 EndZ=0
    g2: LineSegment StartX=7 StartY=3.9 StartZ=0 EndX=7 EndY=5.1 EndZ=0
    g3: LineSegment StartX=7 StartY=5.1 StartZ=0 EndX=5.4 EndY=5.1 EndZ=0
  constraints (11):
    c: Coincident(g0,g1)
    c: Coincident(g1,g2)
    c: Coincident(g2,g3)
    c: Coincident(g3,g0)
    c: Vertical(g0)
    c: Vertical(g2)
    c: Horizontal(g1)
    c: Horizontal(g3)
    c: Distance(g0,g2) = 1.6
    c: Distance(g1,g3) = 1.2
    c: Coincident(g2,g-3)
FEATURE [Sketcher::SketchObject] Sketch064  label="rampini_per_serraggio_struttura"
  ArcFitTolerance = 1e-06
  AttachmentSupport = -> [XZ_Plane002]
  ExternalGeometry = -> [Sketch066,Sketch045]
  FullyConstrained = true
  MakeInternals = false
  MapMode = 5
  Placement = pos=(0,0,0) rot=(1,0,0;1.5708rad)
  sketch-geometry (7):
    g0: LineSegment StartX=7 StartY=5.1 StartZ=0 EndX=7 EndY=3.9 EndZ=0
    g1: LineSegment StartX=7 StartY=3.9 StartZ=0 EndX=9 EndY=3.9 EndZ=0
    g2: LineSegment StartX=7 StartY=5.1 StartZ=0 EndX=7 EndY=5.1 EndZ=0
    g3: LineSegment StartX=7 StartY=5.1 StartZ=0 EndX=7 EndY=7.5 EndZ=0
    g4: LineSegment StartX=9 StartY=5.1 StartZ=0 EndX=9 EndY=3.9 EndZ=0
    g5: LineSegment StartX=7 StartY=7.5 StartZ=0 EndX=9 EndY=7.5 EndZ=0
    g6: LineSegment StartX=9 StartY=7.5 StartZ=0 EndX=9 EndY=5.1 EndZ=0
  constraints (20):
    c: Vertical(g0)
    c: Coincident(g1,g0)
    c: Horizontal(g1)
    c: Coincident(g2,g0)
    c: Horizontal(g2)
    c: Coincident(g3,g2)
    c: Vertical(g3)
    c: Coincident(g5,g3)
    c: Coincident(g4,g6)
    c: Coincident(g4,g1)
    c: Vertical(g4)
    c: Coincident(g0,g-3)
    c: DistanceY(g-4,g3) = 2.4
    c: DistanceX(g1,g1) = 2
    c: DistanceY(g2,g6) = 0
    c: DistanceX(g2,g2) = 0
    c: DistanceY(g0,g0) = 1.2
    c: Coincident(g5,g6)
    c: Horizontal(g5)
    c: Vertical(g6)
FEATURE [Sketcher::SketchObject] Sketch067  label="perno per blocco switch"
  ArcFitTolerance = 1e-06
  AttachmentSupport = -> [XZ_Plane]
  ExternalGeometry = -> [Sketch,Sketch010]
  FullyConstrained = true
  MakeInternals = false
  MapMode = 5
  Placement = pos=(0,0,0) rot=(1,0,0;1.5708rad)
  sketch-geometry (14):
    g0: LineSegment StartX=-191.073 StartY=24.9429 StartZ=0 EndX=-185.81 EndY=23.0276 EndZ=0
    g1: LineSegment StartX=-183.76 StartY=23.9839 StartZ=0 EndX=-182.392 EndY=27.7427 EndZ=0
    g2: LineSegment StartX=-183.348 StartY=29.7934 StartZ=0 EndX=-188.61 EndY=31.7087 EndZ=0
    g3: LineSegment StartX=-188.61 StartY=31.7087 StartZ=0 EndX=-191.073 EndY=24.9429 EndZ=0
    g4: GeomPoint [constr] X=-186.459 Y=27.0946 Z=0
    g5: LineSegment StartX=-189.022 StartY=25.8992 StartZ=0 EndX=-185.263 EndY=24.5311 EndZ=0
    g6: LineSegment StartX=-185.263 StartY=24.5311 StartZ=0 EndX=-183.895 EndY=28.2899 EndZ=0
    g7: LineSegment StartX=-183.895 StartY=28.2899 StartZ=0 EndX=-187.654 EndY=29.658 EndZ=0
    g8: LineSegment StartX=-187.654 StartY=29.658 StartZ=0 EndX=-189.022 EndY=25.8992 EndZ=0
    g9: GeomPoint [constr] X=-186.459 Y=27.0946 Z=0
    g10: ArcOfCircle CenterX=-185.263 CenterY=24.5311 CenterZ=0 NormalX=0 NormalY=0 NormalZ=1 AngleXU=0 Radius=1.6 StartAngle=4.36332 EndAngle=5.93412
    g11: GeomPoint [constr] X=-184.307 Y=22.4804 Z=0
    g12: ArcOfCircle CenterX=-183.895 CenterY=28.2899 CenterZ=0 NormalX=0 NormalY=0 NormalZ=1 AngleXU=0 Radius=1.6 StartAngle=5.93412 EndAngle=7.50492
    g13: GeomPoint [constr] X=-181.844 Y=29.2462 Z=0
  constraints (30):
    c: Coincident(g2,g3)
    c: Coincident(g3,g0)
    c: Symmetric(g13,g0,g4)
    c: Distance(g11,g3) = 7.2
    c: Distance(g0,g2) = 7.2
    c: Parallel(g3,g1)
    c: Parallel(g2,g0)
    c: Perpendicular(g2,g3)
    c: Coincident(g5,g6)
    c: Coincident(g6,g7)
    c: Coincident(g7,g8)
    c: Coincident(g8,g5)
    c: Symmetric(g7,g5,g9)
    c: Distance(g6,g8) = 4
    c: Distance(g5,g7) = 4
    c: Coincident(g9,g4)
    c: Parallel(g8,g6)
    c: Parallel(g7,g5)
    c: Perpendicular(g7,g8)
    c: Tangent(g8,g-3)
    c: Tangent(g2,g-4)
    c: PointOnObject(g11,g1)
    c: PointOnObject(g11,g0)
    c: Tangent(g1,g10) = -1.5708
    c: Tangent(g0,g10) = -1.5708
    c: PointOnObject(g13,g1)
    c: Tangent(g1,g12) = -1.5708
    c: Tangent(g2,g12) = -1.5708
    c: Equal(g10,g12)
    c: Coincident(g10,g5)
FEATURE [Part::Extrusion] Extrude072  label="Extrude perno per blocco switch"
  Base = -> Sketch067
  Dir = (0,-1,2e-16)
  DirMode = 2
  FaceMakerClass = Part::FaceMakerBullseye
  FaceMakerMode = 3
  LengthFwd = 25.2
  LengthRev = 0
  Solid = true
  Symmetric = true
FEATURE [Part::MultiFuse] Fusion
  Refine = true
  Shapes = -> [Extrude,Sweep,Extrude007,Extrude011,Extrude005,Extrude012,Extrude013,Extrude016,Extrude031,Extrude039,Extrude045,Extrude072]
FEATURE [Part::Cut] Cut
  Base = -> Fusion
  Refine = true
  Tool = -> Extrude001
FEATURE [Part::Cut] Cut001
  Base = -> Cut
  Refine = true
  Tool = -> Extrude004
FEATURE [Part::Cut] Cut002
  Base = -> Cut001
  Refine = true
  Tool = -> Extrude006
FEATURE [Part::Cut] Cut003
  Base = -> Cut002
  Refine = true
  Tool = -> Extrude008
FEATURE [Part::Cut] Cut004
  Base = -> Cut003
  Refine = true
  Tool = -> Extrude009
FEATURE [Part::Cut] Cut005
  Base = -> Cut004
  Refine = true
  Tool = -> Extrude010
FEATURE [Part::Cut] Cut006
  Base = -> Cut005
  Refine = true
  Tool = -> Extrude014
FEATURE [Part::Cut] Cut007
  Base = -> Cut006
  Refine = true
  Tool = -> Extrude015
FEATURE [Part::Cut] Cut008
  Base = -> Cut007
  Refine = true
  Tool = -> Extrude018
FEATURE [Part::Cut] Cut009
  Base = -> Cut008
  Refine = true
  Tool = -> Extrude019
FEATURE [Part::Cut] Cut010
  Base = -> Cut009
  Refine = true
  Tool = -> Extrude020
FEATURE [Part::Cut] Cut011
  Base = -> Cut010
  Refine = true
  Tool = -> Extrude021
FEATURE [Part::Cut] Cut012
  Base = -> Cut011
  Refine = true
  Tool = -> Extrude022
FEATURE [Part::Cut] Cut013
  Base = -> Cut012
  Refine = true
  Tool = -> Extrude023
FEATURE [Part::Cut] Cut014
  Base = -> Cut013
  Refine = true
  Tool = -> Extrude032
FEATURE [Part::Cut] Cut015
  Base = -> Cut014
  Refine = true
  Tool = -> Extrude033
FEATURE [Part::Cut] Cut016
  Base = -> Cut015
  Refine = true
  Tool = -> Extrude034
FEATURE [Part::Cut] Cut017
  Base = -> Cut016
  Refine = true
  Tool = -> Extrude035
FEATURE [Part::Cut] Cut018
  Base = -> Cut017
  Refine = true
  Tool = -> Extrude036
FEATURE [Part::Cut] Cut019
  Base = -> Cut018
  Refine = true
  Tool = -> Extrude037
FEATURE [Part::Cut] Cut020
  Base = -> Cut019
  Refine = true
  Tool = -> Extrude030
FEATURE [Part::Cut] Cut022
  Base = -> Cut020
  Refine = true
  Tool = -> Extrude038
FEATURE [Part::Cut] Cut023
  Base = -> Cut022
  Refine = true
  Tool = -> Extrude041
FEATURE [Part::Cut] Cut024
  Base = -> Cut023
  Refine = true
  Tool = -> Extrude040
FEATURE [Part::Cut] Cut025
  Base = -> Cut024
  Refine = true
  Tool = -> Extrude042
FEATURE [Part::Cut] Cut026
  Base = -> Cut025
  Refine = true
  Tool = -> Extrude043
FEATURE [Part::Cut] Cut027
  Base = -> Cut026
  Refine = true
  Tool = -> Extrude044
FEATURE [Part::Cut] Cut028
  Base = -> Cut027
  Refine = true
  Tool = -> Extrude046
FEATURE [Part::Cut] Cut029
  Base = -> Cut028
  Refine = true
  Tool = -> Extrude047
FEATURE [Part::Cut] Cut033
  Base = -> Cut029
  Refine = true
  Tool = -> Extrude055
FEATURE [Part::Cut] Cut034
  Base = -> Cut033
  Refine = true
  Tool = -> Extrude056
FEATURE [Part::Cut] Cut035
  Base = -> Cut034
  Refine = true
  Tool = -> Extrude057
FEATURE [Part::Cut] Cut037
  Base = -> Cut035
  Refine = true
  Tool = -> Extrude060
FEATURE [Part::Cut] Cut038
  Base = -> Cut037
  Refine = true
  Tool = -> Extrude061
FEATURE [Part::Cut] Cut039
  Base = -> Cut038
  Refine = true
  Tool = -> Extrude063
FEATURE [Part::Cut] Cut040
  Base = -> Cut039
  Refine = true
  Tool = -> Extrude064
FEATURE [Part::Cut] Cut041
  Base = -> Cut040
  Refine = true
  Tool = -> Extrude062
FEATURE [Sketcher::SketchObject] Sketch068  label="base con smusso sopra neopixel"
  ArcFitTolerance = 1e-06
  AttachmentSupport = -> [YZ_Plane002]
  FullyConstrained = true
  MakeInternals = false
  MapMode = 5
  Placement = pos=(0,0,0) rot=(0.57735,0.57735,0.57735;2.0944rad)
  sketch-geometry (5):
    g0: LineSegment StartX=-9.5 StartY=-6.1 StartZ=0 EndX=9.5 EndY=-6.1 EndZ=0
    g1: LineSegment StartX=9.5 StartY=-6.1 StartZ=0 EndX=9.5 EndY=6.1 EndZ=0
    g2: LineSegment StartX=9.5 StartY=6.1 StartZ=0 EndX=-9.5 EndY=6.1 EndZ=0
    g3: LineSegment StartX=-9.5 StartY=6.1 StartZ=0 EndX=-9.5 EndY=-6.1 EndZ=0
    g4: GeomPoint [constr] X=0 Y=0 Z=0
  constraints (12):
    c: Coincident(g0,g1)
    c: Coincident(g1,g2)
    c: Coincident(g2,g3)
    c: Coincident(g3,g0)
    c: Horizontal(g0)
    c: Horizontal(g2)
    c: Vertical(g1)
    c: Vertical(g3)
    c: Symmetric(g2,g0,g4)
    c: Distance(g1,g3) = 19
    c: Distance(g0,g2) = 12.2
    c: Coincident(g4,g-1)
FEATURE [Sketcher::SketchObject] Sketch069  label="cilindro minore"
  ArcFitTolerance = 1e-06
  AttachmentSupport = -> [XZ_Plane004]
  FullyConstrained = true
  MakeInternals = false
  MapMode = 5
  Placement = pos=(0,0,0) rot=(1,0,0;1.5708rad)
  sketch-geometry (1):
    g0: Circle CenterX=0 CenterY=0 CenterZ=0 NormalX=0 NormalY=0 NormalZ=1 AngleXU=0 Radius=5.8
  constraints (2):
    c: Diameter(g0) = 11.6
    c: Coincident(g0,g-1)
FEATURE [Sketcher::SketchObject] Sketch070  label="cilindro maggiore"
  ArcFitTolerance = 1e-06
  AttachmentSupport = -> [XZ_Plane004]
  ExternalGeometry = -> [Sketch069]
  FullyConstrained = true
  MakeInternals = false
  MapMode = 5
  Placement = pos=(0,0,0) rot=(1,0,0;1.5708rad)
  sketch-geometry (1):
    g0: Circle CenterX=0 CenterY=0 CenterZ=0 NormalX=0 NormalY=0 NormalZ=1 AngleXU=0 Radius=6.5
  constraints (2):
    c: Coincident(g0,g-1)
    c: Diameter(g0) = 13
FEATURE [Sketcher::SketchObject] Sketch071  label="buco interno"
  ArcFitTolerance = 1e-06
  AttachmentSupport = -> [XZ_Plane004]
  ExternalGeometry = -> [Sketch069]
  FullyConstrained = true
  MakeInternals = false
  MapMode = 5
  Placement = pos=(0,0,0) rot=(1,0,0;1.5708rad)
  sketch-geometry (1):
    g0: Circle CenterX=0 CenterY=0 CenterZ=0 NormalX=0 NormalY=0 NormalZ=1 AngleXU=0 Radius=5
  constraints (2):
    c: Coincident(g0,g-1)
    c: Diameter(g0) = 10
FEATURE [PartDesign::Pad] Pad
  Direction = (0,-1,2e-16)
  Length = 1.2
  Length2 = 10
  Placement = pos=(0,0,0) rot=(1,0,0;1.5708rad)
  Profile = -> Sketch070
  ReferenceAxis = -> Sketch070 [N_Axis]
  Refine = true
  Suppressed = false
  Type = 0
FEATURE [PartDesign::Pad] Pad001
  BaseFeature = -> Pad
  Direction = (0,-1,2e-16)
  Length = 5.6
  Length2 = 10
  Placement = pos=(0,0,0) rot=(1,0,0;1.5708rad)
  Profile = -> Sketch069
  ReferenceAxis = -> Sketch069 [N_Axis]
  Refine = true
  Suppressed = false
  Type = 0
FEATURE [PartDesign::Pocket] Pocket
  BaseFeature = -> Pad001
  Direction = (0,1,-2e-16)
  Length = 7
  Length2 = 5
  Midplane = true
  Placement = pos=(0,0,0) rot=(1,0,0;1.5708rad)
  Profile = -> Sketch071
  ReferenceAxis = -> Sketch071 [N_Axis]
  Refine = true
  Suppressed = false
  Type = 0
FEATURE [PartDesign::Fillet] Fillet
  Base = -> Pocket [Face7]
  BaseFeature = -> Pocket
  Placement = pos=(0,0,0) rot=(1,0,0;1.5708rad)
  Radius = 1
  Refine = true
  SupportTransform = false
  Suppressed = false
  UseAllEdges = false
FEATURE [PartDesign::Body] Body004  label="pulsanti lato sinistro"
  AllowCompound = false
  Group = -> [Sketch069,Sketch070,Sketch071,Pad,Pad001,Pocket,Fillet]
  Origin = -> Origin004
  Tip = -> Fillet
FEATURE [Sketcher::SketchObject] Sketch072  label="buco per saldature e diodo driver solenoide"
  ArcFitTolerance = 1e-06
  AttachmentSupport = -> [XZ_Plane]
  ExternalGeometry = -> [Sketch038]
  FullyConstrained = true
  MakeInternals = false
  MapMode = 5
  Placement = pos=(0,0,0) rot=(1,0,0;1.5708rad)
  sketch-geometry (4):
    g0: LineSegment StartX=-209.225 StartY=-40.6939 StartZ=0 EndX=-204.154 EndY=-29.8182 EndZ=0
    g1: LineSegment StartX=-204.154 StartY=-29.8182 StartZ=0 EndX=-206.51 EndY=-28.7194 EndZ=0
    g2: LineSegment StartX=-206.51 StartY=-28.7194 StartZ=0 EndX=-211.582 EndY=-39.5951 EndZ=0
    g3: LineSegment StartX=-211.582 StartY=-39.5951 StartZ=0 EndX=-209.225 EndY=-40.6939 EndZ=0
  constraints (11):
    c: Coincident(g1,g0)
    c: Coincident(g2,g1)
    c: Coincident(g3,g2)
    c: Coincident(g3,g0)
    c: Parallel(g-3,g0)
    c: Parallel(g0,g2)
    c: Perpendicular(g0,g3)
    c: Perpendicular(g1,g0)
    c: Distance(g3) = 2.6
    c: Distance(g2) = 12
    c: Coincident(g0,g-3)
FEATURE [Part::Extrusion] Extrude074  label="Extrude buco per saldature e diodo driver solenoide"
  Base = -> Sketch072
  Dir = (0,-1,2e-16)
  DirMode = 2
  FaceMakerClass = Part::FaceMakerBullseye
  FaceMakerMode = 3
  LengthFwd = 14.6
  LengthRev = 0
  Solid = true
  Symmetric = true
FEATURE [Part::Cut] Cut042
  Base = -> Cut041
  Refine = true
  Tool = -> Extrude074
FEATURE [Sketcher::SketchObject] Sketch073  label="fori slargati blocco solenoide"
  ArcFitTolerance = 1e-06
  AttachmentSupport = -> [XY_Plane]
  ExternalGeometry = -> [Sketch030]
  FullyConstrained = true
  MakeInternals = false
  MapMode = 5
  sketch-geometry (2):
    g0: Circle CenterX=-152.209 CenterY=6.95 CenterZ=0 NormalX=0 NormalY=0 NormalZ=1 AngleXU=0 Radius=3.7
    g1: Circle CenterX=-130.41 CenterY=-6.95 CenterZ=0 NormalX=0 NormalY=0 NormalZ=1 AngleXU=0 Radius=3.7
  constraints (4):
    c: Diameter(g0) = 7.4
    c: Coincident(g0,g-3)
    c: Diameter(g1) = 7.4
    c: Coincident(g1,g-4)
FEATURE [Part::Extrusion] Extrude075  label="Extrude fori slargati blocco solenoide"
  Base = -> Sketch073
  Dir = (0,0,1)
  DirMode = 2
  FaceMakerClass = Part::FaceMakerBullseye
  FaceMakerMode = 3
  LengthFwd = 1.5
  LengthRev = 0
  Placement = pos=(0,0,36.4) rot=(0,0,1;0rad)
  Solid = true
  Symmetric = false
FEATURE [Part::Cut] Cut043
  Base = -> Cut042
  Refine = true
  Tool = -> Extrude075
FEATURE [Sketcher::SketchObject] Sketch074  label="lato sx pistola"
  ArcFitTolerance = 1e-06
  AttachmentSupport = -> [XZ_Plane]
  ExternalGeometry = -> [Sketch016,Sketch,Sketch058]
  FullyConstrained = true
  MakeInternals = false
  MapMode = 5
  Placement = pos=(0,0,0) rot=(1,0,0;1.5708rad)
  sketch-geometry (37):
    g0: LineSegment StartX=-82.8 StartY=3.2 StartZ=0 EndX=0 EndY=3.2 EndZ=0
    g1: LineSegment StartX=-82.8 StartY=3.2 StartZ=0 EndX=-82.8 EndY=6.2 EndZ=0
    g2: LineSegment [constr] StartX=-107.6 StartY=18 StartZ=0 EndX=-107.6 EndY=20 EndZ=0
    g3: LineSegment [constr] StartX=-132.428 StartY=18 StartZ=0 EndX=-132.428 EndY=20 EndZ=0
    g4: LineSegment StartX=-132.428 StartY=20 StartZ=0 EndX=-107.6 EndY=20 EndZ=0
    g5: ArcOfCircle CenterX=-107.6 CenterY=4 CenterZ=0 NormalX=0 NormalY=0 NormalZ=1 AngleXU=0 Radius=16 StartAngle=0.137937 EndAngle=1.5708
    g6: LineSegment StartX=-82.8 StartY=6.2 StartZ=0 EndX=-91.752 EndY=6.2 EndZ=0
    g7: LineSegment [constr] StartX=-145.743 StartY=8.32624 StartZ=0 EndX=-147.645 EndY=8.94427 EndZ=0
    g8: ArcOfCircle CenterX=-132.428 CenterY=4 CenterZ=0 NormalX=0 NormalY=0 NormalZ=1 AngleXU=0 Radius=16 StartAngle=1.5708 EndAngle=2.82743
    g9: LineSegment StartX=-215.932 StartY=-80.4316 StartZ=0 EndX=-176.685 EndY=-80.4316 EndZ=0
    g10: LineSegment StartX=-147.645 StartY=8.94427 StartZ=0 EndX=-176.685 EndY=-80.4316 EndZ=0
    g11: LineSegment [constr] StartX=-193.988 StartY=-2.33927 StartZ=0 EndX=-192.176 EndY=-3.18451 EndZ=0
    g12: LineSegment [constr] StartX=-217.232 StartY=-52.1862 StartZ=0 EndX=-215.42 EndY=-53.0314 EndZ=0
    g13: LineSegment StartX=-192.176 StartY=-3.18451 StartZ=0 EndX=-215.42 EndY=-53.0314 EndZ=0
    g14: ArcOfCircle CenterX=-184.801 CenterY=-67.3089 CenterZ=0 NormalX=0 NormalY=0 NormalZ=1 AngleXU=0 Radius=33.7833 StartAngle=2.70526 EndAngle=3.54053
    g15: ArcOfCircle CenterX=-207.583 CenterY=4 CenterZ=0 NormalX=0 NormalY=0 NormalZ=1 AngleXU=0 Radius=17 StartAngle=5.84685 EndAngle=7.56663
    g16: LineSegment StartX=-202.765 StartY=20.303 StartZ=0 EndX=-195.887 EndY=39.2 EndZ=0
    g17: LineSegment [constr] StartX=-193.885 StartY=33.0037 StartZ=0 EndX=-197.644 EndY=34.3718 EndZ=0
    g18: LineSegment StartX=-195.887 StartY=39.2 StartZ=0 EndX=0 EndY=39.2 EndZ=0
    g19: LineSegment StartX=0 StartY=3.2 StartZ=0 EndX=0 EndY=39.2 EndZ=0
    g20: LineSegment StartX=-189.939 StartY=31.5672 StartZ=0 EndX=-192.333 EndY=24.9893 EndZ=0
    g21: LineSegment StartX=-196.467 StartY=26.4942 StartZ=0 EndX=-194.073 EndY=33.0721 EndZ=0
    g22: Circle CenterX=-213.443 CenterY=-76.8316 CenterZ=0 NormalX=0 NormalY=0 NormalZ=1 AngleXU=0 Radius=1.8
    g23: Circle CenterX=-179.305 CenterY=-76.8316 CenterZ=0 NormalX=0 NormalY=0 NormalZ=1 AngleXU=0 Radius=1.8
    g24: Circle CenterX=-184.08 CenterY=34.8 CenterZ=0 NormalX=0 NormalY=0 NormalZ=1 AngleXU=0 Radius=1.8
    g25: Circle CenterX=-78.51 CenterY=34.8 CenterZ=0 NormalX=0 NormalY=0 NormalZ=1 AngleXU=0 Radius=1.8
    g26: Circle CenterX=-78.51 CenterY=7.6 CenterZ=0 NormalX=0 NormalY=0 NormalZ=1 AngleXU=0 Radius=1.8
    g27: Circle CenterX=-5.6 CenterY=34.8 CenterZ=0 NormalX=0 NormalY=0 NormalZ=1 AngleXU=0 Radius=1.8
    g28: Circle CenterX=-5.6 CenterY=7.6 CenterZ=0 NormalX=0 NormalY=0 NormalZ=1 AngleXU=0 Radius=1.8
    g29: LineSegment StartX=-190.127 StartY=31.6356 StartZ=0 EndX=-189.939 EndY=31.5672 EndZ=0
    g30: LineSegment StartX=-194.073 StartY=33.0721 StartZ=0 EndX=-193.885 EndY=33.0037 EndZ=0
    g31: LineSegment StartX=-193.885 StartY=33.0037 StartZ=0 EndX=-190.127 EndY=31.6356 EndZ=0
    g32: LineSegment StartX=-196.467 StartY=26.4942 StartZ=0 EndX=-192.333 EndY=24.9893 EndZ=0
    g33: Circle CenterX=-19 CenterY=21.2 CenterZ=0 NormalX=0 NormalY=0 NormalZ=1 AngleXU=0 Radius=6.3
    g34: Circle CenterX=-42 CenterY=21.2 CenterZ=0 NormalX=0 NormalY=0 NormalZ=1 AngleXU=0 Radius=6.3
    g35: Circle CenterX=-65 CenterY=21.2 CenterZ=0 NormalX=0 NormalY=0 NormalZ=1 AngleXU=0 Radius=6.3
    g36: LineSegment [constr] StartX=-4 StartY=21.2 StartZ=0 EndX=-65 EndY=21.2 EndZ=0
  constraints (96):
    c: Coincident(g0,g-41)
    c: Horizontal(g0)
    c: PointOnObject(g0,g-39)
    c: Coincident(g1,g0)
    c: Vertical(g1)
    c: DistanceY(g1,g1) = 3
    c: Coincident(g2,g-17)
    c: Vertical(g2)
    c: Coincident(g3,g-16)
    c: Vertical(g3)
    c: DistanceY(g2,g2) = 2
    c: DistanceY(g3,g3) = 2
    c: Coincident(g4,g3)
    c: Coincident(g4,g2)
    c: Coincident(g5,g-17)
    c: Coincident(g5,g2)
    c: Coincident(g6,g1)
    c: Horizontal(g6)
    c: Coincident(g6,g5)
    c: Coincident(g7,g-15)
    c: Coincident(g8,g7)
    c: Coincident(g8,g3)
    c: Coincident(g8,g-15)
    c: Horizontal(g9)
    c: DistanceY(g-13,g9) = 2
    c: Coincident(g10,g7)
    c: Parallel(g10,g-14)
    c: Coincident(g9,g10)
    c: Distance(g11) = 2
    c: Coincident(g11,g-11)
    c: Perpendicular(g-11,g11)
    c: Distance(g12) = 2
    c: Coincident(g12,g-12)
    c: Perpendicular(g-11,g12)
    c: Coincident(g13,g11)
    c: Coincident(g13,g12)
    c: Coincident(g14,g-32)
    c: Coincident(g14,g12)
    c: Coincident(g14,g9)
    c: Coincident(g15,g-10)
    c: Coincident(g15,g11)
    c: Parallel(g16,g-22)
    c: Distance(g17) = 4
    c: PointOnObject(g17,g16)
    c: Coincident(g15,g16)
    c: Horizontal(g18)
    c: Coincident(g18,g16)
    c: Coincident(g19,g0)
    c: PointOnObject(g19,g-39)
    c: DistanceY(g19,g-36) = 2
    c: Coincident(g18,g19)
    c: Diameter(g22) = 3.6
    c: Coincident(g22,g-9)
    c: Diameter(g23) = 3.6
    c: Coincident(g23,g-8)
    c: Diameter(g24) = 3.6
    c: Diameter(g25) = 3.6
    c: Diameter(g26) = 3.6
    c: Diameter(g27) = 3.6
    c: Diameter(g28) = 3.6
    c: Coincident(g27,g-4)
    c: Coincident(g28,g-3)
    c: Coincident(g25,g-6)
    c: Coincident(g26,g-5)
    c: Coincident(g24,g-7)
    c: Parallel(g20,g-21)
    c: Equal(g20,g-21)
    c: Parallel(g21,g-19)
    c: Equal(g21,g-19)
    c: Distance(g29) = 0.2
    c: Distance(g30) = 0.2
    c: Parallel(g29,g-20)
    c: Parallel(g31,g-20)
    c: Equal(g31,g-20)
    c: Coincident(g30,g31)
    c: Coincident(g31,g29)
    c: Coincident(g29,g-21)
    c: Parallel(g30,g31)
    c: Coincident(g17,g30)
    c: Coincident(g20,g29)
    c: Coincident(g21,g30)
    c: Perpendicular(g16,g17)
    c: Coincident(g32,g21)
    c: Coincident(g32,g20)
    c: Perpendicular(g10,g7)
    c: Diameter(g33) = 12.6
    c: Diameter(g34) = 12.6
    c: Diameter(g35) = 12.6
    c: Horizontal(g36)
    c: PointOnObject(g33,g36)
    c: PointOnObject(g34,g36)
    c: DistanceX(g34,g33) = 23
    c: DistanceX(g35,g34) = 23
    c: DistanceX(g33,g36) = 15
    c: Symmetric(g-24,g-24,g36)
    c: Coincident(g36,g35)
FEATURE [Sketcher::SketchObject] Sketch075  label="lato dx pistola"
  ArcFitTolerance = 1e-06
  AttachmentSupport = -> [XZ_Plane]
  ExternalGeometry = -> [Sketch016,Sketch,Sketch058,Sketch074]
  FullyConstrained = true
  MakeInternals = false
  MapMode = 5
  Placement = pos=(0,0,0) rot=(1,0,0;1.5708rad)
  sketch-geometry (61):
    g0: LineSegment StartX=-82.8 StartY=3.2 StartZ=0 EndX=0 EndY=3.2 EndZ=0
    g1: LineSegment StartX=-82.8 StartY=3.2 StartZ=0 EndX=-82.8 EndY=6.2 EndZ=0
    g2: LineSegment [constr] StartX=-107.6 StartY=18 StartZ=0 EndX=-107.6 EndY=20 EndZ=0
    g3: LineSegment [constr] StartX=-132.428 StartY=18 StartZ=0 EndX=-132.428 EndY=20 EndZ=0
    g4: LineSegment StartX=-132.428 StartY=20 StartZ=0 EndX=-107.6 EndY=20 EndZ=0
    g5: ArcOfCircle CenterX=-107.6 CenterY=4 CenterZ=0 NormalX=0 NormalY=0 NormalZ=1 AngleXU=0 Radius=16 StartAngle=0.137937 EndAngle=1.5708
    g6: LineSegment StartX=-82.8 StartY=6.2 StartZ=0 EndX=-91.752 EndY=6.2 EndZ=0
    g7: LineSegment [constr] StartX=-145.743 StartY=8.32624 StartZ=0 EndX=-147.645 EndY=8.94427 EndZ=0
    g8: ArcOfCircle CenterX=-132.428 CenterY=4 CenterZ=0 NormalX=0 NormalY=0 NormalZ=1 AngleXU=0 Radius=16 StartAngle=1.5708 EndAngle=2.82743
    g9: LineSegment StartX=-215.932 StartY=-80.4316 StartZ=0 EndX=-176.685 EndY=-80.4316 EndZ=0
    g10: LineSegment StartX=-147.645 StartY=8.94427 StartZ=0 EndX=-176.685 EndY=-80.4316 EndZ=0
    g11: LineSegment [constr] StartX=-193.988 StartY=-2.33927 StartZ=0 EndX=-192.176 EndY=-3.18451 EndZ=0
    g12: LineSegment [constr] StartX=-217.232 StartY=-52.1862 StartZ=0 EndX=-215.42 EndY=-53.0314 EndZ=0
    g13: LineSegment StartX=-192.176 StartY=-3.18451 StartZ=0 EndX=-215.42 EndY=-53.0314 EndZ=0
    g14: ArcOfCircle CenterX=-184.801 CenterY=-67.3089 CenterZ=0 NormalX=0 NormalY=0 NormalZ=1 AngleXU=0 Radius=33.7833 StartAngle=2.70526 EndAngle=3.54053
    g15: ArcOfCircle CenterX=-207.583 CenterY=4 CenterZ=0 NormalX=0 NormalY=0 NormalZ=1 AngleXU=0 Radius=17 StartAngle=5.84685 EndAngle=7.56663
    g16: LineSegment StartX=-202.765 StartY=20.303 StartZ=0 EndX=-195.887 EndY=39.2 EndZ=0
    g17: LineSegment [constr] StartX=-193.885 StartY=33.0037 StartZ=0 EndX=-197.644 EndY=34.3718 EndZ=0
    g18: LineSegment StartX=-195.887 StartY=39.2 StartZ=0 EndX=0 EndY=39.2 EndZ=0
    g19: LineSegment StartX=0 StartY=3.2 StartZ=0 EndX=0 EndY=39.2 EndZ=0
    g20: LineSegment StartX=-189.939 StartY=31.5672 StartZ=0 EndX=-192.333 EndY=24.9893 EndZ=0
    g21: LineSegment StartX=-196.467 StartY=26.4942 StartZ=0 EndX=-194.073 EndY=33.0721 EndZ=0
    g22: Circle CenterX=-213.443 CenterY=-76.8316 CenterZ=0 NormalX=0 NormalY=0 NormalZ=1 AngleXU=0 Radius=1.8
    g23: Circle CenterX=-179.305 CenterY=-76.8316 CenterZ=0 NormalX=0 NormalY=0 NormalZ=1 AngleXU=0 Radius=1.8
    g24: Circle CenterX=-184.08 CenterY=34.8 CenterZ=0 NormalX=0 NormalY=0 NormalZ=1 AngleXU=0 Radius=1.8
    g25: Circle CenterX=-78.51 CenterY=34.8 CenterZ=0 NormalX=0 NormalY=0 NormalZ=1 AngleXU=0 Radius=1.8
    g26: Circle CenterX=-78.51 CenterY=7.6 CenterZ=0 NormalX=0 NormalY=0 NormalZ=1 AngleXU=0 Radius=1.8
    g27: Circle CenterX=-5.6 CenterY=34.8 CenterZ=0 NormalX=0 NormalY=0 NormalZ=1 AngleXU=0 Radius=1.8
    g28: Circle CenterX=-5.6 CenterY=7.6 CenterZ=0 NormalX=0 NormalY=0 NormalZ=1 AngleXU=0 Radius=1.8
    g29: LineSegment StartX=-190.127 StartY=31.6356 StartZ=0 EndX=-189.939 EndY=31.5672 EndZ=0
    g30: LineSegment StartX=-194.073 StartY=33.0721 StartZ=0 EndX=-193.885 EndY=33.0037 EndZ=0
    g31: LineSegment StartX=-193.885 StartY=33.0037 StartZ=0 EndX=-190.127 EndY=31.6356 EndZ=0
    g32: LineSegment StartX=-196.467 StartY=26.4942 StartZ=0 EndX=-192.333 EndY=24.9893 EndZ=0
    g33: LineSegment [constr] StartX=-4 StartY=21.2 StartZ=0 EndX=-87.91 EndY=21.2 EndZ=0
    g34: GeomPoint [constr] X=-4 Y=21.2 Z=0
    g35: LineSegment [constr] StartX=-15.2 StartY=33.7 StartZ=0 EndX=-15.2 EndY=8.7 EndZ=0
    g36: LineSegment [constr] StartX=-15.2 StartY=33.7 StartZ=0 EndX=-56.2 EndY=33.7 EndZ=0
    g37: LineSegment [constr] StartX=-15.2 StartY=8.7 StartZ=0 EndX=-56.2 EndY=8.7 EndZ=0
    g38: LineSegment [constr] StartX=-56.2 StartY=33.7 StartZ=0 EndX=-56.2 EndY=8.7 EndZ=0
    g39: Circle CenterX=-18.6 CenterY=30.3 CenterZ=0 NormalX=0 NormalY=0 NormalZ=1 AngleXU=0 Radius=3.4
    g40: Circle CenterX=-18.6 CenterY=12.1 CenterZ=0 NormalX=0 NormalY=0 NormalZ=1 AngleXU=0 Radius=3.4
    g41: Circle CenterX=-43.2 CenterY=30.3 CenterZ=0 NormalX=0 NormalY=0 NormalZ=1 AngleXU=0 Radius=3.4
    g42: Circle CenterX=-43.2 CenterY=12.1 CenterZ=0 NormalX=0 NormalY=0 NormalZ=1 AngleXU=0 Radius=3.4
    g43: LineSegment [constr] StartX=-4 StartY=21.2 StartZ=0 EndX=-15.2 EndY=21.2 EndZ=0
    g44: LineSegment [constr] StartX=-15.2 StartY=21.2 StartZ=0 EndX=-36.2 EndY=21.2 EndZ=0
    g45: LineSegment [constr] StartX=-41.5 StartY=16.2 StartZ=0 EndX=-30.9 EndY=16.2 EndZ=0
    g46: LineSegment [constr] StartX=-30.9 StartY=16.2 StartZ=0 EndX=-30.9 EndY=26.2 EndZ=0
    g47: LineSegment [constr] StartX=-30.9 StartY=26.2 StartZ=0 EndX=-41.5 EndY=26.2 EndZ=0
    g48: LineSegment [constr] StartX=-41.5 StartY=26.2 StartZ=0 EndX=-41.5 EndY=16.2 EndZ=0
    g49: GeomPoint [constr] X=-36.2 Y=21.2 Z=0
    g50: Circle CenterX=-36.2 CenterY=21.2 CenterZ=0 NormalX=0 NormalY=0 NormalZ=1 AngleXU=0 Radius=2.8
    g51: LineSegment [constr] StartX=-24.2 StartY=26.7 StartZ=0 EndX=-24.2 EndY=15.7 EndZ=0
    g52: Circle CenterX=-24.2 CenterY=26.7 CenterZ=0 NormalX=0 NormalY=0 NormalZ=1 AngleXU=0 Radius=3
    g53: Circle CenterX=-24.2 CenterY=15.7 CenterZ=0 NormalX=0 NormalY=0 NormalZ=1 AngleXU=0 Radius=3
    g54: GeomPoint X=-18.6 Y=30.3 Z=0
    g55: GeomPoint X=-18.6 Y=12.1 Z=0
    g56: GeomPoint X=-43.2 Y=12.1 Z=0
    g57: GeomPoint X=-43.2 Y=30.3 Z=0
    g58: Circle CenterX=-65 CenterY=21.2 CenterZ=0 NormalX=0 NormalY=0 NormalZ=1 AngleXU=0 Radius=1.5
    g59: Circle CenterX=-42 CenterY=21.2 CenterZ=0 NormalX=0 NormalY=0 NormalZ=1 AngleXU=0 Radius=1.5
    g60: Circle CenterX=-19 CenterY=21.2 CenterZ=0 NormalX=0 NormalY=0 NormalZ=1 AngleXU=0 Radius=1.5
  constraints (149):
    c: Coincident(g0,g-41)
    c: Horizontal(g0)
    c: PointOnObject(g0,g-39)
    c: Coincident(g1,g0)
    c: Vertical(g1)
    c: DistanceY(g1,g1) = 3
    c: Coincident(g2,g-17)
    c: Vertical(g2)
    c: Coincident(g3,g-16)
    c: Vertical(g3)
    c: DistanceY(g2,g2) = 2
    c: DistanceY(g3,g3) = 2
    c: Coincident(g4,g3)
    c: Coincident(g4,g2)
    c: Coincident(g5,g-17)
    c: Coincident(g5,g2)
    c: Coincident(g6,g1)
    c: Horizontal(g6)
    c: Coincident(g6,g5)
    c: Coincident(g7,g-15)
    c: Coincident(g8,g7)
    c: Coincident(g8,g3)
    c: Coincident(g8,g-15)
    c: Horizontal(g9)
    c: DistanceY(g-13,g9) = 2
    c: Coincident(g10,g7)
    c: Parallel(g10,g-14)
    c: Coincident(g9,g10)
    c: Distance(g11) = 2
    c: Coincident(g11,g-11)
    c: Perpendicular(g-11,g11)
    c: Distance(g12) = 2
    c: Coincident(g12,g-12)
    c: Perpendicular(g-11,g12)
    c: Coincident(g13,g11)
    c: Coincident(g13,g12)
    c: Coincident(g14,g-32)
    c: Coincident(g14,g12)
    c: Coincident(g14,g9)
    c: Coincident(g15,g-10)
    c: Coincident(g15,g11)
    c: Parallel(g16,g-22)
    c: Distance(g17) = 4
    c: PointOnObject(g17,g16)
    c: Coincident(g15,g16)
    c: Horizontal(g18)
    c: Coincident(g18,g16)
    c: Coincident(g19,g0)
    c: PointOnObject(g19,g-39)
    c: DistanceY(g19,g-36) = 2
    c: Coincident(g18,g19)
    c: Diameter(g22) = 3.6
    c: Coincident(g22,g-9)
    c: Diameter(g23) = 3.6
    c: Coincident(g23,g-8)
    c: Diameter(g24) = 3.6
    c: Diameter(g25) = 3.6
    c: Diameter(g26) = 3.6
    c: Diameter(g27) = 3.6
    c: Diameter(g28) = 3.6
    c: Coincident(g27,g-4)
    c: Coincident(g28,g-3)
    c: Coincident(g25,g-6)
    c: Coincident(g26,g-5)
    c: Coincident(g24,g-7)
    c: Parallel(g20,g-21)
    c: Equal(g20,g-21)
    c: Parallel(g21,g-19)
    c: Equal(g21,g-19)
    c: Distance(g29) = 0.2
    c: Distance(g30) = 0.2
    c: Parallel(g29,g-20)
    c: Parallel(g31,g-20)
    c: Equal(g31,g-20)
    c: Coincident(g30,g31)
    c: Coincident(g31,g29)
    c: Coincident(g29,g-21)
    c: Parallel(g30,g31)
    c: Coincident(g17,g30)
    c: Coincident(g20,g29)
    c: Coincident(g21,g30)
    c: Perpendicular(g16,g17)
    c: Coincident(g32,g21)
    c: Coincident(g32,g20)
    c: Perpendicular(g10,g7)
    c: Horizontal(g33)
    c: Symmetric(g-24,g-24,g33)
    c: PointOnObject(g33,g-28)
    c: Symmetric(g-24,g-24,g34)
    c: DistanceY(g35,g35) = 25
    c: Symmetric(g35,g35,g33)
    c: Distance(g36) = 41
    c: Coincident(g36,g35)
    c: Horizontal(g36)
    c: Coincident(g37,g35)
    c: Horizontal(g37)
    c: Coincident(g38,g36)
    c: Vertical(g38)
    c: Coincident(g37,g38)
    c: Diameter(g39) = 6.8
    c: Diameter(g40) = 6.8
    c: Tangent(g39,g36)
    c: Tangent(g40,g37)
    c: Tangent(g39,g35)
    c: Tangent(g40,g35)
    c: Diameter(g41) = 6.8
    c: Diameter(g42) = 6.8
    c: Tangent(g41,g36)
    c: Tangent(g42,g37)
    c: DistanceX(g41,g39) = 24.6
    c: DistanceX(g42,g40) = 24.6
    c: Distance(g43) = 11.2
    c: Coincident(g43,g33)
    c: PointOnObject(g43,g33)
    c: PointOnObject(g43,g35)
    c: Distance(g44) = 21
    c: Coincident(g44,g43)
    c: PointOnObject(g44,g33)
    c: Coincident(g45,g46)
    c: Coincident(g46,g47)
    c: Coincident(g47,g48)
    c: Coincident(g48,g45)
    c: Horizontal(g45)
    c: Horizontal(g47)
    c: Vertical(g46)
    c: Vertical(g48)
    c: Symmetric(g47,g45,g49)
    c: Distance(g46,g48) = 10.6
    c: Distance(g45,g47) = 10
    c: Coincident(g49,g44)
    c: Diameter(g50) = 5.6
    c: Coincident(g50,g44)
    c: Distance(g51) = 11
    c: Symmetric(g51,g51,g33)
    c: DistanceX(g51,g43) = 9
    c: Diameter(g52) = 6
    c: Coincident(g52,g51)
    c: Diameter(g53) = 6
    c: Coincident(g53,g51)
    c: Coincident(g40,g55)
    c: Coincident(g39,g54)
    c: Coincident(g41,g57)
    c: Coincident(g42,g56)
    c: Diameter(g58) = 3
    c: Diameter(g59) = 3
    c: Diameter(g60) = 3
    c: Coincident(g58,g-44)
    c: Coincident(g59,g-46)
    c: Coincident(g60,g-45)
FEATURE [PartDesign::Body] Body  label="Struttura pistola"
  AllowCompound = false
  Group = -> [Sketch,Sketch002,Sketch004,DatumPlane,Sketch005,DatumPlane001,CopyCut,Sketch008,Sketch009,Sketch010,Sketch011,Sketch012,Sketch013,Sketch014,Sketch015,Sketch016,Sketch017,Sketch018,Sketch019,Sketch020,Sketch022,Sketch023,Sketch024,Sketch025,Sketch026,Sketch027,Sketch029,Sketch030,Sketch031,Sketch032,Sketch033,Sketch034,Sketch035,Sketch036,Sketch037,Sketch038,Sketch039,Sketch040,Sketch041,Sketch042,+15 more]
  Origin = -> Origin
FEATURE [Sketcher::SketchObject] Sketch078
  ArcFitTolerance = 1e-06
  AttachmentSupport = -> [XZ_Plane005]
  FullyConstrained = true
  MakeInternals = false
  MapMode = 5
  Placement = pos=(0,0,0) rot=(1,0,0;1.5708rad)
  sketch-geometry (5):
    g0: LineSegment [constr] StartX=0 StartY=5.5 StartZ=0 EndX=0 EndY=-5.5 EndZ=0
    g1: ArcOfCircle CenterX=0 CenterY=5.5 CenterZ=0 NormalX=0 NormalY=0 NormalZ=1 AngleXU=0 Radius=2.7 StartAngle=0 EndAngle=3.14159
    g2: ArcOfCircle CenterX=0 CenterY=-5.5 CenterZ=0 NormalX=0 NormalY=0 NormalZ=1 AngleXU=0 Radius=2.7 StartAngle=3.1416 EndAngle=6.28318
    g3: LineSegment StartX=-2.7 StartY=5.5 StartZ=0 EndX=-2.7 EndY=-5.50001 EndZ=0
    g4: LineSegment StartX=2.7 StartY=5.5 StartZ=0 EndX=2.7 EndY=-5.50001 EndZ=0
  constraints (13):
    c: Distance(g0) = 11
    c: Vertical(g0)
    c: Symmetric(g0,g0,g-1)
    c: Radius(g1) = 2.7
    c: Coincident(g1,g0)
    c: Radius(g2) = 2.7
    c: Coincident(g2,g0)
    c: Vertical(g3)
    c: Vertical(g4)
    c: Coincident(g2,g4)
    c: Coincident(g2,g3)
    c: Tangent(g3,g1) = -1.5708
    c: Tangent(g4,g1) = 1.5708
FEATURE [PartDesign::Pad] Pad002
  Direction = (0,-1,2e-16)
  Length = 0.8
  Length2 = 10
  Placement = pos=(0,0,0) rot=(1,0,0;1.5708rad)
  Profile = -> Sketch078
  ReferenceAxis = -> Sketch078 [N_Axis]
  Refine = true
  Suppressed = false
  Type = 0
FEATURE [Sketcher::SketchObject] Sketch079
  ArcFitTolerance = 1e-06
  AttachmentSupport = -> [XZ_Plane005]
  ExternalGeometry = -> [Sketch078]
  FullyConstrained = true
  MakeInternals = false
  MapMode = 5
  Placement = pos=(0,0,0) rot=(1,0,0;1.5708rad)
  sketch-geometry (2):
    g0: Circle CenterX=-1e-16 CenterY=5.5 CenterZ=0 NormalX=0 NormalY=0 NormalZ=1 AngleXU=0 Radius=2.7
    g1: Circle CenterX=0 CenterY=-5.5 CenterZ=0 NormalX=0 NormalY=0 NormalZ=1 AngleXU=0 Radius=2.7
  constraints (4):
    c: Coincident(g0,g-3)
    c: PointOnObject(g-3,g0)
    c: Coincident(g1,g-4)
    c: Equal(g1,g-4)
FEATURE [PartDesign::Pad] Pad003
  BaseFeature = -> Pad002
  Direction = (0,-1,2e-16)
  Length = 5
  Length2 = 10
  Placement = pos=(0,0,0) rot=(1,0,0;1.5708rad)
  Profile = -> Sketch079
  ReferenceAxis = -> Sketch079 [N_Axis]
  Refine = true
  Suppressed = false
  Type = 0
FEATURE [PartDesign::Fillet] Fillet001
  Base = -> Pad003 [Edge16,Edge14]
  BaseFeature = -> Pad003
  Placement = pos=(0,0,0) rot=(1,0,0;1.5708rad)
  Radius = 0.4
  Refine = true
  SupportTransform = false
  Suppressed = false
  UseAllEdges = false
FEATURE [PartDesign::Body] Body005  label="pulsanti lato destro"
  AllowCompound = false
  Group = -> [Sketch078,Pad002,Sketch079,Pad003,Fillet001]
  Origin = -> Origin005
  Tip = -> Fillet001
FEATURE [PartDesign::SubShapeBinder] Binder
  BindCopyOnChange = 0
  BindMode = 0
  ClaimChildren = false
  Context = -> Body006 [Binder.]
  Fuse = false
  MakeFace = true
  OffsetFill = false
  OffsetIntersection = false
  OffsetJoinType = 0
  OffsetOpenResult = false
  PartialLoad = false
  Refine = true
  Relative = true
  Support = -> [Body[Sketch074.]]
  _Version = 2
FEATURE [PartDesign::SubShapeBinder] Binder001
  BindCopyOnChange = 0
  BindMode = 0
  ClaimChildren = false
  Context = -> Body007 [Binder001.]
  Fuse = false
  MakeFace = true
  OffsetFill = false
  OffsetIntersection = false
  OffsetJoinType = 0
  OffsetOpenResult = false
  PartialLoad = false
  Refine = true
  Relative = true
  Support = -> [Body[Sketch075.]]
  _Version = 2
FEATURE [Mesh::Feature] logo_per_PCB_definitivo_positivo
  Placement = pos=(-191,17,-66) rot=(0,1,1;0rad)
FEATURE [Sketcher::SketchObject] Sketch114  label="Sketch114 - base lato DX"
  ArcFitTolerance = 1e-06
  AttachmentSupport = -> [Binder001]
  ExternalGeometry = -> [Binder001]
  FullyConstrained = true
  MakeInternals = false
  MapMode = 5
  Placement = pos=(0,1e-15,0) rot=(0,0.707107,0.707107;3.14159rad)
  sketch-geometry (30):
    g0: Circle CenterX=5.6 CenterY=34.8 CenterZ=0 NormalX=0 NormalY=0 NormalZ=1 AngleXU=0 Radius=1.8
    g1: Circle CenterX=5.6 CenterY=7.6 CenterZ=0 NormalX=0 NormalY=0 NormalZ=1 AngleXU=0 Radius=1.8
    g2: Circle CenterX=24.2 CenterY=26.7 CenterZ=0 NormalX=0 NormalY=0 NormalZ=1 AngleXU=0 Radius=3
    g3: Circle CenterX=24.2 CenterY=15.7 CenterZ=0 NormalX=0 NormalY=0 NormalZ=1 AngleXU=0 Radius=3
    g4: Circle CenterX=36.2 CenterY=21.2 CenterZ=0 NormalX=0 NormalY=0 NormalZ=1 AngleXU=0 Radius=2.8
    g5: Circle CenterX=78.51 CenterY=34.8 CenterZ=0 NormalX=0 NormalY=0 NormalZ=1 AngleXU=0 Radius=1.8
    g6: Circle CenterX=78.51 CenterY=7.6 CenterZ=0 NormalX=0 NormalY=0 NormalZ=1 AngleXU=0 Radius=1.8
    g7: Circle CenterX=184.08 CenterY=34.8 CenterZ=0 NormalX=0 NormalY=0 NormalZ=1 AngleXU=0 Radius=1.8
    g8: Circle CenterX=213.443 CenterY=-76.8316 CenterZ=0 NormalX=0 NormalY=0 NormalZ=1 AngleXU=0 Radius=1.8
    g9: Circle CenterX=179.305 CenterY=-76.8316 CenterZ=0 NormalX=0 NormalY=0 NormalZ=1 AngleXU=0 Radius=1.8
    g10: ArcOfCircle [constr] CenterX=132.428 CenterY=4 CenterZ=0 NormalX=0 NormalY=0 NormalZ=1 AngleXU=0 Radius=16 StartAngle=0.314159 EndAngle=1.5708
    g11: ArcOfCircle CenterX=107.6 CenterY=4 CenterZ=0 NormalX=0 NormalY=0 NormalZ=1 AngleXU=0 Radius=16 StartAngle=1.5708 EndAngle=3.00366
    g12: ArcOfCircle CenterX=207.583 CenterY=4 CenterZ=0 NormalX=0 NormalY=0 NormalZ=1 AngleXU=0 Radius=17 StartAngle=1.85815 EndAngle=3.57792
    g13: ArcOfCircle CenterX=184.801 CenterY=-67.3089 CenterZ=0 NormalX=0 NormalY=0 NormalZ=1 AngleXU=0 Radius=33.7833 StartAngle=5.88425 EndAngle=6.71952
    g14: LineSegment StartX=0 StartY=39.2 StartZ=0 EndX=0 EndY=3.2 EndZ=0
    g15: LineSegment StartX=0 StartY=3.2 StartZ=0 EndX=82.8 EndY=3.2 EndZ=0
    g16: LineSegment StartX=82.8 StartY=3.2 StartZ=0 EndX=82.8 EndY=6.2 EndZ=0
    g17: LineSegment StartX=82.8 StartY=6.2 StartZ=0 EndX=91.752 EndY=6.2 EndZ=0
    g18: LineSegment StartX=107.6 StartY=20 StartZ=0 EndX=132.428 EndY=20 EndZ=0
    g19: LineSegment StartX=147.645 StartY=8.94427 StartZ=0 EndX=176.685 EndY=-80.4316 EndZ=0
    g20: LineSegment StartX=176.685 StartY=-80.4316 StartZ=0 EndX=215.932 EndY=-80.4316 EndZ=0
    g21: LineSegment StartX=215.42 StartY=-53.0314 StartZ=0 EndX=192.176 EndY=-3.18451 EndZ=0
    g22: LineSegment StartX=202.765 StartY=20.303 StartZ=0 EndX=195.887 EndY=39.2 EndZ=0
    g23: LineSegment StartX=195.887 StartY=39.2 StartZ=0 EndX=0 EndY=39.2 EndZ=0
    g24: LineSegment StartX=196.467 StartY=26.4942 StartZ=0 EndX=194.073 EndY=33.0721 EndZ=0
    g25: LineSegment StartX=194.073 StartY=33.0721 StartZ=0 EndX=189.939 EndY=31.5672 EndZ=0
    g26: LineSegment StartX=189.939 StartY=31.5672 StartZ=0 EndX=192.333 EndY=24.9893 EndZ=0
    g27: LineSegment StartX=192.333 StartY=24.9893 StartZ=0 EndX=196.467 EndY=26.4942 EndZ=0
    g28: LineSegment StartX=132.428 StartY=20 StartZ=0 EndX=144.053 EndY=20 EndZ=0
    g29: LineSegment StartX=144.053 StartY=20 StartZ=0 EndX=147.645 EndY=8.94427 EndZ=0
  constraints (65):
    c: Equal(g0,g-25)
    c: Equal(g2,g-29)
    c: Equal(g3,g-30)
    c: Equal(g4,g-28)
    c: Equal(g1,g-26)
    c: Coincident(g0,g-25)
    c: Coincident(g1,g-26)
    c: Coincident(g2,g-29)
    c: Coincident(g3,g-30)
    c: Coincident(g4,g-28)
    c: Equal(g5,g-23)
    c: Equal(g6,g-24)
    c: Coincident(g5,g-23)
    c: Coincident(g6,g-24)
    c: Equal(g7,g-20)
    c: Coincident(g7,g-20)
    c: Equal(g9,g-22)
    c: Coincident(g9,g-22)
    c: Equal(g8,g-21)
    c: Coincident(g8,g-21)
    c: Equal(g13,g-12)
    c: Equal(g12,g-14)
    c: Equal(g10,g-9)
    c: Equal(g11,g-7)
    c: Coincident(g14,g-27)
    c: Coincident(g14,g-27)
    c: Coincident(g15,g14)
    c: Coincident(g15,g-5)
    c: Coincident(g16,g15)
    c: Coincident(g16,g-6)
    c: Coincident(g17,g16)
    c: Coincident(g17,g-7)
    c: Coincident(g11,g17)
    c: Coincident(g11,g-8)
    c: Coincident(g18,g11)
    c: Coincident(g18,g-9)
    c: Coincident(g10,g18)
    c: Coincident(g10,g-10)
    c: Coincident(g19,g10)
    c: Coincident(g19,g-11)
    c: Coincident(g20,g19)
    c: Coincident(g20,g-12)
    c: Coincident(g13,g20)
    c: Coincident(g13,g-13)
    c: Coincident(g21,g13)
    c: Coincident(g21,g-14)
    c: Coincident(g12,g21)
    c: Coincident(g12,g-15)
    c: Coincident(g22,g12)
    c: Coincident(g22,g-15)
    c: Coincident(g23,g22)
    c: Coincident(g23,g14)
    c: Coincident(g24,g-18)
    c: Coincident(g24,g-16)
    c: Coincident(g25,g24)
    c: Coincident(g25,g-19)
    c: Coincident(g26,g25)
    c: Coincident(g26,g-19)
    c: Coincident(g27,g26)
    c: Coincident(g27,g24)
    c: Coincident(g29,g10)
    c: Coincident(g28,g10)
    c: Coincident(g29,g28)
    c: Parallel(g28,g18)
    c: Parallel(g29,g19)
FEATURE [PartDesign::Pad] Pad011
  Direction = (0,1,-2e-16)
  Length = 2
  Length2 = 10
  Profile = -> Sketch114
  ReferenceAxis = -> Sketch114 [N_Axis]
  Refine = true
  Reversed = true
  Suppressed = false
  Type = 0
FEATURE [Sketcher::SketchObject] Sketch115
  ArcFitTolerance = 1e-06
  AttachmentSupport = -> [Pad011]
  ExternalGeometry = -> [Binder001]
  FullyConstrained = true
  MakeInternals = false
  MapMode = 5
  Placement = pos=(0,1.7e-15,0) rot=(0,0.707107,0.707107;3.14159rad)
  sketch-geometry (4):
    g0: ArcOfCircle CenterX=24.2 CenterY=26.7 CenterZ=0 NormalX=0 NormalY=0 NormalZ=1 AngleXU=0 Radius=3 StartAngle=4.48384e-08 EndAngle=3.14159
    g1: ArcOfCircle CenterX=24.2 CenterY=15.7 CenterZ=0 NormalX=0 NormalY=0 NormalZ=1 AngleXU=0 Radius=3 StartAngle=3.14159 EndAngle=6.28318
    g2: LineSegment StartX=21.2 StartY=26.7 StartZ=0 EndX=21.2 EndY=15.7 EndZ=0
    g3: LineSegment StartX=27.2 StartY=26.7 StartZ=0 EndX=27.2 EndY=15.7 EndZ=0
  constraints (12):
    c: Equal(g1,g-4)
    c: Equal(g0,g-3)
    c: Coincident(g0,g-3)
    c: Coincident(g1,g-4)
    c: Vertical(g2)
    c: Vertical(g3)
    c: Tangent(g3,g-3)
    c: Tangent(g2,g-3)
    c: Coincident(g0,g2)
    c: Coincident(g0,g3)
    c: Coincident(g1,g2)
    c: Coincident(g3,g1)
FEATURE [Sketcher::SketchObject] Sketch117  label="Sketch117 - fori per inserto M3 x 3 x 4.5"
  ArcFitTolerance = 1e-06
  AttachmentSupport = -> [Pad011]
  ExternalGeometry = -> [Binder001]
  FullyConstrained = true
  MakeInternals = false
  MapMode = 5
  Placement = pos=(0,1.7e-15,0) rot=(0,0.707107,0.707107;3.14159rad)
  sketch-geometry (4):
    g0: Circle CenterX=43.2 CenterY=30.3 CenterZ=0 NormalX=0 NormalY=0 NormalZ=1 AngleXU=0 Radius=2.25
    g1: Circle CenterX=43.2 CenterY=12.1 CenterZ=0 NormalX=0 NormalY=0 NormalZ=1 AngleXU=0 Radius=2.25
    g2: Circle CenterX=18.6 CenterY=30.3 CenterZ=0 NormalX=0 NormalY=0 NormalZ=1 AngleXU=0 Radius=2.25
    g3: Circle CenterX=18.6 CenterY=12.1 CenterZ=0 NormalX=0 NormalY=0 NormalZ=1 AngleXU=0 Radius=2.25
  constraints (8):
    c: Diameter(g0) = 4.5
    c: Diameter(g1) = 4.5
    c: Diameter(g2) = 4.5
    c: Diameter(g3) = 4.5
    c: Coincident(g2,g-3)
    c: Coincident(g3,g-6)
    c: Coincident(g0,g-4)
    c: Coincident(g1,g-5)
FEATURE [Sketcher::SketchObject] Sketch118
  ArcFitTolerance = 1e-06
  AttachmentSupport = -> [Pad011]
  ExternalGeometry = -> [Binder001]
  FullyConstrained = true
  MakeInternals = false
  MapMode = 5
  Placement = pos=(0,-2,0) rot=(1,0,0;1.5708rad)
  sketch-geometry (12):
    g0: Circle CenterX=-78.51 CenterY=34.8 CenterZ=0 NormalX=0 NormalY=0 NormalZ=1 AngleXU=0 Radius=1.8
    g1: Circle CenterX=-78.51 CenterY=7.6 CenterZ=0 NormalX=0 NormalY=0 NormalZ=1 AngleXU=0 Radius=1.8
    g2: Circle CenterX=-5.6 CenterY=34.8 CenterZ=0 NormalX=0 NormalY=0 NormalZ=1 AngleXU=0 Radius=1.8
    g3: Circle CenterX=-5.6 CenterY=7.6 CenterZ=0 NormalX=0 NormalY=0 NormalZ=1 AngleXU=0 Radius=1.8
    g4: LineSegment StartX=0 StartY=39.2 StartZ=0 EndX=0 EndY=3.2 EndZ=0
    g5: LineSegment StartX=0 StartY=3.2 StartZ=0 EndX=-82.8 EndY=3.2 EndZ=0
    g6: LineSegment StartX=-82.8 StartY=3.2 StartZ=0 EndX=-82.8 EndY=39.2 EndZ=0
    g7: LineSegment StartX=-82.8 StartY=39.2 StartZ=0 EndX=0 EndY=39.2 EndZ=0
    g8: ArcOfCircle CenterX=-65 CenterY=21.2 CenterZ=0 NormalX=0 NormalY=0 NormalZ=1 AngleXU=0 Radius=10 StartAngle=1.5708 EndAngle=4.71239
    g9: ArcOfCircle CenterX=-19 CenterY=21.2 CenterZ=0 NormalX=0 NormalY=0 NormalZ=1 AngleXU=0 Radius=10 StartAngle=4.71239 EndAngle=7.85398
    g10: LineSegment StartX=-65 StartY=31.2 StartZ=0 EndX=-19 EndY=31.2 EndZ=0
    g11: LineSegment StartX=-65 StartY=11.2 StartZ=0 EndX=-19 EndY=11.2 EndZ=0
  constraints (25):
    c: Equal(g2,g-5)
    c: Equal(g3,g-7)
    c: Equal(g1,g-6)
    c: Equal(g0,g-4)
    c: Coincident(g0,g-4)
    c: Coincident(g1,g-6)
    c: Coincident(g3,g-7)
    c: Coincident(g2,g-5)
    c: Coincident(g4,g-8)
    c: Coincident(g4,g-9)
    c: Coincident(g5,g4)
    c: Coincident(g5,g-10)
    c: Coincident(g6,g5)
    c: PointOnObject(g6,g-3)
    c: Vertical(g6)
    c: Coincident(g7,g6)
    c: Coincident(g7,g4)
    c: Tangent(g8,g10) = 1.5708
    c: Tangent(g8,g11) = -1.5708
    c: Tangent(g9,g10) = 1.5708
    c: Tangent(g9,g11) = -1.5708
    c: Equal(g8,g9)
    c: Radius(g8) = 10
    c: Coincident(g8,g-11)
    c: Coincident(g9,g-12)
FEATURE [Sketcher::SketchObject] Sketch120
  ArcFitTolerance = 1e-06
  AttachmentSupport = -> [Pad011]
  ExternalGeometry = -> [Binder001]
  FullyConstrained = true
  MakeInternals = false
  MapMode = 5
  Placement = pos=(0,-2,0) rot=(1,0,0;1.5708rad)
  sketch-geometry (4):
    g0: LineSegment StartX=-137.815 StartY=39.2 StartZ=0 EndX=-142.655 EndY=24.303 EndZ=0
    g1: LineSegment StartX=-137.815 StartY=39.2 StartZ=0 EndX=-110.815 EndY=39.2 EndZ=0
    g2: LineSegment StartX=-142.655 StartY=24.303 StartZ=0 EndX=-110.815 EndY=24.303 EndZ=0
    g3: ArcOfCircle CenterX=-92.2534 CenterY=31.7515 CenterZ=0 NormalX=0 NormalY=0 NormalZ=1 AngleXU=0 Radius=20 StartAngle=2.75997 EndAngle=3.52321
  constraints (12):
    c: PointOnObject(g0,g-3)
    c: Coincident(g1,g0)
    c: PointOnObject(g1,g-3)
    c: Coincident(g2,g0)
    c: Horizontal(g2)
    c: Tangent(g0,g-4)
    c: Vertical(g2,g1)
    c: DistanceX(g1,g1) = 27
    c: DistanceY(g-6,g0) = 4
    c: Radius(g3) = 20
    c: Coincident(g3,g1)
    c: Coincident(g3,g2)
FEATURE [Sketcher::SketchObject] Sketch121
  ArcFitTolerance = 1e-06
  AttachmentSupport = -> [Pad011]
  ExternalGeometry = -> [Binder001]
  FullyConstrained = true
  MakeInternals = false
  MapMode = 5
  Placement = pos=(0,-2,0) rot=(1,0,0;1.5708rad)
  sketch-geometry (15):
    g0: LineSegment StartX=-137.815 StartY=39.2 StartZ=0 EndX=-143.955 EndY=20.303 EndZ=0
    g1: LineSegment StartX=-143.955 StartY=20.303 StartZ=0 EndX=-190.141 EndY=20.303 EndZ=0
    g2: LineSegment StartX=-190.141 StartY=20.303 StartZ=0 EndX=-186.139 EndY=31.3 EndZ=0
    g3: LineSegment StartX=-178.754 StartY=39.2 StartZ=0 EndX=-180.791 EndY=33.6029 EndZ=0
    g4: ArcOfCircle CenterX=-184.08 CenterY=34.8 CenterZ=0 NormalX=0 NormalY=0 NormalZ=1 AngleXU=0 Radius=3.5 StartAngle=4.71239 EndAngle=5.93412
    g5: LineSegment StartX=-184.08 StartY=31.3 StartZ=0 EndX=-186.139 EndY=31.3 EndZ=0
    g6: LineSegment StartX=-137.815 StartY=39.2 StartZ=0 EndX=-156.815 EndY=39.2 EndZ=0
    g7: LineSegment StartX=-168.815 StartY=39.2 StartZ=0 EndX=-178.754 EndY=39.2 EndZ=0
    g8: LineSegment StartX=-157.815 StartY=39.2 StartZ=0 EndX=-167.815 EndY=39.2 EndZ=0
    g9: LineSegment StartX=-168.815 StartY=31.2 StartZ=0 EndX=-156.815 EndY=31.2 EndZ=0
    g10: LineSegment StartX=-167.436 StartY=36.2 StartZ=0 EndX=-157.436 EndY=36.2 EndZ=0
    g11: ArcOfCircle CenterX=-176.411 CenterY=35.2 CenterZ=0 NormalX=0 NormalY=0 NormalZ=1 AngleXU=0 Radius=20 StartAngle=6.08183 EndAngle=6.48454
    g12: ArcOfCircle CenterX=-188.411 CenterY=35.2 CenterZ=0 NormalX=0 NormalY=0 NormalZ=1 AngleXU=0 Radius=20 StartAngle=6.08183 EndAngle=6.48454
    g13: ArcOfCircle CenterX=-177.411 CenterY=35.2 CenterZ=0 NormalX=0 NormalY=0 NormalZ=1 AngleXU=0 Radius=20 StartAngle=0.0500209 EndAngle=0.201358
    g14: ArcOfCircle CenterX=-187.411 CenterY=35.2 CenterZ=0 NormalX=0 NormalY=0 NormalZ=1 AngleXU=0 Radius=20 StartAngle=0.0500209 EndAngle=0.201358
  constraints (46):
    c: PointOnObject(g0,g-3)
    c: Tangent(g0,g-5)
    c: Coincident(g1,g0)
    c: Horizontal(g1)
    c: Coincident(g2,g1)
    c: PointOnObject(g3,g-3)
    c: Parallel(g3,g-6)
    c: Parallel(g2,g-6)
    c: Radius(g4) = 3.5
    c: Coincident(g4,g-7)
    c: Tangent(g3,g4) = 1.5708
    c: Horizontal(g5)
    c: Tangent(g5,g4) = 1.5708
    c: DistanceX(g-8,g5) = 3.8
    c: Coincident(g2,g5)
    c: Coincident(g6,g0)
    c: PointOnObject(g6,g-3)
    c: DistanceX(g6,g6) = 19
    c: PointOnObject(g7,g-3)
    c: DistanceX(g7,g6) = 12
    c: Coincident(g7,g3)
    c: PointOnObject(g8,g-3)
    c: PointOnObject(g8,g-3)
    c: DistanceX(g8,g8) = 10
    c: DistanceX(g8,g6) = 1
    c: Horizontal(g9)
    c: Vertical(g7,g9)
    c: Vertical(g6,g9)
    c: DistanceY(g9,g7) = 8
    c: Horizontal(g10)
    c: Equal(g8,g10)
    c: DistanceY(g10,g8) = 3
    c: Radius(g11) = 20
    c: Coincident(g11,g6)
    c: Coincident(g11,g9)
    c: Radius(g12) = 20
    c: Coincident(g12,g7)
    c: Coincident(g12,g9)
    c: Equal(g13,g11)
    c: Coincident(g13,g8)
    c: Coincident(g13,g10)
    c: Horizontal(g13,g11)
    c: Equal(g14,g12)
    c: Coincident(g14,g8)
    c: Coincident(g14,g10)
    c: Horizontal(g1,g-6)
FEATURE [Sketcher::SketchObject] Sketch122
  ArcFitTolerance = 1e-06
  AttachmentSupport = -> [Pad011]
  ExternalGeometry = -> [Binder001]
  FullyConstrained = true
  MakeInternals = false
  MapMode = 5
  Placement = pos=(0,-2,0) rot=(1,0,0;1.5708rad)
  sketch-geometry (8):
    g0: LineSegment StartX=-202.765 StartY=20.303 StartZ=0 EndX=-143.955 EndY=20.303 EndZ=0
    g1: ArcOfCircle CenterX=-184.801 CenterY=-67.3089 CenterZ=0 NormalX=0 NormalY=0 NormalZ=1 AngleXU=0 Radius=33.7833 StartAngle=2.70526 EndAngle=3.54053
    g2: LineSegment StartX=-176.685 StartY=-80.4316 StartZ=0 EndX=-215.932 EndY=-80.4316 EndZ=0
    g3: LineSegment StartX=-215.42 StartY=-53.0315 StartZ=0 EndX=-192.176 EndY=-3.18454 EndZ=0
    g4: ArcOfCircle CenterX=-207.583 CenterY=4 CenterZ=0 NormalX=0 NormalY=0 NormalZ=1 AngleXU=0 Radius=17 StartAngle=5.84685 EndAngle=7.56663
    g5: Circle CenterX=-213.443 CenterY=-76.8316 CenterZ=0 NormalX=0 NormalY=0 NormalZ=1 AngleXU=0 Radius=3
    g6: Circle CenterX=-179.305 CenterY=-76.8316 CenterZ=0 NormalX=0 NormalY=0 NormalZ=1 AngleXU=0 Radius=3
    g7: LineSegment StartX=-143.955 StartY=20.303 StartZ=0 EndX=-176.685 EndY=-80.4316 EndZ=0
  constraints (18):
    c: Coincident(g0,g-6)
    c: Coincident(g1,g-7)
    c: Coincident(g1,g-8)
    c: Coincident(g2,g1)
    c: Tangent(g3,g-5)
    c: Coincident(g4,g-6)
    c: Coincident(g4,g0)
    c: Coincident(g3,g4)
    c: Coincident(g1,g3)
    c: Diameter(g5) = 6
    c: Diameter(g6) = 6
    c: Coincident(g5,g-9)
    c: Coincident(g6,g-10)
    c: Horizontal(g0)
    c: Horizontal(g2)
    c: Coincident(g7,g0)
    c: Coincident(g7,g2)
    c: Tangent(g7,g-4)
FEATURE [Sketcher::SketchObject] Sketch123
  ArcFitTolerance = 1e-06
  AttachmentSupport = -> [Pad011]
  ExternalGeometry = -> [Binder001]
  FullyConstrained = true
  MakeInternals = false
  MapMode = 5
  Placement = pos=(0,-2,0) rot=(1,0,0;1.5708rad)
  sketch-geometry (4):
    g0: LineSegment StartX=-108 StartY=36.8 StartZ=0 EndX=-90 EndY=36.8 EndZ=0
    g1: LineSegment StartX=-108 StartY=36.8 StartZ=0 EndX=-108 EndY=26.8 EndZ=0
    g2: LineSegment StartX=-108 StartY=26.8 StartZ=0 EndX=-90 EndY=26.8 EndZ=0
    g3: ArcOfCircle CenterX=-94 CenterY=31.8 CenterZ=0 NormalX=0 NormalY=0 NormalZ=1 AngleXU=0 Radius=6.40312 StartAngle=5.38713 EndAngle=7.17924
  constraints (13):
    c: Horizontal(g0)
    c: Coincident(g1,g0)
    c: Vertical(g1)
    c: Coincident(g2,g1)
    c: Horizontal(g2)
    c: DistanceX(g0,g0) = 18
    c: DistanceY(g1,g1) = 10
    c: Equal(g0,g2)
    c: DistanceX(g0,g-3) = 90
    c: DistanceY(g0,g-3) = 2.4
    c: Coincident(g3,g0)
    c: Coincident(g3,g2)
    c: DistanceX(g3,g0) = 4
FEATURE [PartDesign::Chamfer] Chamfer014
  Angle = 45
  Base = -> Pad011 [Edge80,Edge4,Edge7]
  BaseFeature = -> Pad011
  ChamferType = 0
  FlipDirection = false
  Refine = true
  Size = 1.9
  Size2 = 1
  SupportTransform = false
  Suppressed = false
  UseAllEdges = false
FEATURE [PartDesign::Pocket] Pocket006
  BaseFeature = -> Chamfer014
  Direction = (0,-1,2e-16)
  Length = 1.2
  Length2 = 5
  Profile = -> Sketch115
  ReferenceAxis = -> Sketch115 [N_Axis]
  Refine = true
  Suppressed = false
  Type = 0
FEATURE [Sketcher::SketchObject] Sketch116  label="Sketch116 - pieno per inserto M3 x 3 x 4,5"
  ArcFitTolerance = 1e-06
  AttachmentSupport = -> [Pocket006]
  ExternalGeometry = -> [Binder001]
  FullyConstrained = true
  MakeInternals = false
  MapMode = 5
  Placement = pos=(0,1.7e-15,0) rot=(0,0.707107,0.707107;3.14159rad)
  sketch-geometry (4):
    g0: Circle CenterX=43.2 CenterY=30.3 CenterZ=0 NormalX=0 NormalY=0 NormalZ=1 AngleXU=0 Radius=3.4
    g1: Circle CenterX=43.2 CenterY=12.1 CenterZ=0 NormalX=0 NormalY=0 NormalZ=1 AngleXU=0 Radius=3.4
    g2: Circle CenterX=18.6 CenterY=30.3 CenterZ=0 NormalX=0 NormalY=0 NormalZ=1 AngleXU=0 Radius=3.4
    g3: Circle CenterX=18.6 CenterY=12.1 CenterZ=0 NormalX=0 NormalY=0 NormalZ=1 AngleXU=0 Radius=3.4
  constraints (8):
    c: Diameter(g0) = 6.8
    c: Diameter(g1) = 6.8
    c: Diameter(g2) = 6.8
    c: Diameter(g3) = 6.8
    c: Coincident(g2,g-3)
    c: Coincident(g0,g-4)
    c: Coincident(g3,g-6)
    c: Coincident(g1,g-5)
FEATURE [PartDesign::Pad] Pad012
  BaseFeature = -> Pocket006
  Direction = (0,1,-2e-16)
  Length = 2.4
  Length2 = 10
  Profile = -> Sketch116
  ReferenceAxis = -> Sketch116 [N_Axis]
  Refine = true
  Suppressed = false
  Type = 0
FEATURE [PartDesign::Pocket] Pocket007
  BaseFeature = -> Pad012
  Direction = (0,-1,2e-16)
  Length = 0.6
  Length2 = 2.4
  Profile = -> Sketch117
  ReferenceAxis = -> Sketch117 [N_Axis]
  Refine = true
  Suppressed = false
  Type = 4
FEATURE [PartDesign::Pad] Pad013
  BaseFeature = -> Pocket007
  Direction = (0,-1,2e-16)
  Length = 1.6
  Length2 = 10
  Profile = -> Sketch118
  ReferenceAxis = -> Sketch118 [N_Axis]
  Refine = true
  Suppressed = false
  Type = 0
FEATURE [Sketcher::SketchObject] Sketch119
  ArcFitTolerance = 1e-06
  AttachmentSupport = -> [Pad013]
  ExternalGeometry = -> [Binder001]
  FullyConstrained = true
  MakeInternals = false
  MapMode = 5
  Placement = pos=(0,-3.6,0) rot=(1,0,0;1.5708rad)
  sketch-geometry (21):
    g0: LineSegment [constr] StartX=-82.8 StartY=3.2 StartZ=0 EndX=-82.8 EndY=39.2 EndZ=0
    g1: ArcOfCircle CenterX=-78.51 CenterY=34.8 CenterZ=0 NormalX=0 NormalY=0 NormalZ=1 AngleXU=0 Radius=3.5 StartAngle=4.71239 EndAngle=6.28319
    g2: ArcOfCircle CenterX=-78.51 CenterY=7.6 CenterZ=0 NormalX=0 NormalY=0 NormalZ=1 AngleXU=0 Radius=3.5 StartAngle=0 EndAngle=1.5708
    g3: ArcOfCircle CenterX=-5.6 CenterY=34.8 CenterZ=0 NormalX=0 NormalY=0 NormalZ=1 AngleXU=0 Radius=3.5 StartAngle=3.14159 EndAngle=4.71239
    g4: ArcOfCircle CenterX=-5.6 CenterY=7.6 CenterZ=0 NormalX=0 NormalY=0 NormalZ=1 AngleXU=0 Radius=3.5 StartAngle=1.5708 EndAngle=3.14159
    g5: LineSegment StartX=0 StartY=39.2 StartZ=0 EndX=0 EndY=31.3 EndZ=0
    g6: LineSegment StartX=0 StartY=39.2 StartZ=0 EndX=-9.1 EndY=39.2 EndZ=0
    g7: LineSegment StartX=0 StartY=3.2 StartZ=0 EndX=0 EndY=11.1 EndZ=0
    g8: LineSegment StartX=0 StartY=3.2 StartZ=0 EndX=-9.1 EndY=3.2 EndZ=0
    g9: LineSegment StartX=-82.8 StartY=3.2 StartZ=0 EndX=-75.01 EndY=3.2 EndZ=0
    g10: LineSegment StartX=-82.8 StartY=3.2 StartZ=0 EndX=-82.8 EndY=11.1 EndZ=0
    g11: LineSegment StartX=-82.8 StartY=39.2 StartZ=0 EndX=-82.8 EndY=31.3 EndZ=0
    g12: LineSegment StartX=-82.8 StartY=39.2 StartZ=0 EndX=-75.01 EndY=39.2 EndZ=0
    g13: LineSegment StartX=-82.8 StartY=31.3 StartZ=0 EndX=-78.51 EndY=31.3 EndZ=0
    g14: LineSegment StartX=-75.01 StartY=39.2 StartZ=0 EndX=-75.01 EndY=34.8 EndZ=0
    g15: LineSegment StartX=-82.8 StartY=11.1 StartZ=0 EndX=-78.51 EndY=11.1 EndZ=0
    g16: LineSegment StartX=-75.01 StartY=3.2 StartZ=0 EndX=-75.01 EndY=7.6 EndZ=0
    g17: LineSegment StartX=-9.1 StartY=39.2 StartZ=0 EndX=-9.1 EndY=34.8 EndZ=0
    g18: LineSegment StartX=0 StartY=31.3 StartZ=0 EndX=-5.6 EndY=31.3 EndZ=0
    g19: LineSegment StartX=0 StartY=11.1 StartZ=0 EndX=-5.6 EndY=11.1 EndZ=0
    g20: LineSegment StartX=-9.1 StartY=3.2 StartZ=0 EndX=-9.1 EndY=7.6 EndZ=0
  constraints (51):
    c: Coincident(g0,g-10)
    c: PointOnObject(g0,g-8)
    c: Vertical(g0)
    c: Coincident(g1,g-3)
    c: Coincident(g2,g-4)
    c: Coincident(g3,g-5)
    c: Coincident(g4,g-6)
    c: Radius(g4) = 3.5
    c: Radius(g3) = 3.5
    c: Radius(g1) = 3.5
    c: Radius(g2) = 3.5
    c: Coincident(g5,g-9)
    c: PointOnObject(g5,g-9)
    c: Coincident(g6,g5)
    c: PointOnObject(g6,g-8)
    c: Coincident(g7,g-9)
    c: PointOnObject(g7,g-9)
    c: Coincident(g8,g7)
    c: PointOnObject(g8,g-7)
    c: Coincident(g9,g0)
    c: PointOnObject(g9,g-7)
    c: Coincident(g10,g0)
    c: PointOnObject(g10,g0)
    c: Coincident(g11,g0)
    c: PointOnObject(g11,g0)
    c: Coincident(g12,g0)
    c: PointOnObject(g12,g-8)
    c: Coincident(g13,g11)
    c: Horizontal(g13)
    c: Coincident(g14,g12)
    c: Vertical(g14)
    c: Coincident(g15,g10)
    c: Horizontal(g15)
    c: Coincident(g16,g9)
    c: Vertical(g16)
    c: Coincident(g17,g6)
    c: Vertical(g17)
    c: Coincident(g18,g5)
    c: Horizontal(g18)
    c: Coincident(g19,g7)
    c: Horizontal(g19)
    c: Coincident(g20,g8)
    c: Vertical(g20)
    c: Tangent(g20,g4) = 1.5708
    c: Tangent(g4,g19) = -1.5708
    c: Tangent(g18,g3) = 1.5708
    c: Tangent(g3,g17) = -1.5708
    c: Tangent(g13,g1) = -1.5708
    c: Tangent(g1,g14) = 1.5708
    c: Tangent(g16,g2) = -1.5708
    c: Tangent(g2,g15) = 1.5708
FEATURE [PartDesign::Pocket] Pocket008
  BaseFeature = -> Pad013
  Direction = (0,1,-2e-16)
  Length = 1.6
  Length2 = 5
  Profile = -> Sketch119
  ReferenceAxis = -> Sketch119 [N_Axis]
  Refine = true
  Suppressed = false
  Type = 0
FEATURE [PartDesign::Pad] Pad017
  BaseFeature = -> Pocket008
  Direction = (0,-1,2e-16)
  Length = 1.6
  Length2 = 10
  Profile = -> Sketch123
  ReferenceAxis = -> Sketch123 [N_Axis]
  Refine = true
  Suppressed = false
  Type = 0
FEATURE [Sketcher::SketchObject] Sketch125
  ArcFitTolerance = 1e-06
  AttachmentSupport = -> [Pad017]
  ExternalGeometry = -> [Pad017]
  FullyConstrained = true
  MakeInternals = false
  MapMode = 5
  Placement = pos=(0,-3.6,8e-16) rot=(1,0,0;1.5708rad)
  sketch-geometry (20):
    g0: LineSegment StartX=-108 StartY=35.8 StartZ=0 EndX=-108 EndY=35 EndZ=0
    g1: LineSegment StartX=-108 StartY=35 StartZ=0 EndX=-97 EndY=35 EndZ=0
    g2: LineSegment StartX=-97 StartY=35 StartZ=0 EndX=-97 EndY=35.8 EndZ=0
    g3: LineSegment StartX=-97 StartY=35.8 StartZ=0 EndX=-108 EndY=35.8 EndZ=0
    g4: LineSegment StartX=-108 StartY=28.6 StartZ=0 EndX=-108 EndY=27.8 EndZ=0
    g5: LineSegment StartX=-108 StartY=27.8 StartZ=0 EndX=-97 EndY=27.8 EndZ=0
    g6: LineSegment StartX=-97 StartY=27.8 StartZ=0 EndX=-97 EndY=28.6 EndZ=0
    g7: LineSegment StartX=-97 StartY=28.6 StartZ=0 EndX=-108 EndY=28.6 EndZ=0
    g8: LineSegment StartX=-108 StartY=30.4 StartZ=0 EndX=-108 EndY=29.6 EndZ=0
    g9: LineSegment StartX=-108 StartY=29.6 StartZ=0 EndX=-97 EndY=29.6 EndZ=0
    g10: LineSegment StartX=-97 StartY=29.6 StartZ=0 EndX=-97 EndY=30.4 EndZ=0
    g11: LineSegment StartX=-97 StartY=30.4 StartZ=0 EndX=-108 EndY=30.4 EndZ=0
    g12: LineSegment StartX=-108 StartY=32.2 StartZ=0 EndX=-108 EndY=31.4 EndZ=0
    g13: LineSegment StartX=-108 StartY=31.4 StartZ=0 EndX=-97 EndY=31.4 EndZ=0
    g14: LineSegment StartX=-97 StartY=31.4 StartZ=0 EndX=-97 EndY=32.2 EndZ=0
    g15: LineSegment StartX=-97 StartY=32.2 StartZ=0 EndX=-108 EndY=32.2 EndZ=0
    g16: LineSegment StartX=-108 StartY=34 StartZ=0 EndX=-108 EndY=33.2 EndZ=0
    g17: LineSegment StartX=-108 StartY=33.2 StartZ=0 EndX=-97 EndY=33.2 EndZ=0
    g18: LineSegment StartX=-97 StartY=33.2 StartZ=0 EndX=-97 EndY=34 EndZ=0
    g19: LineSegment StartX=-97 StartY=34 StartZ=0 EndX=-108 EndY=34 EndZ=0
  constraints (55):
    c: Coincident(g1,g0)
    c: Horizontal(g1)
    c: Coincident(g2,g1)
    c: Vertical(g2)
    c: Coincident(g3,g2)
    c: Horizontal(g3)
    c: Coincident(g3,g0)
    c: DistanceX(g1,g1) = 11
    c: DistanceY(g2,g2) = 0.8
    c: Coincident(g5,g4)
    c: Horizontal(g5)
    c: Coincident(g6,g5)
    c: Vertical(g6)
    c: Coincident(g7,g6)
    c: Horizontal(g7)
    c: Coincident(g7,g4)
    c: Coincident(g9,g8)
    c: Horizontal(g9)
    c: Coincident(g10,g9)
    c: Vertical(g10)
    c: Coincident(g11,g10)
    c: Horizontal(g11)
    c: Coincident(g11,g8)
    c: Coincident(g13,g12)
    c: Horizontal(g13)
    c: Coincident(g14,g13)
    c: Vertical(g14)
    c: Coincident(g15,g14)
    c: Horizontal(g15)
    c: Coincident(g15,g12)
    c: Coincident(g17,g16)
    c: Horizontal(g17)
    c: Coincident(g18,g17)
    c: Vertical(g18)
    c: Coincident(g19,g18)
    c: Horizontal(g19)
    c: Coincident(g19,g16)
    c: Equal(g3,g19)
    c: Equal(g3,g15)
    c: Equal(g3,g11)
    c: Equal(g3,g7)
    c: Equal(g2,g18)
    c: Equal(g2,g14)
    c: Equal(g2,g10)
    c: Equal(g2,g6)
    c: DistanceY(g-4,g4) = 1
    c: DistanceY(g4,g8) = 1
    c: DistanceY(g8,g12) = 1
    c: DistanceY(g12,g16) = 1
    c: DistanceY(g16,g0) = 1
    c: Tangent(g0,g-5)
    c: Tangent(g16,g-5)
    c: Tangent(g12,g-5)
    c: Tangent(g8,g-5)
    c: Tangent(g4,g-5)
FEATURE [PartDesign::Chamfer] Chamfer009
  Angle = 45
  Base = -> Pad017 [Edge151,Edge154]
  BaseFeature = -> Pad017
  ChamferType = 1
  FlipDirection = false
  Refine = true
  Size = 1.5
  Size2 = 2.8
  SupportTransform = false
  Suppressed = false
  UseAllEdges = false
FEATURE [PartDesign::Pocket] Pocket009
  BaseFeature = -> Chamfer009
  Direction = (0,1,-2e-16)
  Length = 1
  Length2 = 5
  Profile = -> Sketch125
  ReferenceAxis = -> Sketch125 [N_Axis]
  Refine = true
  Suppressed = false
  Type = 0
FEATURE [PartDesign::Pad] Pad014
  BaseFeature = -> Pocket009
  Direction = (0,-1,2e-16)
  Length = 0.8
  Length2 = 10
  Profile = -> Sketch120
  ReferenceAxis = -> Sketch120 [N_Axis]
  Refine = true
  Suppressed = false
  Type = 0
FEATURE [Sketcher::SketchObject] Sketch124
  ArcFitTolerance = 1e-06
  AttachmentSupport = -> [Pad014]
  ExternalGeometry = -> [Binder001]
  FullyConstrained = true
  MakeInternals = false
  MapMode = 5
  Placement = pos=(0,-2.8,6e-16) rot=(1,0,0;1.5708rad)
  sketch-geometry (4):
    g0: LineSegment StartX=-129 StartY=39.2 StartZ=0 EndX=-131.599 EndY=31.2 EndZ=0
    g1: LineSegment StartX=-118 StartY=39.2 StartZ=0 EndX=-120.599 EndY=31.2 EndZ=0
    g2: LineSegment StartX=-129 StartY=39.2 StartZ=0 EndX=-118 EndY=39.2 EndZ=0
    g3: LineSegment StartX=-120.599 StartY=31.2 StartZ=0 EndX=-131.599 EndY=31.2 EndZ=0
  constraints (12):
    c: PointOnObject(g0,g-3)
    c: PointOnObject(g1,g-3)
    c: Parallel(g-4,g0)
    c: Parallel(g-4,g1)
    c: Coincident(g2,g0)
    c: Coincident(g2,g1)
    c: DistanceX(g2,g2) = 11
    c: DistanceY(g1,g1) = 8
    c: Coincident(g3,g1)
    c: Horizontal(g3)
    c: Coincident(g3,g0)
    c: DistanceX(g1,g-3) = 118
FEATURE [PartDesign::Pad] Pad018
  BaseFeature = -> Pad014
  Direction = (0,-1,2e-16)
  Length = 1.2
  Length2 = 10
  Profile = -> Sketch124
  ReferenceAxis = -> Sketch124 [N_Axis]
  Refine = true
  Suppressed = false
  Type = 0
FEATURE [Sketcher::SketchObject] Sketch126
  ArcFitTolerance = 1e-06
  AttachmentSupport = -> [Pad018]
  ExternalGeometry = -> [Pad018]
  FullyConstrained = true
  MakeInternals = false
  MapMode = 5
  Placement = pos=(0,-4,0) rot=(1,0,0;1.5708rad)
  sketch-geometry (8):
    g0: LineSegment StartX=-129.877 StartY=36.5 StartZ=0 EndX=-130.137 EndY=35.7 EndZ=0
    g1: LineSegment StartX=-130.69 StartY=34 StartZ=0 EndX=-130.95 EndY=33.2 EndZ=0
    g2: LineSegment StartX=-129.877 StartY=36.5 StartZ=0 EndX=-118.877 EndY=36.5 EndZ=0
    g3: LineSegment StartX=-130.137 StartY=35.7 StartZ=0 EndX=-119.137 EndY=35.7 EndZ=0
    g4: LineSegment StartX=-130.69 StartY=34 StartZ=0 EndX=-119.69 EndY=34 EndZ=0
    g5: LineSegment StartX=-130.95 StartY=33.2 StartZ=0 EndX=-119.95 EndY=33.2 EndZ=0
    g6: LineSegment StartX=-118.877 StartY=36.5 StartZ=0 EndX=-119.137 EndY=35.7 EndZ=0
    g7: LineSegment StartX=-119.69 StartY=34 StartZ=0 EndX=-119.95 EndY=33.2 EndZ=0
  constraints (20):
    c: Coincident(g2,g0)
    c: Horizontal(g2)
    c: Coincident(g3,g0)
    c: Horizontal(g3)
    c: Coincident(g4,g1)
    c: Horizontal(g4)
    c: Coincident(g5,g1)
    c: Horizontal(g5)
    c: Coincident(g6,g2)
    c: Coincident(g6,g3)
    c: Coincident(g7,g4)
    c: Coincident(g7,g5)
    c: Tangent(g0,g-4)
    c: Tangent(g6,g-5)
    c: Tangent(g1,g-4)
    c: Tangent(g7,g-5)
    c: DistanceY(g3,g2) = 0.8
    c: DistanceY(g5,g4) = 0.8
    c: DistanceY(g-6,g1) = 2
    c: DistanceY(g-6,g0) = 4.5
FEATURE [PartDesign::Chamfer] Chamfer008
  Angle = 45
  Base = -> Pad018 [Edge257]
  BaseFeature = -> Pad018
  ChamferType = 1
  FlipDirection = false
  Refine = true
  Size = 1
  Size2 = 6
  SupportTransform = false
  Suppressed = false
  UseAllEdges = false
FEATURE [PartDesign::Pocket] Pocket010
  BaseFeature = -> Chamfer008
  Direction = (0,1,-2e-16)
  Length = 1
  Length2 = 5
  Profile = -> Sketch126
  ReferenceAxis = -> Sketch126 [N_Axis]
  Refine = true
  Suppressed = false
  Type = 0
FEATURE [PartDesign::Pad] Pad015
  BaseFeature = -> Pocket010
  Direction = (0,-1,2e-16)
  Length = 2
  Length2 = 10
  Profile = -> Sketch121
  ReferenceAxis = -> Sketch121 [N_Axis]
  Refine = true
  Suppressed = false
  Type = 0
FEATURE [PartDesign::Pad] Pad016
  BaseFeature = -> Pad015
  Direction = (0,-1,2e-16)
  Length = 1.6
  Length2 = 10
  Profile = -> Sketch122
  ReferenceAxis = -> Sketch122 [N_Axis]
  Refine = true
  Suppressed = false
  Type = 0
FEATURE [Sketcher::SketchObject] Sketch127
  ArcFitTolerance = 1e-06
  AttachmentSupport = -> [Pad016]
  ExternalGeometry = -> [Pad016]
  FullyConstrained = true
  MakeInternals = false
  MapMode = 5
  Placement = pos=(0,0,-80.4316) rot=(1,0,0;3.14159rad)
  sketch-geometry (8):
    g0: LineSegment StartX=-176.685 StartY=3.6 StartZ=0 EndX=-186.685 EndY=3.6 EndZ=0
    g1: LineSegment [constr] StartX=-186.685 StartY=3.6 StartZ=0 EndX=-186.685 EndY=-9e-16 EndZ=0
    g2: LineSegment StartX=-176.685 StartY=3.6 StartZ=0 EndX=-176.685 EndY=0 EndZ=0
    g3: ArcOfEllipse CenterX=-186.685 CenterY=-9e-16 CenterZ=0 NormalX=0 NormalY=0 NormalZ=1 MajorRadius=10 MinorRadius=3.6 AngleXU=1e-16 StartAngle=0 EndAngle=1.5708
    g4: LineSegment [constr] StartX=-176.685 StartY=-2e-15 StartZ=0 EndX=-196.685 EndY=-2e-15 EndZ=0
    g5: LineSegment [constr] StartX=-186.685 StartY=3.6 StartZ=0 EndX=-186.685 EndY=-3.6 EndZ=0
    g6: GeomPoint [constr] X=-177.356 Y=0 Z=0
    g7: GeomPoint [constr] X=-196.015 Y=-1.9e-15 Z=0
  constraints (13):
    c: Coincident(g0,g-4)
    c: PointOnObject(g0,g-4)
    c: DistanceX(g0,g0) = 10
    c: Coincident(g1,g0)
    c: PointOnObject(g1,g-5)
    c: Vertical(g1)
    c: Coincident(g2,g0)
    c: Coincident(g2,g-5)
    c: InternalAlignment(g4-g7 -> g3) x4
    c: Coincident(g3,g1)
    c: Coincident(g3,g0)
    c: Coincident(g3,g2)
    c: Horizontal(g4)
FEATURE [Sketcher::SketchObject] Sketch128
  ArcFitTolerance = 1e-06
  AttachmentSupport = -> [Pad016]
  ExternalGeometry = -> [Pad016]
  FullyConstrained = true
  MakeInternals = false
  MapMode = 5
  Placement = pos=(0,0,-80.4316) rot=(1,0,0;3.14159rad)
  sketch-geometry (8):
    g0: LineSegment StartX=-215.932 StartY=3.6 StartZ=0 EndX=-215.932 EndY=-1.3e-15 EndZ=0
    g1: LineSegment StartX=-215.932 StartY=3.6 StartZ=0 EndX=-205.932 EndY=3.6 EndZ=0
    g2: LineSegment [constr] StartX=-205.932 StartY=3.6 StartZ=0 EndX=-205.932 EndY=-9e-16 EndZ=0
    g3: ArcOfEllipse CenterX=-205.932 CenterY=-9e-16 CenterZ=0 NormalX=0 NormalY=0 NormalZ=1 MajorRadius=10 MinorRadius=3.6 AngleXU=-3.14159 StartAngle=4.71239 EndAngle=6.28319
    g4: LineSegment [constr] StartX=-215.932 StartY=-1e-15 StartZ=0 EndX=-195.932 EndY=-1e-15 EndZ=0
    g5: LineSegment [constr] StartX=-205.932 StartY=-3.6 StartZ=0 EndX=-205.932 EndY=3.6 EndZ=0
    g6: GeomPoint [constr] X=-215.262 Y=-2e-15 Z=0
    g7: GeomPoint [constr] X=-196.602 Y=-1e-15 Z=0
  constraints (13):
    c: Coincident(g0,g-4)
    c: Coincident(g0,g-5)
    c: Coincident(g1,g0)
    c: PointOnObject(g1,g-3)
    c: DistanceX(g1,g1) = 10
    c: Coincident(g2,g1)
    c: Vertical(g2)
    c: PointOnObject(g2,g-5)
    c: InternalAlignment(g4-g7 -> g3) x4
    c: Coincident(g3,g2)
    c: Coincident(g3,g1)
    c: Coincident(g3,g0)
    c: Horizontal(g4)
FEATURE [PartDesign::SubtractivePipe] SubtractivePipe002
  AuxilleryCurvelinear = true
  AuxillerySpineTangent = false
  BaseFeature = -> Pad016
  Binormal = (0,0,0)
  Mode = 0
  Profile = -> Sketch127
  Refine = true
  Spine = -> Pad016 [Edge254]
  SpineTangent = false
  Suppressed = false
  Transformation = 0
  Transition = 0
FEATURE [PartDesign::SubtractivePipe] SubtractivePipe003
  AuxilleryCurvelinear = true
  AuxillerySpineTangent = false
  BaseFeature = -> SubtractivePipe002
  Binormal = (0,0,0)
  Mode = 0
  Profile = -> Sketch128
  Refine = true
  Spine = -> Pad016 [Edge256,Edge251,Edge252]
  SpineTangent = false
  Suppressed = false
  Transformation = 0
  Transition = 0
FEATURE [Sketcher::SketchObject] Sketch129
  ArcFitTolerance = 1e-06
  AttachmentSupport = -> [Pad016]
  ExternalGeometry = -> [Binder001]
  FullyConstrained = true
  MakeInternals = false
  MapMode = 5
  Placement = pos=(0,-3.6,0) rot=(1,0,0;1.5708rad)
  sketch-geometry (12):
    g0: LineSegment [constr] StartX=-192.176 StartY=-3.18451 StartZ=0 EndX=-181.223 EndY=20.303 EndZ=0
    g1: LineSegment [constr] StartX=-202.765 StartY=20.303 StartZ=0 EndX=-181.223 EndY=20.303 EndZ=0
    g2: LineSegment StartX=-202.765 StartY=20.303 StartZ=0 EndX=-181.223 EndY=20.303 EndZ=0
    g3: LineSegment StartX=-192.176 StartY=-3.18451 StartZ=0 EndX=-196.804 EndY=-13.1107 EndZ=0
    g4: ArcOfCircle CenterX=-207.583 CenterY=4 CenterZ=0 NormalX=0 NormalY=0 NormalZ=1 AngleXU=0 Radius=17 StartAngle=5.84685 EndAngle=7.56663
    g5: ArcOfEllipse CenterX=-181.223 CenterY=8.55923 CenterZ=0 NormalX=0 NormalY=0 NormalZ=1 MajorRadius=23.4779 MinorRadius=11.7437 AngleXU=2e-16 StartAngle=4.71239 EndAngle=7.85398
    g6: LineSegment [constr] StartX=-157.745 StartY=8.55923 StartZ=0 EndX=-204.701 EndY=8.55923 EndZ=0
    g7: LineSegment [constr] StartX=-181.223 StartY=20.303 StartZ=0 EndX=-181.223 EndY=-3.18451 EndZ=0
    g8: GeomPoint [constr] X=-160.894 Y=8.55923 Z=0
    g9: GeomPoint [constr] X=-201.553 Y=8.55923 Z=0
    g10: ArcOfCircle CenterX=-181.223 CenterY=-20.3763 CenterZ=0 NormalX=0 NormalY=0 NormalZ=1 AngleXU=0 Radius=17.1918 StartAngle=1.57079 EndAngle=2.70526
    g11: GeomPoint [constr] X=-181.223 Y=-3.18451 Z=0
  constraints (23):
    c: Coincident(g0,g-5)
    c: Coincident(g1,g-6)
    c: Horizontal(g1)
    c: Coincident(g1,g0)
    c: Parallel(g0,g-4)
    c: Coincident(g2,g1)
    c: Coincident(g2,g0)
    c: Coincident(g3,g0)
    c: Equal(g4,g-5)
    c: Coincident(g4,g1)
    c: Coincident(g4,g0)
    c: InternalAlignment(g6-g9 -> g5) x4
    c: Vertical(g5,g0)
    c: Horizontal(g6)
    c: Coincident(g5,g0)
    c: DistanceX(g6,g-3) = 10.1
    c: Tangent(g10,g3) = -1.5708
    c: PointOnObject(g11,g10)
    c: Tangent(g5,g10,g11) = 1.5708
    c: Coincident(g10,g5)
    c: Coincident(g11,g7)
    c: Parallel(g3,g-4)
    c: Horizontal(g5,g0)
FEATURE [Sketcher::SketchObject] Sketch130
  ArcFitTolerance = 1e-06
  AttachmentOffset = pos=(0,0,-1.6) rot=(0,0,1;0rad)
  AttachmentSupport = -> [Pad016]
  ExternalGeometry = -> [Binder001]
  FullyConstrained = true
  MakeInternals = false
  MapMode = 5
  Placement = pos=(0,-2,-4e-16) rot=(1,0,0;1.5708rad)
  sketch-geometry (12):
    g0: LineSegment [constr] StartX=-192.176 StartY=-3.18451 StartZ=0 EndX=-181.223 EndY=20.303 EndZ=0
    g1: LineSegment [constr] StartX=-202.765 StartY=20.303 StartZ=0 EndX=-181.223 EndY=20.303 EndZ=0
    g2: LineSegment StartX=-202.765 StartY=20.303 StartZ=0 EndX=-181.223 EndY=20.303 EndZ=0
    g3: LineSegment StartX=-192.176 StartY=-3.18451 StartZ=0 EndX=-193.827 EndY=-6.72678 EndZ=0
    g4: ArcOfCircle CenterX=-207.583 CenterY=4 CenterZ=0 NormalX=0 NormalY=0 NormalZ=1 AngleXU=0 Radius=17 StartAngle=5.84685 EndAngle=7.56663
    g5: ArcOfEllipse CenterX=-181.223 CenterY=10.803 CenterZ=0 NormalX=0 NormalY=0 NormalZ=1 MajorRadius=14.4779 MinorRadius=9.5 AngleXU=0 StartAngle=4.71239 EndAngle=7.85398
    g6: LineSegment [constr] StartX=-166.745 StartY=10.803 StartZ=0 EndX=-195.701 EndY=10.803 EndZ=0
    g7: LineSegment [constr] StartX=-181.223 StartY=20.303 StartZ=0 EndX=-181.223 EndY=1.30297 EndZ=0
    g8: GeomPoint [constr] X=-170.298 Y=10.803 Z=0
    g9: GeomPoint [constr] X=-192.148 Y=10.803 Z=0
    g10: ArcOfCircle CenterX=-181.223 CenterY=-12.6042 CenterZ=0 NormalX=0 NormalY=0 NormalZ=1 AngleXU=0 Radius=13.9072 StartAngle=1.5708 EndAngle=2.70526
    g11: GeomPoint [constr] X=-181.223 Y=1.30297 Z=0
  constraints (23):
    c: Coincident(g0,g-5)
    c: Coincident(g1,g-6)
    c: Horizontal(g1)
    c: Coincident(g1,g0)
    c: Parallel(g0,g-4)
    c: Coincident(g2,g1)
    c: Coincident(g2,g0)
    c: Coincident(g3,g0)
    c: Equal(g4,g-5)
    c: Coincident(g4,g1)
    c: Coincident(g4,g0)
    c: InternalAlignment(g6-g9 -> g5) x4
    c: Vertical(g5,g0)
    c: Horizontal(g6)
    c: Coincident(g5,g0)
    c: DistanceX(g6,g-3) = 19.1
    c: Tangent(g10,g3) = -1.5708
    c: PointOnObject(g11,g10)
    c: Tangent(g5,g10,g11) = 1.5708
    c: Coincident(g10,g5)
    c: Coincident(g11,g7)
    c: Parallel(g3,g-4)
    c: DistanceY(g5,g0) = 19
FEATURE [Part::Part2DObjectPython] Clone2D001  label="Sketch130 (2D)"  # Draft 2D object (typed FeaturePython)
  Fuse = false
  Objects = -> [Sketch130]
  Placement = pos=(0,-2,-4e-16) rot=(1,0,0;1.5708rad)
  Scale = (1,1,1)
FEATURE [Sketcher::SketchObject] Sketch131
  ArcFitTolerance = 1e-06
  AttachmentOffset = pos=(0,0,-3.5) rot=(0,0,1;0rad)
  AttachmentSupport = -> [Pad016]
  ExternalGeometry = -> [Binder001]
  FullyConstrained = true
  MakeInternals = false
  MapMode = 5
  Placement = pos=(0,-0.1,-8e-16) rot=(1,0,0;1.5708rad)
  sketch-geometry (1):
    g0: GeomPoint X=-197.47 Y=8.55923 Z=0
  constraints (1):
    c: Symmetric(g-6,g-4,g0)
FEATURE [PartDesign::SubtractiveLoft] SubtractiveLoft002
  BaseFeature = -> SubtractivePipe003
  Closed = false
  Profile = -> Sketch129
  Refine = true
  Ruled = false
  Sections = -> [Sketch130]
  Suppressed = false
FEATURE [PartDesign::SubtractiveLoft] SubtractiveLoft003
  BaseFeature = -> SubtractiveLoft002
  Closed = false
  Profile = -> Clone2D001
  Refine = true
  Ruled = false
  Sections = -> [Sketch131]
  Suppressed = false
FEATURE [PartDesign::Chamfer] Chamfer010
  Angle = 45
  Base = -> SubtractiveLoft003 [Edge200,Edge201,Edge203,Edge202,Edge194]
  BaseFeature = -> SubtractiveLoft003
  ChamferType = 0
  FlipDirection = false
  Refine = true
  Size = 1.5
  Size2 = 1
  SupportTransform = false
  Suppressed = false
  UseAllEdges = false
FEATURE [PartDesign::Chamfer] Chamfer011
  Angle = 45
  Base = -> Chamfer010 [Edge15]
  BaseFeature = -> Chamfer010
  ChamferType = 0
  FlipDirection = false
  Refine = true
  Size = 1.6
  Size2 = 1
  SupportTransform = false
  Suppressed = false
  UseAllEdges = false
FEATURE [PartDesign::Chamfer] Chamfer012
  Angle = 45
  Base = -> Chamfer011 [Edge10]
  BaseFeature = -> Chamfer011
  ChamferType = 0
  FlipDirection = false
  Refine = true
  Size = 3.5
  Size2 = 1
  SupportTransform = false
  Suppressed = false
  UseAllEdges = false
FEATURE [PartDesign::Chamfer] Chamfer013
  Angle = 45
  Base = -> Chamfer012 [Edge145,Edge94]
  BaseFeature = -> Chamfer012
  ChamferType = 0
  FlipDirection = false
  Refine = true
  Size = 1.9
  Size2 = 1
  SupportTransform = false
  Suppressed = false
  UseAllEdges = false
FEATURE [Sketcher::SketchObject] Sketch132
  ArcFitTolerance = 1e-06
  AttachmentSupport = -> [Pad016]
  ExternalGeometry = -> [Binder001]
  FullyConstrained = true
  MakeInternals = false
  MapMode = 5
  Placement = pos=(0,-3.6,0) rot=(1,0,0;1.5708rad)
  sketch-geometry (3):
    g0: LineSegment [constr] StartX=-215.42 StartY=-53.0314 StartZ=0 EndX=-167.782 EndY=-53.0314 EndZ=0
    g1: Circle CenterX=-191.282 CenterY=-53.0314 CenterZ=0 NormalX=0 NormalY=0 NormalZ=1 AngleXU=0 Radius=11.5
    g2: Circle CenterX=-191.282 CenterY=-53.0314 CenterZ=0 NormalX=0 NormalY=0 NormalZ=1 AngleXU=0 Radius=10.7
  constraints (8):
    c: Coincident(g0,g-3)
    c: PointOnObject(g0,g-4)
    c: Horizontal(g0)
    c: Diameter(g1) = 23
    c: PointOnObject(g1,g0)
    c: DistanceX(g1,g0) = 23.5
    c: Diameter(g2) = 21.4
    c: Coincident(g2,g1)
FEATURE [PartDesign::Fillet] Fillet007
  Base = -> Chamfer013 [Edge83]
  BaseFeature = -> Chamfer013
  Radius = 1.1
  Refine = true
  SupportTransform = false
  Suppressed = false
  UseAllEdges = false
FEATURE [PartDesign::Fillet] Fillet008
  Base = -> Fillet007 [Edge76]
  BaseFeature = -> Fillet007
  Radius = 1.9
  Refine = true
  SupportTransform = false
  Suppressed = false
  UseAllEdges = false
FEATURE [PartDesign::Pocket] Pocket011
  BaseFeature = -> Fillet008
  Direction = (0,1,-2e-16)
  Length = 0.8
  Length2 = 5
  Profile = -> Sketch132
  ReferenceAxis = -> Sketch132 [N_Axis]
  Refine = true
  Suppressed = false
  Type = 0
FEATURE [Part::Part2DObjectPython] ShapeString  # Draft 2D object (typed FeaturePython)
  FontFile = <path>
  Fuse = false
  Justification = 6
  JustificationReference = 0
  KeepLeftMargin = false
  MakeFace = true
  ObliqueAngle = 0
  Placement = pos=(-199,-3.6,-57.5) rot=(1,0,0;1.5708rad)
  ScaleToSize = true
  Size = 10
  String = AS
  Tracking = 0
FEATURE [PartDesign::Pocket] Pocket012
  BaseFeature = -> Pocket011
  Direction = (0,1,0)
  Length = 1
  Length2 = 5
  Profile = -> ShapeString
  ReferenceAxis = -> ShapeString [N_Axis]
  Refine = true
  Suppressed = false
  Type = 0
FEATURE [PartDesign::Body] Body007  label="lato DX"
  AllowCompound = false
  Group = -> [Binder001,Sketch114,Pad011,Chamfer014,Sketch115,Pocket006,Sketch116,Pad012,Sketch117,Pocket007,Sketch118,Pad013,Sketch119,Pocket008,Pad017,Chamfer009,Pocket009,Sketch123,Sketch120,Pad014,Pad018,Chamfer008,Pocket010,Sketch121,Pad015,Sketch122,Pad016,Sketch124,Sketch125,Sketch126,Sketch127,Sketch128,SubtractivePipe002,SubtractivePipe003,Sketch129,Sketch130,Clone2D001,Sketch131,SubtractiveLoft002,+11 more]
  Origin = -> Origin007
  Tip = -> Pocket012
FEATURE [Sketcher::SketchObject] Sketch133
  ArcFitTolerance = 1e-06
  AttachmentSupport = -> [Binder]
  ExternalGeometry = -> [Binder]
  FullyConstrained = true
  MakeInternals = false
  MapMode = 5
  Placement = pos=(0,9e-16,0) rot=(0,0.707107,0.707107;3.14159rad)
  sketch-geometry (30):
    g0: LineSegment StartX=0 StartY=39.2 StartZ=0 EndX=0 EndY=3.2 EndZ=0
    g1: LineSegment StartX=0 StartY=3.2 StartZ=0 EndX=82.8 EndY=3.2 EndZ=0
    g2: LineSegment StartX=82.8 StartY=3.2 StartZ=0 EndX=82.8 EndY=6.2 EndZ=0
    g3: LineSegment StartX=82.8 StartY=6.2 StartZ=0 EndX=91.752 EndY=6.2 EndZ=0
    g4: LineSegment StartX=0 StartY=39.2 StartZ=0 EndX=195.887 EndY=39.2 EndZ=0
    g5: LineSegment StartX=195.887 StartY=39.2 StartZ=0 EndX=202.765 EndY=20.303 EndZ=0
    g6: LineSegment StartX=192.333 StartY=24.9893 StartZ=0 EndX=196.467 EndY=26.4942 EndZ=0
    g7: LineSegment StartX=196.467 StartY=26.4942 StartZ=0 EndX=194.073 EndY=33.0721 EndZ=0
    g8: LineSegment StartX=194.073 StartY=33.0721 StartZ=0 EndX=189.939 EndY=31.5672 EndZ=0
    g9: LineSegment StartX=189.939 StartY=31.5672 StartZ=0 EndX=192.333 EndY=24.9893 EndZ=0
    g10: ArcOfCircle CenterX=107.6 CenterY=4 CenterZ=0 NormalX=0 NormalY=0 NormalZ=1 AngleXU=0 Radius=16 StartAngle=1.5708 EndAngle=3.00366
    g11: LineSegment StartX=107.6 StartY=20 StartZ=0 EndX=132.428 EndY=20 EndZ=0
    g12: ArcOfCircle [constr] CenterX=132.428 CenterY=4 CenterZ=0 NormalX=0 NormalY=0 NormalZ=1 AngleXU=0 Radius=16 StartAngle=0.314159 EndAngle=1.5708
    g13: LineSegment StartX=147.645 StartY=8.94427 StartZ=0 EndX=176.685 EndY=-80.4316 EndZ=0
    g14: LineSegment StartX=176.685 StartY=-80.4316 StartZ=0 EndX=215.932 EndY=-80.4316 EndZ=0
    g15: ArcOfCircle CenterX=207.583 CenterY=4 CenterZ=0 NormalX=0 NormalY=0 NormalZ=1 AngleXU=0 Radius=17 StartAngle=1.85815 EndAngle=3.57792
    g16: ArcOfCircle CenterX=184.801 CenterY=-67.3089 CenterZ=0 NormalX=0 NormalY=0 NormalZ=1 AngleXU=0 Radius=33.7833 StartAngle=5.88425 EndAngle=6.71952
    g17: LineSegment StartX=192.176 StartY=-3.18451 StartZ=0 EndX=215.42 EndY=-53.0314 EndZ=0
    g18: Circle CenterX=5.6 CenterY=34.8 CenterZ=0 NormalX=0 NormalY=0 NormalZ=1 AngleXU=0 Radius=1.8
    g19: Circle CenterX=5.6 CenterY=7.6 CenterZ=0 NormalX=0 NormalY=0 NormalZ=1 AngleXU=0 Radius=1.8
    g20: Circle CenterX=78.51 CenterY=34.8 CenterZ=0 NormalX=0 NormalY=0 NormalZ=1 AngleXU=0 Radius=1.8
    g21: Circle CenterX=78.51 CenterY=7.6 CenterZ=0 NormalX=0 NormalY=0 NormalZ=1 AngleXU=0 Radius=1.8
    g22: Circle CenterX=184.08 CenterY=34.8 CenterZ=0 NormalX=0 NormalY=0 NormalZ=1 AngleXU=0 Radius=1.8
    g23: Circle CenterX=179.305 CenterY=-76.8316 CenterZ=0 NormalX=0 NormalY=0 NormalZ=1 AngleXU=0 Radius=1.8
    g24: Circle CenterX=213.443 CenterY=-76.8316 CenterZ=0 NormalX=0 NormalY=0 NormalZ=1 AngleXU=0 Radius=1.8
    g25: Circle CenterX=19 CenterY=21.2 CenterZ=0 NormalX=0 NormalY=0 NormalZ=1 AngleXU=0 Radius=6.3
    g26: Circle CenterX=42 CenterY=21.2 CenterZ=0 NormalX=0 NormalY=0 NormalZ=1 AngleXU=0 Radius=6.3
    g27: Circle CenterX=65 CenterY=21.2 CenterZ=0 NormalX=0 NormalY=0 NormalZ=1 AngleXU=0 Radius=6.3
    g28: LineSegment StartX=132.428 StartY=20 StartZ=0 EndX=144.053 EndY=20 EndZ=0
    g29: LineSegment StartX=147.645 StartY=8.94427 StartZ=0 EndX=144.053 EndY=20 EndZ=0
  constraints (65):
    c: Coincident(g0,g-4)
    c: Coincident(g0,g-5)
    c: Coincident(g1,g0)
    c: Coincident(g1,g-6)
    c: Coincident(g2,g1)
    c: Coincident(g2,g-7)
    c: Coincident(g3,g2)
    c: Coincident(g3,g-8)
    c: Coincident(g4,g0)
    c: Coincident(g4,g-16)
    c: Coincident(g5,g4)
    c: Coincident(g5,g-16)
    c: Coincident(g6,g-20)
    c: Coincident(g6,g-21)
    c: Coincident(g7,g6)
    c: Coincident(g7,g-23)
    c: Coincident(g8,g7)
    c: Coincident(g8,g-22)
    c: Coincident(g9,g8)
    c: Coincident(g9,g6)
    c: Equal(g10,g-8)
    c: Coincident(g10,g3)
    c: Coincident(g10,g-9)
    c: Coincident(g11,g10)
    c: Coincident(g11,g-10)
    c: Equal(g12,g-10)
    c: Coincident(g12,g11)
    c: Coincident(g12,g-11)
    c: Coincident(g13,g12)
    c: Coincident(g13,g-12)
    c: Coincident(g14,g13)
    c: Coincident(g14,g-13)
    c: Equal(g15,g-15)
    c: Coincident(g15,g5)
    c: Coincident(g15,g-15)
    c: Equal(g16,g-13)
    c: Coincident(g16,g14)
    c: Coincident(g16,g-14)
    c: Coincident(g17,g15)
    c: Coincident(g17,g16)
    c: Equal(g18,g-28)
    c: Equal(g19,g-29)
    c: Equal(g20,g-26)
    c: Equal(g21,g-27)
    c: Equal(g22,g-17)
    c: Equal(g24,g-25)
    c: Equal(g23,g-24)
    c: Coincident(g23,g-24)
    c: Coincident(g24,g-25)
    c: Coincident(g22,g-17)
    c: Coincident(g20,g-26)
    c: Coincident(g21,g-27)
    c: Coincident(g18,g-28)
    c: Coincident(g19,g-29)
    c: Equal(g25,g-30)
    c: Equal(g26,g-31)
    c: Equal(g27,g-32)
    c: Coincident(g25,g-30)
    c: Coincident(g26,g-31)
    c: Coincident(g27,g-32)
    c: Parallel(g28,g11)
    c: Parallel(g29,g13)
    c: Coincident(g28,g11)
    c: Coincident(g29,g12)
    c: Coincident(g29,g28)
FEATURE [PartDesign::Pad] Pad019
  Direction = (0,1,-2e-16)
  Length = 2
  Length2 = 10
  Profile = -> Sketch133
  ReferenceAxis = -> Sketch133 [N_Axis]
  Refine = true
  Suppressed = false
  Type = 0
FEATURE [Sketcher::SketchObject] Sketch091  label="Sketch091 - forma anteriore"
  ArcFitTolerance = 1e-06
  AttachmentSupport = -> [Pad019]
  ExternalGeometry = -> [Binder]
  FullyConstrained = true
  MakeInternals = false
  MapMode = 5
  Placement = pos=(0,2,0) rot=(0,0.707107,0.707107;3.14159rad)
  sketch-geometry (12):
    g0: Circle CenterX=5.6 CenterY=34.8 CenterZ=0 NormalX=0 NormalY=0 NormalZ=1 AngleXU=0 Radius=1.8
    g1: Circle CenterX=5.6 CenterY=7.6 CenterZ=0 NormalX=0 NormalY=0 NormalZ=1 AngleXU=0 Radius=1.8
    g2: Circle CenterX=78.51 CenterY=34.8 CenterZ=0 NormalX=0 NormalY=0 NormalZ=1 AngleXU=0 Radius=1.8
    g3: Circle CenterX=78.51 CenterY=7.6 CenterZ=0 NormalX=0 NormalY=0 NormalZ=1 AngleXU=0 Radius=1.8
    g4: LineSegment StartX=0 StartY=39.2 StartZ=0 EndX=0 EndY=3.2 EndZ=0
    g5: LineSegment StartX=0 StartY=3.2 StartZ=0 EndX=82.8 EndY=3.2 EndZ=0
    g6: LineSegment StartX=82.8 StartY=3.2 StartZ=0 EndX=82.8 EndY=39.2 EndZ=0
    g7: LineSegment StartX=82.8 StartY=39.2 StartZ=0 EndX=0 EndY=39.2 EndZ=0
    g8: ArcOfCircle CenterX=19 CenterY=21.2 CenterZ=0 NormalX=0 NormalY=0 NormalZ=1 AngleXU=0 Radius=10 StartAngle=1.5708 EndAngle=4.71239
    g9: ArcOfCircle CenterX=65 CenterY=21.2 CenterZ=0 NormalX=0 NormalY=0 NormalZ=1 AngleXU=0 Radius=10 StartAngle=4.71239 EndAngle=7.85398
    g10: LineSegment StartX=19 StartY=31.2 StartZ=0 EndX=65 EndY=31.2 EndZ=0
    g11: LineSegment StartX=19 StartY=11.2 StartZ=0 EndX=65 EndY=11.2 EndZ=0
  constraints (25):
    c: Equal(g2,g-7)
    c: Equal(g3,g-8)
    c: Equal(g1,g-13)
    c: Equal(g0,g-12)
    c: Coincident(g0,g-12)
    c: Coincident(g1,g-13)
    c: Coincident(g3,g-8)
    c: Coincident(g2,g-7)
    c: Coincident(g4,g-4)
    c: Coincident(g4,g-5)
    c: Coincident(g5,g4)
    c: Coincident(g5,g-6)
    c: Coincident(g6,g5)
    c: PointOnObject(g6,g-3)
    c: Vertical(g6)
    c: Coincident(g7,g6)
    c: Coincident(g7,g4)
    c: Tangent(g8,g10) = 1.5708
    c: Tangent(g8,g11) = -1.5708
    c: Tangent(g9,g10) = 1.5708
    c: Tangent(g9,g11) = -1.5708
    c: Equal(g8,g9)
    c: Radius(g8) = 10
    c: Coincident(g8,g-11)
    c: Coincident(g9,g-9)
FEATURE [Sketcher::SketchObject] Sketch093  label="Sketch093 - scavi interni pulsanti"
  ArcFitTolerance = 1e-06
  AttachmentSupport = -> [Pad019]
  ExternalGeometry = -> [Binder]
  FullyConstrained = true
  MakeInternals = false
  MapMode = 5
  Placement = pos=(0,1.8e-15,0) rot=(1,0,0;1.5708rad)
  sketch-geometry (3):
    g0: Circle CenterX=-65 CenterY=21.2 CenterZ=0 NormalX=0 NormalY=0 NormalZ=1 AngleXU=0 Radius=7.3
    g1: Circle CenterX=-42 CenterY=21.2 CenterZ=0 NormalX=0 NormalY=0 NormalZ=1 AngleXU=0 Radius=7.3
    g2: Circle CenterX=-19 CenterY=21.2 CenterZ=0 NormalX=0 NormalY=0 NormalZ=1 AngleXU=0 Radius=7.3
  constraints (6):
    c: Coincident(g0,g-3)
    c: Coincident(g1,g-4)
    c: Coincident(g2,g-5)
    c: Diameter(g0) = 14.6
    c: Diameter(g1) = 14.6
    c: Diameter(g2) = 14.6
FEATURE [Sketcher::SketchObject] Sketch094  label="Sketch094 - forma centrale"
  ArcFitTolerance = 1e-06
  AttachmentSupport = -> [Pad019]
  ExternalGeometry = -> [Binder]
  FullyConstrained = true
  MakeInternals = false
  MapMode = 5
  Placement = pos=(0,2,0) rot=(0,0.707107,0.707107;3.14159rad)
  sketch-geometry (4):
    g0: LineSegment StartX=137.815 StartY=39.2 StartZ=0 EndX=142.655 EndY=24.303 EndZ=0
    g1: LineSegment StartX=110.815 StartY=24.303 StartZ=0 EndX=142.655 EndY=24.303 EndZ=0
    g2: LineSegment StartX=137.815 StartY=39.2 StartZ=0 EndX=110.815 EndY=39.2 EndZ=0
    g3: ArcOfCircle CenterX=92.2534 CenterY=31.7515 CenterZ=0 NormalX=0 NormalY=0 NormalZ=1 AngleXU=0 Radius=20 StartAngle=5.90156 EndAngle=6.66481
  constraints (12):
    c: PointOnObject(g0,g-3)
    c: Tangent(g0,g-5)
    c: Horizontal(g1)
    c: Coincident(g1,g0)
    c: Coincident(g2,g0)
    c: PointOnObject(g2,g-3)
    c: DistanceX(g2,g2) = 27
    c: Vertical(g1,g2)
    c: Coincident(g3,g2)
    c: Radius(g3) = 20
    c: Coincident(g3,g1)
    c: DistanceY(g-6,g0) = 4
FEATURE [Sketcher::SketchObject] Sketch095  label="Sketch095 - forma posteriore"
  ArcFitTolerance = 1e-06
  AttachmentSupport = -> [Pad019]
  ExternalGeometry = -> [Binder]
  FullyConstrained = true
  MakeInternals = false
  MapMode = 5
  Placement = pos=(0,2,0) rot=(0,0.707107,0.707107;3.14159rad)
  sketch-geometry (15):
    g0: LineSegment StartX=137.815 StartY=39.2 StartZ=0 EndX=143.955 EndY=20.303 EndZ=0
    g1: LineSegment StartX=143.955 StartY=20.303 StartZ=0 EndX=190.141 EndY=20.303 EndZ=0
    g2: ArcOfCircle CenterX=184.08 CenterY=34.8 CenterZ=0 NormalX=0 NormalY=0 NormalZ=1 AngleXU=0 Radius=3.5 StartAngle=3.49066 EndAngle=4.71239
    g3: LineSegment StartX=180.791 StartY=33.6029 StartZ=0 EndX=178.754 EndY=39.2 EndZ=0
    g4: LineSegment StartX=184.08 StartY=31.3 StartZ=0 EndX=186.139 EndY=31.3 EndZ=0
    g5: LineSegment StartX=190.141 StartY=20.303 StartZ=0 EndX=186.139 EndY=31.3 EndZ=0
    g6: LineSegment StartX=137.815 StartY=39.2 StartZ=0 EndX=156.815 EndY=39.2 EndZ=0
    g7: LineSegment StartX=178.754 StartY=39.2 StartZ=0 EndX=168.815 EndY=39.2 EndZ=0
    g8: LineSegment StartX=156.815 StartY=31.2 StartZ=0 EndX=168.815 EndY=31.2 EndZ=0
    g9: ArcOfCircle CenterX=176.411 CenterY=35.2 CenterZ=0 NormalX=0 NormalY=0 NormalZ=1 AngleXU=0 Radius=20 StartAngle=2.94023 EndAngle=3.34295
    g10: ArcOfCircle CenterX=188.411 CenterY=35.2 CenterZ=0 NormalX=0 NormalY=0 NormalZ=1 AngleXU=0 Radius=20 StartAngle=2.94023 EndAngle=3.34295
    g11: LineSegment StartX=157.815 StartY=39.2 StartZ=0 EndX=167.815 EndY=39.2 EndZ=0
    g12: LineSegment StartX=157.436 StartY=36.2 StartZ=0 EndX=167.436 EndY=36.2 EndZ=0
    g13: ArcOfCircle CenterX=177.411 CenterY=35.2 CenterZ=0 NormalX=0 NormalY=0 NormalZ=1 AngleXU=0 Radius=20 StartAngle=2.94023 EndAngle=3.09157
    g14: ArcOfCircle CenterX=187.411 CenterY=35.2 CenterZ=0 NormalX=0 NormalY=0 NormalZ=1 AngleXU=0 Radius=20 StartAngle=2.94023 EndAngle=3.09157
  constraints (46):
    c: PointOnObject(g0,g-3)
    c: Tangent(g0,g-6)
    c: Coincident(g1,g0)
    c: Horizontal(g1)
    c: Radius(g2) = 3.5
    c: Coincident(g2,g-5)
    c: PointOnObject(g3,g-3)
    c: Parallel(g3,g-4)
    c: Tangent(g3,g2) = 1.5708
    c: Horizontal(g4)
    c: Tangent(g4,g2) = -1.5708
    c: Coincident(g5,g1)
    c: Parallel(g5,g-4)
    c: Coincident(g5,g4)
    c: DistanceX(g4,g-8) = 3.8
    c: Coincident(g6,g0)
    c: PointOnObject(g6,g-3)
    c: Coincident(g7,g3)
    c: PointOnObject(g7,g-3)
    c: Horizontal(g8)
    c: DistanceX(g6,g7) = 12
    c: Vertical(g8,g6)
    c: Vertical(g7,g8)
    c: DistanceY(g8,g6) = 8
    c: Coincident(g9,g8)
    c: Coincident(g9,g6)
    c: Coincident(g10,g7)
    c: Coincident(g10,g8)
    c: Radius(g9) = 20
    c: Radius(g10) = 20
    c: PointOnObject(g11,g-3)
    c: PointOnObject(g11,g-3)
    c: DistanceX(g11,g11) = 10
    c: DistanceX(g6,g11) = 1
    c: Horizontal(g12)
    c: Equal(g12,g11)
    c: DistanceY(g12,g11) = 3
    c: Coincident(g13,g11)
    c: Coincident(g13,g12)
    c: Radius(g13) = 20
    c: Coincident(g14,g11)
    c: Coincident(g14,g12)
    c: Radius(g14) = 20
    c: DistanceX(g0,g6) = 19
    c: Horizontal(g9,g13)
    c: Horizontal(g0,g-4)
FEATURE [Sketcher::SketchObject] Sketch096  label="Sketch096 - forma impugnatura"
  ArcFitTolerance = 1e-06
  AttachmentSupport = -> [Pad019]
  ExternalGeometry = -> [Binder]
  FullyConstrained = true
  MakeInternals = false
  MapMode = 5
  Placement = pos=(0,2,0) rot=(0,0.707107,0.707107;3.14159rad)
  sketch-geometry (8):
    g0: LineSegment StartX=176.685 StartY=-80.4316 StartZ=0 EndX=143.955 EndY=20.303 EndZ=0
    g1: LineSegment StartX=176.685 StartY=-80.4316 StartZ=0 EndX=215.932 EndY=-80.4316 EndZ=0
    g2: Circle CenterX=179.305 CenterY=-76.8316 CenterZ=0 NormalX=0 NormalY=0 NormalZ=1 AngleXU=0 Radius=3
    g3: Circle CenterX=213.443 CenterY=-76.8316 CenterZ=0 NormalX=0 NormalY=0 NormalZ=1 AngleXU=0 Radius=3
    g4: LineSegment StartX=143.955 StartY=20.303 StartZ=0 EndX=202.765 EndY=20.303 EndZ=0
    g5: LineSegment StartX=215.42 StartY=-53.0314 StartZ=0 EndX=192.176 EndY=-3.18451 EndZ=0
    g6: ArcOfCircle CenterX=184.801 CenterY=-67.3089 CenterZ=0 NormalX=0 NormalY=0 NormalZ=1 AngleXU=0 Radius=33.7833 StartAngle=5.88425 EndAngle=6.71952
    g7: ArcOfCircle CenterX=207.583 CenterY=4 CenterZ=0 NormalX=0 NormalY=0 NormalZ=1 AngleXU=0 Radius=17 StartAngle=1.85815 EndAngle=3.57792
  constraints (19):
    c: Coincident(g0,g-4)
    c: PointOnObject(g0,g-3)
    c: Horizontal(g0,g-7)
    c: Coincident(g1,g0)
    c: Coincident(g1,g-5)
    c: Diameter(g2) = 6
    c: Diameter(g3) = 6
    c: Coincident(g2,g-9)
    c: Coincident(g3,g-10)
    c: Coincident(g4,g0)
    c: Coincident(g5,g-6)
    c: Coincident(g6,g1)
    c: Coincident(g6,g5)
    c: Equal(g-5,g6)
    c: Coincident(g5,g-7)
    c: Coincident(g4,g-7)
    c: Tangent(g7,g-7)
    c: Coincident(g7,g4)
    c: Coincident(g7,g5)
FEATURE [Sketcher::SketchObject] Sketch097
  ArcFitTolerance = 1e-06
  AttachmentSupport = -> [Pad019]
  ExternalGeometry = -> [Binder]
  FullyConstrained = true
  MakeInternals = false
  MapMode = 5
  Placement = pos=(0,2,0) rot=(0,0.707107,0.707107;3.14159rad)
  sketch-geometry (4):
    g0: LineSegment StartX=90 StartY=36.8 StartZ=0 EndX=108 EndY=36.8 EndZ=0
    g1: LineSegment StartX=108 StartY=36.8 StartZ=0 EndX=108 EndY=26.8 EndZ=0
    g2: LineSegment StartX=108 StartY=26.8 StartZ=0 EndX=90 EndY=26.8 EndZ=0
    g3: ArcOfCircle CenterX=94 CenterY=31.8 CenterZ=0 NormalX=0 NormalY=0 NormalZ=1 AngleXU=0 Radius=6.40312 StartAngle=2.24554 EndAngle=4.03765
  constraints (13):
    c: Horizontal(g0)
    c: Coincident(g1,g0)
    c: Vertical(g1)
    c: DistanceX(g0,g0) = 18
    c: DistanceY(g1,g1) = 10
    c: Coincident(g2,g1)
    c: Horizontal(g2)
    c: Equal(g2,g0)
    c: DistanceY(g0,g-3) = 2.4
    c: Coincident(g3,g0)
    c: Coincident(g3,g2)
    c: DistanceX(g2,g3) = 4
    c: DistanceX(g-3,g0) = 90
FEATURE [PartDesign::Chamfer] Chamfer015
  Angle = 45
  Base = -> Pad019 [Edge19,Edge22,Edge79]
  BaseFeature = -> Pad019
  ChamferType = 0
  FlipDirection = false
  Refine = true
  Size = 1.9
  Size2 = 1
  SupportTransform = false
  Suppressed = false
  UseAllEdges = false
FEATURE [PartDesign::Pocket] Pocket002
  BaseFeature = -> Chamfer015
  Direction = (0,1,-2e-16)
  Length = 1.2
  Length2 = 5
  Profile = -> Sketch093
  ReferenceAxis = -> Sketch093 [N_Axis]
  Refine = true
  Suppressed = false
  Type = 0
FEATURE [PartDesign::Pad] Pad005
  BaseFeature = -> Pocket002
  Direction = (0,1,-2e-16)
  Length = 1.6
  Length2 = 10
  Profile = -> Sketch091
  ReferenceAxis = -> Sketch091 [N_Axis]
  Refine = true
  Suppressed = false
  Type = 0
FEATURE [Sketcher::SketchObject] Sketch092  label="Sketch092 - scavi per viti anteriori"
  ArcFitTolerance = 1e-06
  AttachmentSupport = -> [Pad005]
  ExternalGeometry = -> [Binder]
  FullyConstrained = true
  MakeInternals = false
  MapMode = 5
  Placement = pos=(0,3.6,0) rot=(0,0.707107,0.707107;3.14159rad)
  sketch-geometry (20):
    g0: ArcOfCircle CenterX=5.6 CenterY=7.6 CenterZ=0 NormalX=0 NormalY=0 NormalZ=1 AngleXU=0 Radius=3.5 StartAngle=0 EndAngle=1.5708
    g1: ArcOfCircle CenterX=5.6 CenterY=34.8 CenterZ=0 NormalX=0 NormalY=0 NormalZ=1 AngleXU=0 Radius=3.5 StartAngle=4.71239 EndAngle=6.28319
    g2: ArcOfCircle CenterX=78.51 CenterY=34.8 CenterZ=0 NormalX=0 NormalY=0 NormalZ=1 AngleXU=0 Radius=3.5 StartAngle=3.14159 EndAngle=4.71239
    g3: ArcOfCircle CenterX=78.51 CenterY=7.6 CenterZ=0 NormalX=0 NormalY=0 NormalZ=1 AngleXU=0 Radius=3.5 StartAngle=1.5708 EndAngle=3.14159
    g4: LineSegment StartX=0 StartY=3.2 StartZ=0 EndX=0 EndY=11.1 EndZ=0
    g5: LineSegment StartX=0 StartY=11.1 StartZ=0 EndX=5.6 EndY=11.1 EndZ=0
    g6: LineSegment StartX=0 StartY=3.2 StartZ=0 EndX=9.1 EndY=3.2 EndZ=0
    g7: LineSegment StartX=9.1 StartY=3.2 StartZ=0 EndX=9.1 EndY=7.6 EndZ=0
    g8: LineSegment StartX=0 StartY=39.2 StartZ=0 EndX=0 EndY=31.3 EndZ=0
    g9: LineSegment StartX=0 StartY=31.3 StartZ=0 EndX=5.6 EndY=31.3 EndZ=0
    g10: LineSegment StartX=0 StartY=39.2 StartZ=0 EndX=9.1 EndY=39.2 EndZ=0
    g11: LineSegment StartX=9.1 StartY=39.2 StartZ=0 EndX=9.1 EndY=34.8 EndZ=0
    g12: LineSegment StartX=82.8 StartY=39.2 StartZ=0 EndX=75.01 EndY=39.2 EndZ=0
    g13: LineSegment StartX=82.8 StartY=39.2 StartZ=0 EndX=82.8 EndY=31.3 EndZ=0
    g14: LineSegment StartX=82.8 StartY=31.3 StartZ=0 EndX=78.51 EndY=31.3 EndZ=0
    g15: LineSegment StartX=82.8 StartY=3.2 StartZ=0 EndX=75.01 EndY=3.2 EndZ=0
    g16: LineSegment StartX=75.01 StartY=3.2 StartZ=0 EndX=75.01 EndY=7.6 EndZ=0
    g17: LineSegment StartX=82.8 StartY=3.2 StartZ=0 EndX=82.8 EndY=11.1 EndZ=0
    g18: LineSegment StartX=82.8 StartY=11.1 StartZ=0 EndX=78.51 EndY=11.1 EndZ=0
    g19: LineSegment StartX=75.01 StartY=39.2 StartZ=0 EndX=75.01 EndY=34.8 EndZ=0
  constraints (48):
    c: Radius(g0) = 3.5
    c: Coincident(g0,g-10)
    c: Radius(g1) = 3.5
    c: Coincident(g1,g-9)
    c: Radius(g2) = 3.5
    c: Coincident(g2,g-8)
    c: Radius(g3) = 3.5
    c: Coincident(g3,g-7)
    c: Coincident(g4,g-5)
    c: PointOnObject(g4,g-4)
    c: Coincident(g5,g4)
    c: Horizontal(g5)
    c: Coincident(g6,g4)
    c: PointOnObject(g6,g-5)
    c: Coincident(g7,g6)
    c: Vertical(g7)
    c: Coincident(g8,g-4)
    c: PointOnObject(g8,g-4)
    c: Coincident(g9,g8)
    c: Horizontal(g9)
    c: Coincident(g10,g8)
    c: PointOnObject(g10,g-3)
    c: Coincident(g11,g10)
    c: Vertical(g11)
    c: PointOnObject(g12,g-3)
    c: PointOnObject(g12,g-3)
    c: Coincident(g13,g12)
    c: Vertical(g13)
    c: Coincident(g14,g13)
    c: Horizontal(g14)
    c: Coincident(g15,g-6)
    c: PointOnObject(g15,g-5)
    c: Coincident(g16,g15)
    c: Vertical(g16)
    c: Coincident(g17,g15)
    c: Coincident(g18,g17)
    c: Horizontal(g18)
    c: Tangent(g3,g18) = -1.5708
    c: Tangent(g16,g3) = 1.5708
    c: Coincident(g19,g12)
    c: Vertical(g19)
    c: Tangent(g2,g19) = -1.5708
    c: Tangent(g2,g14) = 1.5708
    c: Tangent(g0,g7) = -1.5708
    c: Tangent(g0,g5) = 1.5708
    c: Tangent(g9,g1) = -1.5708
    c: Tangent(g1,g11) = 1.5708
    c: Tangent(g17,g13)
FEATURE [PartDesign::Pocket] Pocket001
  BaseFeature = -> Pad005
  Direction = (0,-1,2e-16)
  Length = 1.6
  Length2 = 5
  Profile = -> Sketch092
  ReferenceAxis = -> Sketch092 [N_Axis]
  Refine = true
  Suppressed = false
  Type = 0
FEATURE [PartDesign::Pad] Pad006
  BaseFeature = -> Pocket001
  Direction = (0,1,-2e-16)
  Length = 0.8
  Length2 = 10
  Profile = -> Sketch094
  ReferenceAxis = -> Sketch094 [N_Axis]
  Refine = true
  Suppressed = false
  Type = 0
FEATURE [PartDesign::Pad] Pad007
  BaseFeature = -> Pad006
  Direction = (0,1,-2e-16)
  Length = 2
  Length2 = 10
  Profile = -> Sketch095
  ReferenceAxis = -> Sketch095 [N_Axis]
  Refine = true
  Suppressed = false
  Type = 0
FEATURE [PartDesign::Pad] Pad008  label="Pad008 - forma impugnatura"
  BaseFeature = -> Pad007
  Direction = (0,1,-2e-16)
  Length = 1.6
  Length2 = 10
  Profile = -> Sketch096
  ReferenceAxis = -> Sketch096 [N_Axis]
  Refine = true
  Suppressed = false
  Type = 0
FEATURE [PartDesign::Pad] Pad009
  BaseFeature = -> Pad008
  Direction = (0,1,-2e-16)
  Length = 1.6
  Length2 = 10
  Profile = -> Sketch097
  ReferenceAxis = -> Sketch097 [N_Axis]
  Refine = true
  Suppressed = false
  Type = 0
FEATURE [Sketcher::SketchObject] Sketch098
  ArcFitTolerance = 1e-06
  AttachmentSupport = -> [Pad006]
  ExternalGeometry = -> [Binder]
  FullyConstrained = true
  MakeInternals = false
  MapMode = 5
  Placement = pos=(0,2.8,-7e-16) rot=(0,0.707107,0.707107;3.14159rad)
  sketch-geometry (4):
    g0: LineSegment StartX=118 StartY=39.2 StartZ=0 EndX=129 EndY=39.2 EndZ=0
    g1: LineSegment StartX=120.599 StartY=31.2 StartZ=0 EndX=131.599 EndY=31.2 EndZ=0
    g2: LineSegment StartX=129 StartY=39.2 StartZ=0 EndX=131.599 EndY=31.2 EndZ=0
    g3: LineSegment StartX=118 StartY=39.2 StartZ=0 EndX=120.599 EndY=31.2 EndZ=0
  constraints (12):
    c: PointOnObject(g0,g-3)
    c: PointOnObject(g0,g-3)
    c: DistanceX(g0,g0) = 11
    c: Horizontal(g1)
    c: Equal(g1,g0)
    c: Coincident(g2,g0)
    c: Coincident(g3,g0)
    c: Parallel(g-4,g2)
    c: Coincident(g1,g2)
    c: Coincident(g1,g3)
    c: DistanceY(g1,g0) = 8
    c: DistanceX(g-3,g0) = 118
FEATURE [Sketcher::SketchObject] Sketch099
  ArcFitTolerance = 1e-06
  AttachmentSupport = -> [Pad008]
  ExternalGeometry = -> [Binder]
  FullyConstrained = true
  MakeInternals = false
  MapMode = 5
  Placement = pos=(0,3.6,0) rot=(0,0.707107,0.707107;3.14159rad)
  sketch-geometry (13):
    g0: LineSegment StartX=192.176 StartY=-3.18451 StartZ=0 EndX=196.804 EndY=-13.1108 EndZ=0
    g1: LineSegment [constr] StartX=202.765 StartY=20.303 StartZ=0 EndX=181.223 EndY=20.303 EndZ=0
    g2: LineSegment [constr] StartX=181.223 StartY=20.303 StartZ=0 EndX=181.223 EndY=-3.18451 EndZ=0
    g3: ArcOfCircle CenterX=181.223 CenterY=-20.3764 CenterZ=0 NormalX=0 NormalY=0 NormalZ=1 AngleXU=0 Radius=17.1918 StartAngle=0.436332 EndAngle=1.57079
    g4: ArcOfEllipse CenterX=181.223 CenterY=8.55923 CenterZ=0 NormalX=0 NormalY=0 NormalZ=1 MajorRadius=23.4779 MinorRadius=11.7437 AngleXU=0 StartAngle=1.5708 EndAngle=4.71239
    g5: LineSegment [constr] StartX=204.701 StartY=8.55923 StartZ=0 EndX=157.745 EndY=8.55923 EndZ=0
    g6: LineSegment [constr] StartX=181.223 StartY=20.303 StartZ=0 EndX=181.223 EndY=-3.18451 EndZ=0
    g7: GeomPoint [constr] X=201.553 Y=8.55923 Z=0
    g8: GeomPoint [constr] X=160.894 Y=8.55923 Z=0
    g9: GeomPoint [constr] X=181.223 Y=-3.18451 Z=0
    g10: LineSegment StartX=181.223 StartY=20.303 StartZ=0 EndX=202.765 EndY=20.303 EndZ=0
    g11: ArcOfCircle CenterX=207.583 CenterY=4 CenterZ=0 NormalX=0 NormalY=0 NormalZ=1 AngleXU=0 Radius=17 StartAngle=1.85815 EndAngle=3.57792
    g12: LineSegment [constr] StartX=172.411 StartY=39.2 StartZ=0 EndX=192.176 EndY=-3.18451 EndZ=0
  constraints (27):
    c: Coincident(g1,g-7)
    c: Horizontal(g1)
    c: Coincident(g2,g1)
    c: Vertical(g2)
    c: Horizontal(g2,g0)
    c: Coincident(g3,g0)
    c: Coincident(g3,g2)
    c: InternalAlignment(g5-g8 -> g4) x4
    c: Horizontal(g5)
    c: PointOnObject(g4,g2)
    c: Coincident(g4,g1)
    c: DistanceX(g-3,g5) = 10.1
    c: Coincident(g4,g2)
    c: Tangent(g3,g-5)
    c: PointOnObject(g9,g4)
    c: PointOnObject(g9,g3)
    c: Tangent(g4,g3,g9) = 1.5708
    c: Coincident(g10,g1)
    c: Coincident(g10,g1)
    c: Equal(g11,g-4)
    c: Coincident(g11,g1)
    c: Coincident(g11,g0)
    c: PointOnObject(g12,g-6)
    c: PointOnObject(g1,g12)
    c: Tangent(g12,g-5) = -1.5708
    c: Tangent(g0,g-5) = -1.5708
    c: Horizontal(g9,g12)
FEATURE [Sketcher::SketchObject] Sketch106  label="Sketch106 - smusso impuniatura interno"
  ArcFitTolerance = 1e-06
  AttachmentSupport = -> [Pad008]
  ExternalGeometry = -> [Pad008]
  FullyConstrained = true
  MakeInternals = false
  MapMode = 5
  Placement = pos=(0,-1.585e-13,-80.4316) rot=(1,0,0;3.14159rad)
  sketch-geometry (9):
    g0: LineSegment StartX=-176.685 StartY=-3.6 StartZ=0 EndX=-176.685 EndY=2.12528e-11 EndZ=0
    g1: LineSegment [constr] StartX=-176.685 StartY=1.79e-14 StartZ=0 EndX=-176.685 EndY=2.12527e-11 EndZ=0
    g2: LineSegment [constr] StartX=-186.685 StartY=-3.6 StartZ=0 EndX=-186.685 EndY=2.12528e-11 EndZ=0
    g3: ArcOfEllipse CenterX=-186.685 CenterY=2.12527e-11 CenterZ=0 NormalX=0 NormalY=0 NormalZ=1 MajorRadius=10 MinorRadius=3.6 AngleXU=-3.14159 StartAngle=1.5708 EndAngle=3.14159
    g4: LineSegment [constr] StartX=-196.685 StartY=1.79e-14 StartZ=0 EndX=-176.685 EndY=1.79e-14 EndZ=0
    g5: LineSegment [constr] StartX=-186.685 StartY=-3.6 StartZ=0 EndX=-186.685 EndY=3.6 EndZ=0
    g6: GeomPoint [constr] X=-196.015 Y=1.55e-14 Z=0
    g7: GeomPoint [constr] X=-177.356 Y=1.85e-14 Z=0
    g8: LineSegment StartX=-176.685 StartY=-3.6 StartZ=0 EndX=-186.685 EndY=-3.6 EndZ=0
  constraints (15):
    c: PointOnObject(g2,g-3)
    c: Coincident(g1,g-5)
    c: DistanceY(g1,g1) = 0
    c: Coincident(g0,g1)
    c: DistanceX(g2,g-5) = 10
    c: Vertical(g2)
    c: Horizontal(g2,g0)
    c: InternalAlignment(g4-g7 -> g3) x4
    c: Coincident(g3,g2)
    c: Horizontal(g4)
    c: Coincident(g3,g0)
    c: Tangent(g0,g-5) = 1.5708
    c: Coincident(g3,g2)
    c: Coincident(g8,g0)
    c: Coincident(g8,g2)
FEATURE [Sketcher::SketchObject] Sketch107  label="Sketch107 - smusso impugnatura esterno"
  ArcFitTolerance = 1e-06
  AttachmentSupport = -> [Pad008]
  ExternalGeometry = -> [Pad008]
  FullyConstrained = true
  MakeInternals = false
  MapMode = 5
  Placement = pos=(0,-1.585e-13,-80.4316) rot=(1,0,0;3.14159rad)
  sketch-geometry (9):
    g0: LineSegment [constr] StartX=-215.932 StartY=1.79e-14 StartZ=0 EndX=-215.932 EndY=2.09e-14 EndZ=0
    g1: LineSegment StartX=-215.932 StartY=-3.6 StartZ=0 EndX=-215.932 EndY=2.09e-14 EndZ=0
    g2: LineSegment StartX=-215.932 StartY=-3.6 StartZ=0 EndX=-205.932 EndY=-3.6 EndZ=0
    g3: LineSegment [constr] StartX=-205.932 StartY=-3.6 StartZ=0 EndX=-205.932 EndY=2.09e-14 EndZ=0
    g4: ArcOfEllipse CenterX=-205.932 CenterY=2.09e-14 CenterZ=0 NormalX=0 NormalY=0 NormalZ=1 MajorRadius=10 MinorRadius=3.6 AngleXU=3.14159 StartAngle=1e-16 EndAngle=1.5708
    g5: LineSegment [constr] StartX=-215.932 StartY=1.79e-14 StartZ=0 EndX=-195.932 EndY=1.79e-14 EndZ=0
    g6: LineSegment [constr] StartX=-205.932 StartY=-3.6 StartZ=0 EndX=-205.932 EndY=3.6 EndZ=0
    g7: GeomPoint [constr] X=-215.262 Y=2.14e-14 Z=0
    g8: GeomPoint [constr] X=-196.602 Y=1.78e-14 Z=0
  constraints (16):
    c: Coincident(g0,g-6)
    c: PointOnObject(g0,g-6)
    c: DistanceY(g0,g0) = 0
    c: Coincident(g1,g-6)
    c: Coincident(g1,g0)
    c: Tangent(g2,g-3)
    c: DistanceX(g2,g2) = 10
    c: Coincident(g3,g2)
    c: Vertical(g3)
    c: Horizontal(g3,g0)
    c: InternalAlignment(g5-g8 -> g4) x4
    c: Coincident(g4,g3)
    c: Horizontal(g5)
    c: Coincident(g4,g0)
    c: Coincident(g4,g2)
    c: PointOnObject(g2,g1)
FEATURE [Sketcher::SketchObject] Sketch108
  ArcFitTolerance = 1e-06
  AttachmentOffset = pos=(0,0,-1.6) rot=(0,0,1;0rad)
  AttachmentSupport = -> [Pad008]
  ExternalGeometry = -> [Binder]
  FullyConstrained = true
  MakeInternals = false
  MapMode = 5
  Placement = pos=(0,2,4e-16) rot=(0,0.707107,0.707107;3.14159rad)
  sketch-geometry (14):
    g0: LineSegment StartX=192.176 StartY=-3.18451 StartZ=0 EndX=193.827 EndY=-6.72678 EndZ=0
    g1: LineSegment [constr] StartX=202.765 StartY=20.303 StartZ=0 EndX=181.223 EndY=20.303 EndZ=0
    g2: LineSegment [constr] StartX=181.223 StartY=20.303 StartZ=0 EndX=181.223 EndY=1.30297 EndZ=0
    g3: ArcOfCircle CenterX=181.223 CenterY=-12.6042 CenterZ=0 NormalX=0 NormalY=0 NormalZ=1 AngleXU=0 Radius=13.9072 StartAngle=0.436332 EndAngle=1.5708
    g4: ArcOfEllipse CenterX=181.223 CenterY=10.803 CenterZ=0 NormalX=0 NormalY=0 NormalZ=1 MajorRadius=14.4779 MinorRadius=9.5 AngleXU=0 StartAngle=1.5708 EndAngle=4.71239
    g5: LineSegment [constr] StartX=195.701 StartY=10.803 StartZ=0 EndX=166.745 EndY=10.803 EndZ=0
    g6: LineSegment [constr] StartX=181.223 StartY=20.303 StartZ=0 EndX=181.223 EndY=1.30297 EndZ=0
    g7: GeomPoint [constr] X=192.148 Y=10.803 Z=0
    g8: GeomPoint [constr] X=170.298 Y=10.803 Z=0
    g9: LineSegment StartX=181.223 StartY=20.303 StartZ=0 EndX=202.765 EndY=20.303 EndZ=0
    g10: ArcOfCircle CenterX=207.583 CenterY=4 CenterZ=0 NormalX=0 NormalY=0 NormalZ=1 AngleXU=0 Radius=17 StartAngle=1.85815 EndAngle=3.57792
    g11: LineSegment [constr] StartX=172.411 StartY=39.2 StartZ=0 EndX=192.176 EndY=-3.18451 EndZ=0
    g12: GeomPoint [constr] X=181.223 Y=1.30297 Z=0
    g13: GeomPoint [constr] X=181.223 Y=1.30297 Z=0
  constraints (28):
    c: Coincident(g1,g-7)
    c: Horizontal(g1)
    c: Coincident(g2,g1)
    c: Vertical(g2)
    c: Coincident(g3,g2)
    c: InternalAlignment(g5-g8 -> g4) x4
    c: Horizontal(g5)
    c: PointOnObject(g4,g2)
    c: Coincident(g4,g1)
    c: DistanceX(g-3,g5) = 19.1
    c: Coincident(g4,g2)
    c: Coincident(g9,g1)
    c: Coincident(g9,g1)
    c: Coincident(g10,g1)
    c: Coincident(g10,g0)
    c: PointOnObject(g11,g-6)
    c: PointOnObject(g1,g11)
    c: DistanceY(g2,g1) = 19
    c: Coincident(g10,g-4)
    c: PointOnObject(g12,g4)
    c: PointOnObject(g12,g3)
    c: Tangent(g11,g-5) = -1.5708
    c: Tangent(g0,g-5) = -1.5708
    c: Tangent(g3,g0) = 1.5708
    c: PointOnObject(g13,g4)
    c: PointOnObject(g13,g3)
    c: Tangent(g4,g3,g13) = 1.5708
    c: Horizontal(g11,g0)
FEATURE [Part::Part2DObjectPython] Clone2D  label="Sketch108 (2D)"  # Draft 2D object (typed FeaturePython)
  Fuse = false
  Objects = -> [Sketch108]
  Placement = pos=(0,2,4e-16) rot=(0,0.707107,0.707107;3.14159rad)
  Scale = (1,1,1)
FEATURE [Sketcher::SketchObject] Sketch109
  ArcFitTolerance = 1e-06
  AttachmentOffset = pos=(0,0,-3.5) rot=(0,0,1;0rad)
  AttachmentSupport = -> [Pad008]
  ExternalGeometry = -> [Binder]
  FullyConstrained = true
  MakeInternals = false
  MapMode = 5
  Placement = pos=(0,0.1,8e-16) rot=(0,0.707107,0.707107;3.14159rad)
  sketch-geometry (1):
    g0: GeomPoint X=197.47 Y=8.55923 Z=0
  constraints (1):
    c: Symmetric(g-7,g-5,g0)
FEATURE [PartDesign::Chamfer] Chamfer005
  Angle = 45
  Base = -> Pad009 [Edge215,Edge212]
  BaseFeature = -> Pad009
  ChamferType = 1
  FlipDirection = false
  Refine = true
  Size = 1.5
  Size2 = 2.8
  SupportTransform = false
  Suppressed = false
  UseAllEdges = false
FEATURE [Sketcher::SketchObject] Sketch111
  ArcFitTolerance = 1e-06
  AttachmentSupport = -> [Pad009]
  ExternalGeometry = -> [Pad009]
  FullyConstrained = true
  MakeInternals = false
  MapMode = 5
  Placement = pos=(0,3.6,-8e-16) rot=(0,0.707107,0.707107;3.14159rad)
  sketch-geometry (21):
    g0: LineSegment [constr] StartX=97 StartY=36.8 StartZ=0 EndX=97 EndY=26.8 EndZ=0
    g1: LineSegment StartX=97 StartY=28.6 StartZ=0 EndX=97 EndY=27.8 EndZ=0
    g2: LineSegment StartX=97 StartY=27.8 StartZ=0 EndX=108 EndY=27.8 EndZ=0
    g3: LineSegment StartX=108 StartY=27.8 StartZ=0 EndX=108 EndY=28.6 EndZ=0
    g4: LineSegment StartX=108 StartY=28.6 StartZ=0 EndX=97 EndY=28.6 EndZ=0
    g5: LineSegment StartX=97 StartY=35.8 StartZ=0 EndX=97 EndY=35 EndZ=0
    g6: LineSegment StartX=97 StartY=35 StartZ=0 EndX=108 EndY=35 EndZ=0
    g7: LineSegment StartX=108 StartY=35 StartZ=0 EndX=108 EndY=35.8 EndZ=0
    g8: LineSegment StartX=108 StartY=35.8 StartZ=0 EndX=97 EndY=35.8 EndZ=0
    g9: LineSegment StartX=97 StartY=30.4 StartZ=0 EndX=97 EndY=29.6 EndZ=0
    g10: LineSegment StartX=97 StartY=29.6 StartZ=0 EndX=108 EndY=29.6 EndZ=0
    g11: LineSegment StartX=108 StartY=29.6 StartZ=0 EndX=108 EndY=30.4 EndZ=0
    g12: LineSegment StartX=108 StartY=30.4 StartZ=0 EndX=97 EndY=30.4 EndZ=0
    g13: LineSegment StartX=97 StartY=34 StartZ=0 EndX=97 EndY=33.2 EndZ=0
    g14: LineSegment StartX=97 StartY=33.2 StartZ=0 EndX=108 EndY=33.2 EndZ=0
    g15: LineSegment StartX=108 StartY=33.2 StartZ=0 EndX=108 EndY=34 EndZ=0
    g16: LineSegment StartX=108 StartY=34 StartZ=0 EndX=97 EndY=34 EndZ=0
    g17: LineSegment StartX=97 StartY=32.2 StartZ=0 EndX=97 EndY=31.4 EndZ=0
    g18: LineSegment StartX=97 StartY=31.4 StartZ=0 EndX=108 EndY=31.4 EndZ=0
    g19: LineSegment StartX=108 StartY=31.4 StartZ=0 EndX=108 EndY=32.2 EndZ=0
    g20: LineSegment StartX=108 StartY=32.2 StartZ=0 EndX=97 EndY=32.2 EndZ=0
  constraints (54):
    c: Vertical(g0)
    c: PointOnObject(g0,g-3)
    c: PointOnObject(g0,g-4)
    c: DistanceX(g0,g-5) = 11
    c: Coincident(g1,g2)
    c: Coincident(g2,g3)
    c: Coincident(g3,g4)
    c: Coincident(g4,g1)
    c: Horizontal(g2)
    c: Horizontal(g4)
    c: Tangent(g1,g0)
    c: Tangent(g3,g-5)
    c: DistanceY(g2,g3) = 0.8
    c: Coincident(g5,g6)
    c: Coincident(g6,g7)
    c: Coincident(g7,g8)
    c: Coincident(g8,g5)
    c: Horizontal(g6)
    c: Horizontal(g8)
    c: DistanceY(g6,g7) = 0.8
    c: Coincident(g9,g10)
    c: Coincident(g10,g11)
    c: Coincident(g11,g12)
    c: Coincident(g12,g9)
    c: Horizontal(g10)
    c: Horizontal(g12)
    c: DistanceY(g10,g11) = 0.8
    c: Tangent(g5,g0)
    c: Tangent(g7,g-5)
    c: Tangent(g9,g0)
    c: Tangent(g11,g-5)
    c: Coincident(g13,g14)
    c: Coincident(g14,g15)
    c: Coincident(g15,g16)
    c: Coincident(g16,g13)
    c: Horizontal(g14)
    c: Horizontal(g16)
    c: DistanceY(g14,g15) = 0.8
    c: Tangent(g13,g0)
    c: Tangent(g15,g-5)
    c: Coincident(g17,g18)
    c: Coincident(g18,g19)
    c: Coincident(g19,g20)
    c: Coincident(g20,g17)
    c: Horizontal(g18)
    c: Horizontal(g20)
    c: DistanceY(g18,g19) = 0.8
    c: Tangent(g17,g0)
    c: Tangent(g19,g-5)
    c: DistanceY(g1,g9) = 1
    c: DistanceY(g9,g17) = 1
    c: DistanceY(g17,g13) = 1
    c: DistanceY(g13,g5) = 1
    c: DistanceY(g0,g1) = 1
FEATURE [PartDesign::Pocket] Pocket004
  BaseFeature = -> Chamfer005
  Direction = (0,-1,2e-16)
  Length = 1
  Length2 = 5
  Profile = -> Sketch111
  ReferenceAxis = -> Sketch111 [N_Axis]
  Refine = true
  Suppressed = false
  Type = 0
FEATURE [PartDesign::Pad] Pad010
  BaseFeature = -> Pocket004
  Direction = (0,1,-2e-16)
  Length = 1.2
  Length2 = 10
  Profile = -> Sketch098
  ReferenceAxis = -> Sketch098 [N_Axis]
  Refine = true
  Suppressed = false
  Type = 0
FEATURE [PartDesign::Chamfer] Chamfer006
  Angle = 45
  Base = -> Pad010 [Edge291]
  BaseFeature = -> Pad010
  ChamferType = 1
  FlipDirection = false
  Refine = true
  Size = 1
  Size2 = 6
  SupportTransform = false
  Suppressed = false
  UseAllEdges = false
FEATURE [Sketcher::SketchObject] Sketch110
  ArcFitTolerance = 1e-06
  AttachmentSupport = -> [Pad010]
  ExternalGeometry = -> [Sketch098]
  FullyConstrained = true
  MakeInternals = false
  MapMode = 5
  Placement = pos=(0,4,-9e-16) rot=(0,0.707107,0.707107;3.14159rad)
  sketch-geometry (8):
    g0: LineSegment StartX=119.69 StartY=34 StartZ=0 EndX=130.69 EndY=34 EndZ=0
    g1: LineSegment StartX=119.95 StartY=33.2 StartZ=0 EndX=130.95 EndY=33.2 EndZ=0
    g2: LineSegment StartX=119.137 StartY=35.7 StartZ=0 EndX=130.137 EndY=35.7 EndZ=0
    g3: LineSegment StartX=118.877 StartY=36.5 StartZ=0 EndX=129.877 EndY=36.5 EndZ=0
    g4: LineSegment StartX=118.877 StartY=36.5 StartZ=0 EndX=119.137 EndY=35.7 EndZ=0
    g5: LineSegment StartX=129.877 StartY=36.5 StartZ=0 EndX=130.137 EndY=35.7 EndZ=0
    g6: LineSegment StartX=119.69 StartY=34 StartZ=0 EndX=119.95 EndY=33.2 EndZ=0
    g7: LineSegment StartX=130.69 StartY=34 StartZ=0 EndX=130.95 EndY=33.2 EndZ=0
  constraints (24):
    c: Horizontal(g0)
    c: Horizontal(g1)
    c: Horizontal(g2)
    c: Horizontal(g3)
    c: Equal(g1,g-5)
    c: Equal(g0,g-5)
    c: Equal(g2,g-5)
    c: Equal(g3,g-5)
    c: PointOnObject(g0,g-3)
    c: PointOnObject(g1,g-3)
    c: PointOnObject(g2,g-3)
    c: PointOnObject(g3,g-3)
    c: Coincident(g4,g3)
    c: Coincident(g4,g2)
    c: Coincident(g5,g3)
    c: Coincident(g5,g2)
    c: Coincident(g6,g0)
    c: Coincident(g6,g1)
    c: Coincident(g7,g0)
    c: Coincident(g7,g1)
    c: DistanceY(g1,g0) = 0.8
    c: DistanceY(g2,g3) = 0.8
    c: DistanceY(g-5,g1) = 2
    c: DistanceY(g-5,g2) = 4.5
FEATURE [PartDesign::Pocket] Pocket003
  BaseFeature = -> Chamfer006
  Direction = (0,-1,2e-16)
  Length = 1
  Length2 = 5
  Profile = -> Sketch110
  ReferenceAxis = -> Sketch110 [N_Axis]
  Refine = true
  Suppressed = false
  Type = 0
FEATURE [PartDesign::SubtractivePipe] SubtractivePipe
  AuxilleryCurvelinear = true
  AuxillerySpineTangent = false
  BaseFeature = -> Pocket003
  Binormal = (0,0,0)
  Mode = 0
  Profile = -> Sketch106
  Refine = true
  Spine = -> Pad008 [Edge215]
  SpineTangent = false
  Suppressed = false
  Transformation = 0
  Transition = 0
FEATURE [PartDesign::SubtractivePipe] SubtractivePipe001
  AuxilleryCurvelinear = true
  AuxillerySpineTangent = false
  BaseFeature = -> SubtractivePipe
  Binormal = (0,0,0)
  Mode = 0
  Profile = -> Sketch107
  Refine = true
  Spine = -> Pad008 [Edge213,Edge216,Edge210]
  SpineTangent = false
  Suppressed = false
  Transformation = 0
  Transition = 0
FEATURE [PartDesign::SubtractiveLoft] SubtractiveLoft
  BaseFeature = -> SubtractivePipe001
  Closed = false
  Profile = -> Sketch099
  Refine = true
  Ruled = false
  Sections = -> [Sketch108]
  Suppressed = false
FEATURE [PartDesign::SubtractiveLoft] SubtractiveLoft001
  BaseFeature = -> SubtractiveLoft
  Closed = false
  Profile = -> Clone2D
  Refine = true
  Ruled = false
  Sections = -> [Sketch109]
  Suppressed = false
FEATURE [Sketcher::SketchObject] Sketch112
  ArcFitTolerance = 1e-06
  AttachmentSupport = -> [Pad008]
  ExternalGeometry = -> [Binder]
  FullyConstrained = true
  MakeInternals = false
  MapMode = 5
  Placement = pos=(0,3.6,0) rot=(0,0.707107,0.707107;3.14159rad)
  sketch-geometry (4):
    g0: LineSegment [constr] StartX=167.782 StartY=-53.0314 StartZ=0 EndX=215.42 EndY=-53.0314 EndZ=0
    g1: GeomPoint [constr] X=191.282 Y=-53.0314 Z=0
    g2: Circle CenterX=191.282 CenterY=-53.0314 CenterZ=0 NormalX=0 NormalY=0 NormalZ=1 AngleXU=0 Radius=11.5
    g3: Circle CenterX=191.282 CenterY=-53.0314 CenterZ=0 NormalX=0 NormalY=0 NormalZ=1 AngleXU=0 Radius=10.7
  constraints (9):
    c: Horizontal(g0)
    c: PointOnObject(g0,g-3)
    c: Diameter(g2) = 23
    c: Coincident(g2,g1)
    c: Diameter(g3) = 21.4
    c: Coincident(g3,g1)
    c: DistanceX(g0,g1) = 23.5
    c: PointOnObject(g1,g0)
    c: Coincident(g0,g-4)
FEATURE [PartDesign::Chamfer] Chamfer016
  Angle = 45
  Base = -> SubtractiveLoft001 [Edge118,Edge117,Edge119,Edge120,Edge109]
  BaseFeature = -> SubtractiveLoft001
  ChamferType = 0
  FlipDirection = false
  Refine = true
  Size = 1.5
  Size2 = 1
  SupportTransform = false
  Suppressed = false
  UseAllEdges = false
FEATURE [PartDesign::Chamfer] Chamfer017
  Angle = 45
  Base = -> Chamfer016 [Edge15]
  BaseFeature = -> Chamfer016
  ChamferType = 0
  FlipDirection = false
  Refine = true
  Size = 1.6
  Size2 = 1
  SupportTransform = false
  Suppressed = false
  UseAllEdges = false
FEATURE [PartDesign::Chamfer] Chamfer018
  Angle = 45
  Base = -> Chamfer017 [Edge10]
  BaseFeature = -> Chamfer017
  ChamferType = 0
  FlipDirection = false
  Refine = true
  Size = 3.5
  Size2 = 1
  SupportTransform = false
  Suppressed = false
  UseAllEdges = false
FEATURE [PartDesign::Chamfer] Chamfer019
  Angle = 45
  Base = -> Chamfer018 [Edge94,Edge199]
  BaseFeature = -> Chamfer018
  ChamferType = 0
  FlipDirection = false
  Refine = true
  Size = 1.9
  Size2 = 1
  SupportTransform = false
  Suppressed = false
  UseAllEdges = false
FEATURE [PartDesign::Fillet] Fillet009
  Base = -> Chamfer019 [Edge83]
  BaseFeature = -> Chamfer019
  Radius = 1.1
  Refine = true
  SupportTransform = false
  Suppressed = false
  UseAllEdges = false
FEATURE [PartDesign::Fillet] Fillet010
  Base = -> Fillet009 [Edge77]
  BaseFeature = -> Fillet009
  Radius = 1.9
  Refine = true
  SupportTransform = false
  Suppressed = false
  UseAllEdges = false
FEATURE [PartDesign::Pocket] Pocket005
  BaseFeature = -> Fillet010
  Direction = (0,-1,2e-16)
  Length = 0.8
  Length2 = 5
  Profile = -> Sketch112
  ReferenceAxis = -> Sketch112 [N_Axis]
  Refine = true
  Suppressed = false
  Type = 0
FEATURE [Part::Part2DObjectPython] ShapeString001  # Draft 2D object (typed FeaturePython)
  FontFile = <path>
  Fuse = false
  Justification = 6
  JustificationReference = 0
  KeepLeftMargin = false
  MakeFace = true
  ObliqueAngle = 0
  Placement = pos=(-183.5,3.6,-57.5) rot=(0,0.707107,0.707107;3.14159rad)
  ScaleToSize = true
  Size = 10
  String = AS
  Tracking = 0
FEATURE [PartDesign::Pocket] Pocket013
  BaseFeature = -> Pocket005
  Direction = (-1e-16,-1,2e-16)
  Length = 1
  Length2 = 5
  Profile = -> ShapeString001
  ReferenceAxis = -> ShapeString001 [N_Axis]
  Refine = true
  Suppressed = false
  Type = 0
FEATURE [PartDesign::Body] Body006  label="lato SX"
  AllowCompound = false
  Group = -> [Binder,Pad019,Chamfer015,Pocket002,Sketch133,Sketch091,Pad005,Sketch092,Pocket001,Sketch093,Sketch094,Pad006,Sketch095,Pad007,Sketch096,Pad008,Sketch097,Pad009,Chamfer005,Pocket004,Sketch098,Pad010,Chamfer006,Pocket003,SubtractivePipe,SubtractivePipe001,Sketch099,Sketch106,Sketch107,Sketch108,Clone2D,Sketch109,SubtractiveLoft,SubtractiveLoft001,Sketch110,Sketch111,Sketch112,Chamfer016,Chamfer017,+7 more]
  Origin = -> Origin006
  Tip = -> Pocket013
FEATURE [PartDesign::Pad] Pad020
  Direction = (0,-1,2e-16)
  Length = 25.2
  Length2 = 10
  Midplane = true
  Placement = pos=(0,0,0) rot=(1,0,0;1.5708rad)
  Profile = -> Sketch021
  ReferenceAxis = -> Sketch021 [N_Axis]
  Refine = true
  Suppressed = false
  Type = 0
FEATURE [PartDesign::Body] Body001  label="perno fermo rumble e driver solenoide"
  AllowCompound = false
  Group = -> [Sketch021,Pad020]
  Origin = -> Origin001
  Tip = -> Pad020
FEATURE [PartDesign::Pad] Pad021
  Direction = (0,-1,2e-16)
  Length = 16.8
  Length2 = 10
  Midplane = true
  Placement = pos=(0,0,0) rot=(1,0,0;1.5708rad)
  Profile = -> Sketch061
  ReferenceAxis = -> Sketch061 [N_Axis]
  Refine = true
  Suppressed = false
  Type = 0
FEATURE [PartDesign::Pocket] Pocket014
  BaseFeature = -> Pad021
  Direction = (0,1,-2e-16)
  Length = 12.8
  Length2 = 5
  Midplane = true
  Placement = pos=(0,0,0) rot=(1,0,0;1.5708rad)
  Profile = -> Sketch062
  ReferenceAxis = -> Sketch062 [N_Axis]
  Refine = true
  Suppressed = false
  Type = 0
FEATURE [PartDesign::Pad] Pad022
  BaseFeature = -> Pocket014
  Direction = (0,-1,2e-16)
  Length = 7.6
  Length2 = 10
  Midplane = true
  Placement = pos=(0,0,0) rot=(1,0,0;1.5708rad)
  Profile = -> Sketch063
  ReferenceAxis = -> Sketch063 [N_Axis]
  Refine = true
  Suppressed = false
  Type = 0
FEATURE [PartDesign::Body] Body003  label="blocco switch"
  AllowCompound = false
  Group = -> [Sketch061,Sketch062,Sketch063,Pad021,Pocket014,Pad022]
  Origin = -> Origin003
  Tip = -> Pad022
FEATURE [PartDesign::Pad] Pad024
  Direction = (0,-1,2e-16)
  Length = 17
  Length2 = 10
  Midplane = true
  Placement = pos=(0,0,0) rot=(1,0,0;1.5708rad)
  Profile = -> Sketch045
  ReferenceAxis = -> Sketch045 [N_Axis]
  Refine = true
  Suppressed = false
  Type = 0
FEATURE [PartDesign::Pocket] Pocket015
  BaseFeature = -> Pad024
  Direction = (-1,0,0)
  Length = 8
  Length2 = 5
  Placement = pos=(0,0,0) rot=(1,0,0;1.5708rad)
  Profile = -> Sketch047
  ReferenceAxis = -> Sketch047 [N_Axis]
  Refine = true
  Reversed = true
  Suppressed = false
  Type = 0
FEATURE [PartDesign::Pocket] Pocket016
  BaseFeature = -> Pocket015
  Direction = (-1,0,0)
  Length = 1
  Length2 = 5
  Placement = pos=(0,0,0) rot=(1,0,0;1.5708rad)
  Profile = -> Sketch046
  ReferenceAxis = -> Sketch046 [N_Axis]
  Refine = true
  Reversed = true
  Suppressed = false
  Type = 0
FEATURE [PartDesign::Pocket] Pocket017
  BaseFeature = -> Pocket016
  Direction = (0,1,-2e-16)
  Length = 17
  Length2 = 5
  Midplane = true
  Placement = pos=(0,0,0) rot=(1,0,0;1.5708rad)
  Profile = -> Sketch048
  ReferenceAxis = -> Sketch048 [N_Axis]
  Refine = true
  Suppressed = false
  Type = 0
FEATURE [PartDesign::Pad] Pad025
  BaseFeature = -> Pocket017
  Direction = (0,-1,2e-16)
  Length = 17
  Length2 = 10
  Midplane = true
  Placement = pos=(0,0,0) rot=(1,0,0;1.5708rad)
  Profile = -> Sketch049
  ReferenceAxis = -> Sketch049 [N_Axis]
  Refine = true
  Suppressed = false
  Type = 0
FEATURE [PartDesign::Pad] Pad026
  BaseFeature = -> Pad025
  Direction = (0,-1,2e-16)
  Length = 17
  Length2 = 10
  Midplane = true
  Placement = pos=(0,0,0) rot=(1,0,0;1.5708rad)
  Profile = -> Sketch066
  ReferenceAxis = -> Sketch066 [N_Axis]
  Refine = true
  Suppressed = false
  Type = 0
FEATURE [PartDesign::Pad] Pad027
  BaseFeature = -> Pad026
  Direction = (0,-1,2e-16)
  Length = 5
  Length2 = 10
  Midplane = true
  Placement = pos=(0,0,0) rot=(1,0,0;1.5708rad)
  Profile = -> Sketch064
  ReferenceAxis = -> Sketch064 [N_Axis]
  Refine = true
  Suppressed = false
  Type = 0
FEATURE [PartDesign::Pad] Pad028
  BaseFeature = -> Pad027
  Direction = (1,0,0)
  Length = 1
  Length2 = 10
  Placement = pos=(0,0,0) rot=(1,0,0;1.5708rad)
  Profile = -> Sketch068
  ReferenceAxis = -> Sketch068 [N_Axis]
  Refine = true
  Reversed = true
  Suppressed = false
  Type = 0
FEATURE [PartDesign::Chamfer] Chamfer020
  Angle = 45
  Base = -> Pad028 [Edge73,Edge75,Edge78,Edge77]
  BaseFeature = -> Pad028
  ChamferType = 0
  FlipDirection = false
  Placement = pos=(0,0,0) rot=(1,0,0;1.5708rad)
  Refine = true
  Size = 0.5
  Size2 = 1
  SupportTransform = false
  Suppressed = false
  UseAllEdges = false
FEATURE [PartDesign::Body] Body002  label="supporto per neopixel"
  AllowCompound = false
  Group = -> [Sketch045,Sketch047,Sketch046,Sketch048,Sketch049,Sketch066,Sketch064,Sketch068,Pad024,Pocket015,Pocket016,Pocket017,Pad025,Pad026,Pad027,Pad028,Chamfer020]
  Origin = -> Origin002
  Tip = -> Chamfer020
FEATURE [Sketcher::SketchObject] Sketch134  label="perno fermo rumble002"
  ArcFitTolerance = 1e-06
  AttachmentSupport = -> [XZ_Plane008]
  FullyConstrained = true
  MakeInternals = false
  MapMode = 5
  Placement = pos=(0,0,0) rot=(1,0,0;1.5708rad)
  sketch-geometry (16):
    g0: LineSegment StartX=0 StartY=0.45 StartZ=0 EndX=0 EndY=1.55 EndZ=0
    g1: LineSegment StartX=0.45 StartY=2 StartZ=0 EndX=1.55 EndY=2 EndZ=0
    g2: LineSegment StartX=2 StartY=1.55 StartZ=0 EndX=2 EndY=0.45 EndZ=0
    g3: LineSegment StartX=1.55 StartY=0 StartZ=0 EndX=0.45 EndY=0 EndZ=0
    g4: ArcOfCircle [constr] CenterX=0.45 CenterY=1.55 CenterZ=0 NormalX=0 NormalY=0 NormalZ=1 AngleXU=0 Radius=0.45 StartAngle=1.5708 EndAngle=3.14159
    g5: GeomPoint [constr] X=0 Y=2 Z=0
    g6: LineSegment StartX=0.45 StartY=2 StartZ=0 EndX=0 EndY=1.55 EndZ=0
    g7: ArcOfCircle [constr] CenterX=1.55 CenterY=1.55 CenterZ=0 NormalX=0 NormalY=0 NormalZ=1 AngleXU=0 Radius=0.45 StartAngle=0 EndAngle=1.5708
    g8: GeomPoint [constr] X=2 Y=2 Z=0
    g9: LineSegment StartX=2 StartY=1.55 StartZ=0 EndX=1.55 EndY=2 EndZ=0
    g10: ArcOfCircle [constr] CenterX=1.55 CenterY=0.45 CenterZ=0 NormalX=0 NormalY=0 NormalZ=1 AngleXU=0 Radius=0.45 StartAngle=4.71239 EndAngle=6.28319
    g11: GeomPoint [constr] X=2 Y=0 Z=0
    g12: LineSegment StartX=1.55 StartY=0 StartZ=0 EndX=2 EndY=0.45 EndZ=0
    g13: ArcOfCircle [constr] CenterX=0.45 CenterY=0.45 CenterZ=0 NormalX=0 NormalY=0 NormalZ=1 AngleXU=0 Radius=0.45 StartAngle=3.14159 EndAngle=4.71239
    g14: GeomPoint [constr] X=0 Y=0 Z=0
    g15: LineSegment StartX=0 StartY=0.45 StartZ=0 EndX=0.45 EndY=0 EndZ=0
  constraints (35):
    c: Coincident(g14,g-1)
    c: PointOnObject(g5,g-2)
    c: Horizontal(g1)
    c: Vertical(g2)
    c: Horizontal(g3)
    c: DistanceX(g5,g8) = 2
    c: DistanceY(g11,g8) = 2
    c: PointOnObject(g5,g0)
    c: PointOnObject(g5,g1)
    c: Tangent(g0,g4) = 1.5708
    c: Tangent(g1,g4) = 1.5708
    c: Coincident(g6,g0)
    c: Coincident(g6,g1)
    c: PointOnObject(g8,g2)
    c: PointOnObject(g8,g1)
    c: Tangent(g2,g7) = 1.5708
    c: Tangent(g1,g7) = 1.5708
    c: Coincident(g9,g2)
    c: Coincident(g9,g1)
    c: PointOnObject(g11,g2)
    c: PointOnObject(g11,g3)
    c: Tangent(g2,g10) = 1.5708
    c: Tangent(g3,g10) = 1.5708
    c: Coincident(g12,g2)
    c: Coincident(g12,g3)
    c: PointOnObject(g14,g0)
    c: PointOnObject(g14,g3)
    c: Tangent(g0,g13) = 1.5708
    c: Tangent(g3,g13) = 1.5708
    c: Coincident(g15,g0)
    c: Coincident(g15,g3)
    c: Equal(g6,g9)
    c: Equal(g9,g12)
    c: Equal(g12,g15)
    c: DistanceX(g14,g3) = 0.45
FEATURE [PartDesign::Pad] Pad029
  Direction = (0,-1,2e-16)
  Length = 17
  Length2 = 10
  Midplane = true
  Placement = pos=(0,0,0) rot=(1,0,0;1.5708rad)
  Profile = -> Sketch134
  ReferenceAxis = -> Sketch134 [N_Axis]
  Refine = true
  Suppressed = false
  Type = 0
FEATURE [PartDesign::Body] Body008  label="perno fermo neopixel"
  AllowCompound = false
  Group = -> [Sketch134,Pad029]
  Origin = -> Origin008
  Tip = -> Pad029
FEATURE [Sketcher::SketchObject] Sketch135  label="perno fermo rumble003"
  ArcFitTolerance = 1e-06
  AttachmentSupport = -> [XZ_Plane009]
  FullyConstrained = true
  MakeInternals = false
  MapMode = 5
  Placement = pos=(0,0,0) rot=(1,0,0;1.5708rad)
  sketch-geometry (16):
    g0: LineSegment StartX=4.69e-14 StartY=0.8 StartZ=0 EndX=-3.04e-14 EndY=3.1 EndZ=0
    g1: LineSegment StartX=0.8 StartY=3.9 StartZ=0 EndX=3.1 EndY=3.9 EndZ=0
    g2: LineSegment StartX=3.9 StartY=3.1 StartZ=0 EndX=3.9 EndY=0.8 EndZ=0
    g3: LineSegment StartX=3.1 StartY=0 StartZ=0 EndX=0.8 EndY=0 EndZ=0
    g4: ArcOfCircle [constr] CenterX=0.8 CenterY=3.1 CenterZ=0 NormalX=0 NormalY=0 NormalZ=1 AngleXU=0 Radius=0.8 StartAngle=1.5708 EndAngle=3.14159
    g5: GeomPoint [constr] X=0 Y=3.9 Z=0
    g6: LineSegment StartX=0.8 StartY=3.9 StartZ=0 EndX=-3.04e-14 EndY=3.1 EndZ=0
    g7: ArcOfCircle [constr] CenterX=3.1 CenterY=3.1 CenterZ=0 NormalX=0 NormalY=0 NormalZ=1 AngleXU=0 Radius=0.8 StartAngle=-2.4e-14 EndAngle=1.5708
    g8: GeomPoint [constr] X=3.9 Y=3.9 Z=0
    g9: LineSegment StartX=3.9 StartY=3.1 StartZ=0 EndX=3.1 EndY=3.9 EndZ=0
    g10: ArcOfCircle [constr] CenterX=3.1 CenterY=0.8 CenterZ=0 NormalX=0 NormalY=0 NormalZ=1 AngleXU=0 Radius=0.8 StartAngle=4.71239 EndAngle=6.28319
    g11: GeomPoint [constr] X=3.9 Y=0 Z=0
    g12: LineSegment StartX=3.1 StartY=0 StartZ=0 EndX=3.9 EndY=0.8 EndZ=0
    g13: ArcOfCircle [constr] CenterX=0.8 CenterY=0.8 CenterZ=0 NormalX=0 NormalY=0 NormalZ=1 AngleXU=0 Radius=0.8 StartAngle=3.14159 EndAngle=4.71239
    g14: GeomPoint [constr] X=0 Y=0 Z=0
    g15: LineSegment StartX=4.69e-14 StartY=0.8 StartZ=0 EndX=0.8 EndY=0 EndZ=0
  constraints (35):
    c: Coincident(g14,g-1)
    c: PointOnObject(g5,g-2)
    c: Horizontal(g1)
    c: Vertical(g2)
    c: Horizontal(g3)
    c: DistanceX(g5,g8) = 3.9
    c: DistanceY(g11,g8) = 3.9
    c: PointOnObject(g5,g0)
    c: PointOnObject(g5,g1)
    c: Tangent(g0,g4) = 1.5708
    c: Tangent(g1,g4) = 1.5708
    c: Coincident(g6,g0)
    c: Coincident(g6,g1)
    c: PointOnObject(g8,g2)
    c: PointOnObject(g8,g1)
    c: Tangent(g2,g7) = 1.5708
    c: Tangent(g1,g7) = 1.5708
    c: Coincident(g9,g2)
    c: Coincident(g9,g1)
    c: PointOnObject(g11,g2)
    c: PointOnObject(g11,g3)
    c: Tangent(g2,g10) = 1.5708
    c: Tangent(g3,g10) = 1.5708
    c: Coincident(g12,g2)
    c: Coincident(g12,g3)
    c: PointOnObject(g14,g0)
    c: PointOnObject(g14,g3)
    c: Tangent(g0,g13) = 1.5708
    c: Tangent(g3,g13) = 1.5708
    c: Coincident(g15,g0)
    c: Coincident(g15,g3)
    c: Equal(g6,g9)
    c: Equal(g9,g12)
    c: Equal(g12,g15)
    c: DistanceX(g14,g3) = 0.8
FEATURE [PartDesign::Pad] Pad030
  Direction = (0,-1,2e-16)
  Length = 25.2
  Length2 = 10
  Midplane = true
  Placement = pos=(0,0,0) rot=(1,0,0;1.5708rad)
  Profile = -> Sketch135
  ReferenceAxis = -> Sketch135 [N_Axis]
  Refine = true
  Suppressed = false
  Type = 0
FEATURE [PartDesign::Body] Body009  label="perno fermo switch - caricabatterie - grilletto"
  AllowCompound = false
  Group = -> [Sketch135,Pad030]
  Origin = -> Origin009
  Tip = -> Pad030
note: 2 file-system paths scrubbed to <path> (originals preserved in the JSON sidecar)
